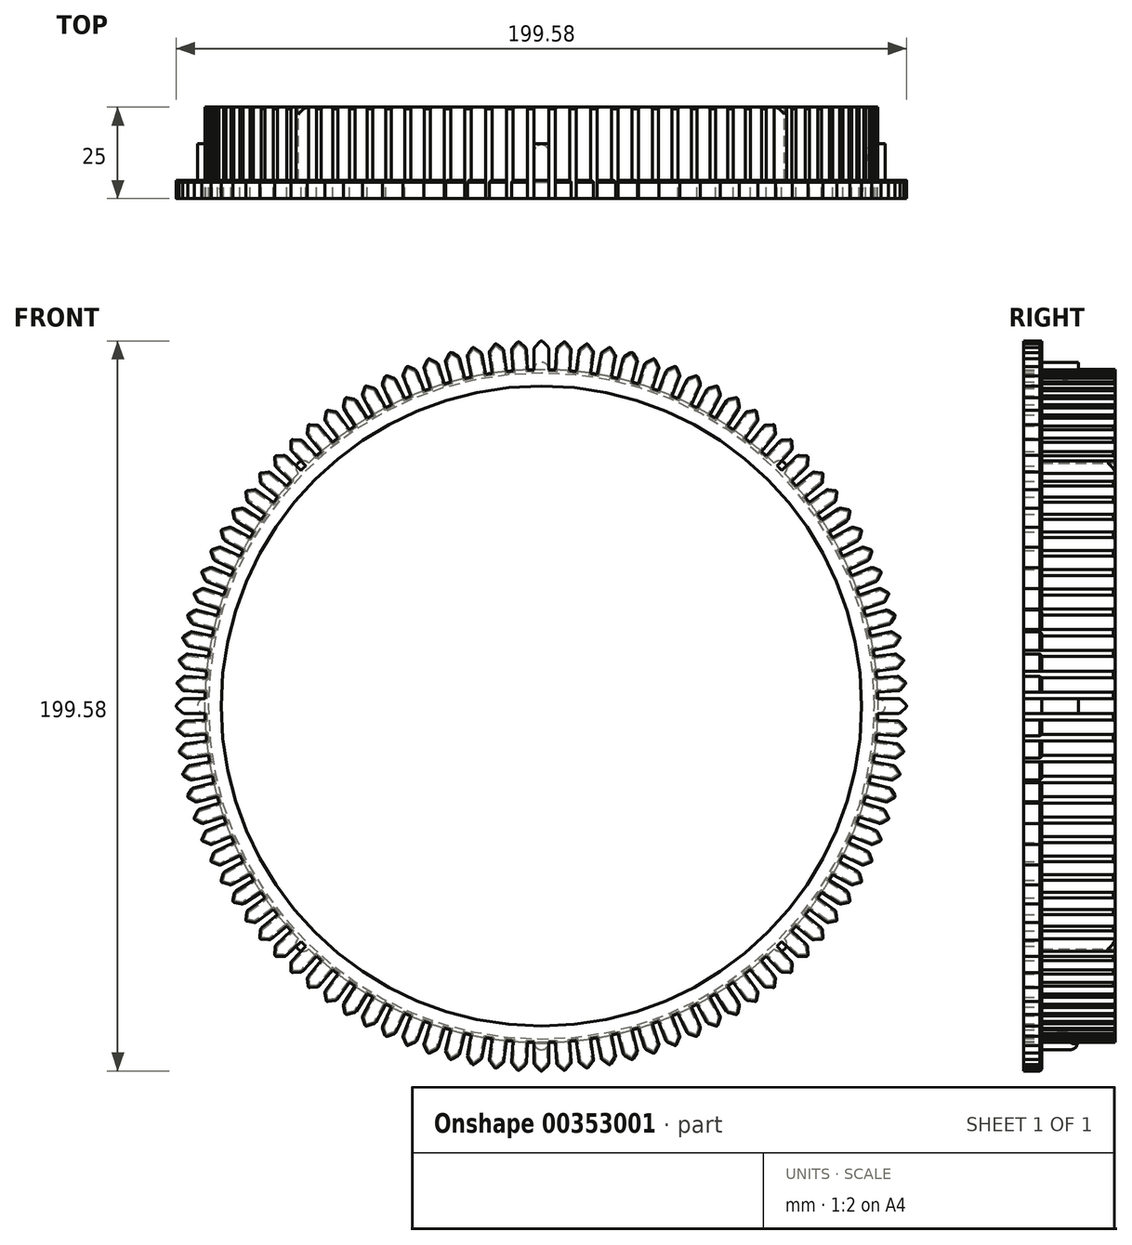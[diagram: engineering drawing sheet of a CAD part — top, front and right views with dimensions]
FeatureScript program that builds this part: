
annotation { "Feature Type Name" : "Feature", "Feature Type Description" : "" }
export const myFeature = defineFeature(function(context is Context, id is Id, definition is map)
    precondition{}
    {
        {
            var Q0;
            Q0=qCreatedBy(makeId("Front.planeOp"),FACE);
            var sketch = newSketch(context, id + "F0", { "sketchPlane" : qUnion([Q0])});
            skArc(sketch, "E0", {"start": v(-18.82, 88) * mm, "mid": v(-19.63, 87.83) * mm, "end": v(-20.44, 87.65) * mm});
            skCircle(sketch, "E1", {"center": v(0, 0) * mm, "radius": 98 * mm, "construction": true});
            skLineSegment(sketch, "E2", {"start": v(0, 100) * mm, "end": v(0, -100) * mm, "construction": true});
            skLineSegment(sketch, "E3", {"start": v(-100, 0) * mm, "end": v(100, 0) * mm, "construction": true});
            skLineSegment(sketch, "E4", {"start": v(-2, 89.98) * mm, "end": v(-2, 97.57) * mm});
            skLineSegment(sketch, "E5", {"start": v(-1.71, 98.27) * mm, "end": v(-0.36, 99.64) * mm});
            skPoint(sketch, "E6.visualSharp", {"position": v(-2, 97.98) * mm});
            skArc(sketch, "E6.filletArc", {"start": v(-1.71, 98.27) * mm, "mid": v(-1.92, 97.95) * mm, "end": v(-2, 97.57) * mm});
            skLineSegment(sketch, "E7.MirrorCS", {"start": v(1.71, 98.27) * mm, "end": v(0.36, 99.64) * mm});
            skArc(sketch, "E8.MirrorCS", {"start": v(1.71, 98.27) * mm, "mid": v(1.92, 97.95) * mm, "end": v(2, 97.57) * mm});
            skLineSegment(sketch, "E9.MirrorCS", {"start": v(2, 89.98) * mm, "end": v(2, 97.57) * mm});
            skPoint(sketch, "E10.visualSharp", {"position": v(0, 100) * mm});
            skArc(sketch, "E10.filletArc", {"start": v(0.36, 99.64) * mm, "mid": v(0, 99.79) * mm, "end": v(-0.36, 99.64) * mm});
            skLineSegment(sketch, "E11.1.0", {"start": v(-7.88, 97.97) * mm, "end": v(-6.61, 99.42) * mm});
            skArc(sketch, "E11.1.1", {"start": v(-5.9, 99.47) * mm, "mid": v(-6.27, 99.6) * mm, "end": v(-6.61, 99.42) * mm});
            skLineSegment(sketch, "E11.1.2", {"start": v(-4.46, 98.19) * mm, "end": v(-5.9, 99.47) * mm});
            skArc(sketch, "E11.1.3", {"start": v(-4.46, 98.19) * mm, "mid": v(-4.23, 97.88) * mm, "end": v(-4.13, 97.5) * mm});
            skArc(sketch, "E11.1.4", {"start": v(-7.88, 97.97) * mm, "mid": v(-8.07, 97.63) * mm, "end": v(-8.12, 97.25) * mm});
            skLineSegment(sketch, "E11.1.5", {"start": v(-7.65, 89.67) * mm, "end": v(-8.12, 97.25) * mm});
            skLineSegment(sketch, "E11.1.6", {"start": v(-3.65, 89.93) * mm, "end": v(-4.13, 97.5) * mm});
            skLineSegment(sketch, "E11.2.0", {"start": v(-14.01, 97.28) * mm, "end": v(-12.84, 98.81) * mm});
            skArc(sketch, "E11.2.1", {"start": v(-12.14, 98.9) * mm, "mid": v(-12.5, 99) * mm, "end": v(-12.84, 98.81) * mm});
            skLineSegment(sketch, "E11.2.2", {"start": v(-10.62, 97.71) * mm, "end": v(-12.14, 98.9) * mm});
            skArc(sketch, "E11.2.3", {"start": v(-10.62, 97.71) * mm, "mid": v(-10.37, 97.42) * mm, "end": v(-10.24, 97.05) * mm});
            skArc(sketch, "E11.2.4", {"start": v(-14.01, 97.28) * mm, "mid": v(-14.19, 96.94) * mm, "end": v(-14.21, 96.55) * mm});
            skLineSegment(sketch, "E11.2.5", {"start": v(-13.26, 89.02) * mm, "end": v(-14.21, 96.55) * mm});
            skLineSegment(sketch, "E11.2.6", {"start": v(-9.3, 89.52) * mm, "end": v(-10.24, 97.05) * mm});
            skLineSegment(sketch, "E11.3.0", {"start": v(-20.1, 96.21) * mm, "end": v(-19.02, 97.8) * mm});
            skArc(sketch, "E11.3.1", {"start": v(-18.32, 97.94) * mm, "mid": v(-18.7, 98.02) * mm, "end": v(-19.02, 97.8) * mm});
            skLineSegment(sketch, "E11.3.2", {"start": v(-16.73, 96.85) * mm, "end": v(-18.32, 97.94) * mm});
            skArc(sketch, "E11.3.3", {"start": v(-16.73, 96.85) * mm, "mid": v(-16.46, 96.57) * mm, "end": v(-16.32, 96.21) * mm});
            skArc(sketch, "E11.3.4", {"start": v(-20.1, 96.21) * mm, "mid": v(-20.24, 95.85) * mm, "end": v(-20.25, 95.47) * mm});
            skLineSegment(sketch, "E11.3.5", {"start": v(-18.82, 88) * mm, "end": v(-20.25, 95.47) * mm});
            skLineSegment(sketch, "E11.3.6", {"start": v(-14.9, 88.76) * mm, "end": v(-16.32, 96.21) * mm});
            skLineSegment(sketch, "E11.4.0", {"start": v(-26.1, 94.76) * mm, "end": v(-25.12, 96.42) * mm});
            skArc(sketch, "E11.4.1", {"start": v(-24.44, 96.6) * mm, "mid": v(-24.82, 96.65) * mm, "end": v(-25.12, 96.42) * mm});
            skLineSegment(sketch, "E11.4.2", {"start": v(-22.78, 95.6) * mm, "end": v(-24.44, 96.6) * mm});
            skArc(sketch, "E11.4.3", {"start": v(-22.78, 95.6) * mm, "mid": v(-22.5, 95.35) * mm, "end": v(-22.33, 95) * mm});
            skArc(sketch, "E11.4.4", {"start": v(-26.1, 94.76) * mm, "mid": v(-26.22, 94.4) * mm, "end": v(-26.2, 94) * mm});
            skLineSegment(sketch, "E11.4.5", {"start": v(-24.31, 86.65) * mm, "end": v(-26.2, 94) * mm});
            skLineSegment(sketch, "E11.4.6", {"start": v(-20.44, 87.65) * mm, "end": v(-22.33, 95) * mm});
            skLineSegment(sketch, "E11.5.0", {"start": v(-32, 92.93) * mm, "end": v(-31.13, 94.65) * mm});
            skArc(sketch, "E11.5.1", {"start": v(-30.45, 94.87) * mm, "mid": v(-30.84, 94.9) * mm, "end": v(-31.13, 94.65) * mm});
            skLineSegment(sketch, "E11.5.2", {"start": v(-28.74, 94) * mm, "end": v(-30.45, 94.87) * mm});
            skArc(sketch, "E11.5.3", {"start": v(-28.74, 94) * mm, "mid": v(-28.44, 93.75) * mm, "end": v(-28.25, 93.41) * mm});
            skArc(sketch, "E11.5.4", {"start": v(-32, 92.93) * mm, "mid": v(-32.1, 92.56) * mm, "end": v(-32.05, 92.17) * mm});
            skLineSegment(sketch, "E11.5.5", {"start": v(-29.7, 84.96) * mm, "end": v(-32.05, 92.17) * mm});
            skLineSegment(sketch, "E11.5.6", {"start": v(-25.9, 86.2) * mm, "end": v(-28.25, 93.41) * mm});
            skLineSegment(sketch, "E11.6.0", {"start": v(-37.77, 90.74) * mm, "end": v(-37.01, 92.51) * mm});
            skArc(sketch, "E11.6.1", {"start": v(-36.35, 92.77) * mm, "mid": v(-36.73, 92.78) * mm, "end": v(-37.01, 92.51) * mm});
            skLineSegment(sketch, "E11.6.2", {"start": v(-34.59, 92) * mm, "end": v(-36.35, 92.77) * mm});
            skArc(sketch, "E11.6.3", {"start": v(-34.59, 92) * mm, "mid": v(-34.27, 91.78) * mm, "end": v(-34.06, 91.45) * mm});
            skArc(sketch, "E11.6.4", {"start": v(-37.77, 90.74) * mm, "mid": v(-37.85, 90.36) * mm, "end": v(-37.78, 89.98) * mm});
            skLineSegment(sketch, "E11.6.5", {"start": v(-34.98, 82.92) * mm, "end": v(-37.78, 89.98) * mm});
            skLineSegment(sketch, "E11.6.6", {"start": v(-31.26, 84.4) * mm, "end": v(-34.06, 91.45) * mm});
            skLineSegment(sketch, "E11.7.0", {"start": v(-43.39, 88.2) * mm, "end": v(-42.75, 90) * mm});
            skArc(sketch, "E11.7.1", {"start": v(-42.1, 90.3) * mm, "mid": v(-42.49, 90.3) * mm, "end": v(-42.75, 90) * mm});
            skLineSegment(sketch, "E11.7.2", {"start": v(-40.3, 89.65) * mm, "end": v(-42.1, 90.3) * mm});
            skArc(sketch, "E11.7.3", {"start": v(-40.3, 89.65) * mm, "mid": v(-39.96, 89.45) * mm, "end": v(-39.73, 89.13) * mm});
            skArc(sketch, "E11.7.4", {"start": v(-43.39, 88.2) * mm, "mid": v(-43.45, 87.8) * mm, "end": v(-43.35, 87.43) * mm});
            skLineSegment(sketch, "E11.7.5", {"start": v(-40.12, 80.56) * mm, "end": v(-43.35, 87.43) * mm});
            skLineSegment(sketch, "E11.7.6", {"start": v(-36.5, 82.27) * mm, "end": v(-39.73, 89.13) * mm});
            skLineSegment(sketch, "E11.8.0", {"start": v(-48.84, 85.3) * mm, "end": v(-48.31, 87.14) * mm});
            skArc(sketch, "E11.8.1", {"start": v(-47.7, 87.49) * mm, "mid": v(-48.07, 87.45) * mm, "end": v(-48.31, 87.14) * mm});
            skLineSegment(sketch, "E11.8.2", {"start": v(-45.84, 86.94) * mm, "end": v(-47.7, 87.49) * mm});
            skArc(sketch, "E11.8.3", {"start": v(-45.84, 86.94) * mm, "mid": v(-45.5, 86.76) * mm, "end": v(-45.25, 86.46) * mm});
            skArc(sketch, "E11.8.4", {"start": v(-48.84, 85.3) * mm, "mid": v(-48.87, 84.9) * mm, "end": v(-48.76, 84.54) * mm});
            skLineSegment(sketch, "E11.8.5", {"start": v(-45.1, 77.88) * mm, "end": v(-48.76, 84.54) * mm});
            skLineSegment(sketch, "E11.8.6", {"start": v(-41.6, 79.81) * mm, "end": v(-45.25, 86.46) * mm});
            skLineSegment(sketch, "E11.9.0", {"start": v(-54.1, 82.06) * mm, "end": v(-53.7, 83.94) * mm});
            skArc(sketch, "E11.9.1", {"start": v(-53.1, 84.32) * mm, "mid": v(-53.47, 84.25) * mm, "end": v(-53.7, 83.94) * mm});
            skLineSegment(sketch, "E11.9.2", {"start": v(-51.21, 83.9) * mm, "end": v(-53.1, 84.32) * mm});
            skArc(sketch, "E11.9.3", {"start": v(-51.21, 83.9) * mm, "mid": v(-50.86, 83.73) * mm, "end": v(-50.6, 83.45) * mm});
            skArc(sketch, "E11.9.4", {"start": v(-54.1, 82.06) * mm, "mid": v(-54.1, 81.67) * mm, "end": v(-53.97, 81.3) * mm});
            skLineSegment(sketch, "E11.9.5", {"start": v(-49.9, 74.9) * mm, "end": v(-53.97, 81.3) * mm});
            skLineSegment(sketch, "E11.9.6", {"start": v(-46.52, 77.04) * mm, "end": v(-50.6, 83.45) * mm});
            skLineSegment(sketch, "E11.10.0", {"start": v(-59.15, 78.5) * mm, "end": v(-58.86, 80.4) * mm});
            skArc(sketch, "E11.10.1", {"start": v(-58.28, 80.82) * mm, "mid": v(-58.65, 80.73) * mm, "end": v(-58.86, 80.4) * mm});
            skLineSegment(sketch, "E11.10.2", {"start": v(-56.38, 80.5) * mm, "end": v(-58.28, 80.82) * mm});
            skArc(sketch, "E11.10.3", {"start": v(-56.38, 80.5) * mm, "mid": v(-56.02, 80.37) * mm, "end": v(-55.73, 80.11) * mm});
            skArc(sketch, "E11.10.4", {"start": v(-59.15, 78.5) * mm, "mid": v(-59.13, 78.11) * mm, "end": v(-58.97, 77.76) * mm});
            skLineSegment(sketch, "E11.10.5", {"start": v(-54.5, 71.62) * mm, "end": v(-58.97, 77.76) * mm});
            skLineSegment(sketch, "E11.10.6", {"start": v(-51.27, 73.97) * mm, "end": v(-55.73, 80.11) * mm});
            skLineSegment(sketch, "E11.11.0", {"start": v(-63.96, 74.63) * mm, "end": v(-63.79, 76.55) * mm});
            skArc(sketch, "E11.11.1", {"start": v(-63.24, 77) * mm, "mid": v(-63.6, 76.89) * mm, "end": v(-63.79, 76.55) * mm});
            skLineSegment(sketch, "E11.11.2", {"start": v(-61.32, 76.81) * mm, "end": v(-63.24, 77) * mm});
            skArc(sketch, "E11.11.3", {"start": v(-61.32, 76.81) * mm, "mid": v(-60.95, 76.7) * mm, "end": v(-60.65, 76.45) * mm});
            skArc(sketch, "E11.11.4", {"start": v(-63.96, 74.63) * mm, "mid": v(-63.92, 74.24) * mm, "end": v(-63.73, 73.9) * mm});
            skLineSegment(sketch, "E11.11.5", {"start": v(-58.9, 68.05) * mm, "end": v(-63.73, 73.9) * mm});
            skLineSegment(sketch, "E11.11.6", {"start": v(-55.81, 70.6) * mm, "end": v(-60.65, 76.45) * mm});
            skLineSegment(sketch, "E11.12.0", {"start": v(-68.52, 70.47) * mm, "end": v(-68.47, 72.4) * mm});
            skArc(sketch, "E11.12.1", {"start": v(-67.95, 72.88) * mm, "mid": v(-68.31, 72.74) * mm, "end": v(-68.47, 72.4) * mm});
            skLineSegment(sketch, "E11.12.2", {"start": v(-66.02, 72.8) * mm, "end": v(-67.95, 72.88) * mm});
            skArc(sketch, "E11.12.3", {"start": v(-66.02, 72.8) * mm, "mid": v(-65.65, 72.72) * mm, "end": v(-65.33, 72.5) * mm});
            skArc(sketch, "E11.12.4", {"start": v(-68.52, 70.47) * mm, "mid": v(-68.45, 70.08) * mm, "end": v(-68.25, 69.76) * mm});
            skLineSegment(sketch, "E11.12.5", {"start": v(-63.05, 64.22) * mm, "end": v(-68.25, 69.76) * mm});
            skLineSegment(sketch, "E11.12.6", {"start": v(-60.14, 66.96) * mm, "end": v(-65.33, 72.5) * mm});
            skLineSegment(sketch, "E11.13.0", {"start": v(-72.8, 66.02) * mm, "end": v(-72.88, 67.95) * mm});
            skArc(sketch, "E11.13.1", {"start": v(-72.4, 68.47) * mm, "mid": v(-72.74, 68.31) * mm, "end": v(-72.88, 67.95) * mm});
            skLineSegment(sketch, "E11.13.2", {"start": v(-70.47, 68.52) * mm, "end": v(-72.4, 68.47) * mm});
            skArc(sketch, "E11.13.3", {"start": v(-70.47, 68.52) * mm, "mid": v(-70.08, 68.45) * mm, "end": v(-69.76, 68.25) * mm});
            skArc(sketch, "E11.13.4", {"start": v(-72.8, 66.02) * mm, "mid": v(-72.72, 65.65) * mm, "end": v(-72.5, 65.33) * mm});
            skLineSegment(sketch, "E11.13.5", {"start": v(-66.96, 60.14) * mm, "end": v(-72.5, 65.33) * mm});
            skLineSegment(sketch, "E11.13.6", {"start": v(-64.22, 63.05) * mm, "end": v(-69.76, 68.25) * mm});
            skLineSegment(sketch, "E11.14.0", {"start": v(-76.81, 61.32) * mm, "end": v(-77, 63.24) * mm});
            skArc(sketch, "E11.14.1", {"start": v(-76.55, 63.79) * mm, "mid": v(-76.89, 63.6) * mm, "end": v(-77, 63.24) * mm});
            skLineSegment(sketch, "E11.14.2", {"start": v(-74.63, 63.96) * mm, "end": v(-76.55, 63.79) * mm});
            skArc(sketch, "E11.14.3", {"start": v(-74.63, 63.96) * mm, "mid": v(-74.24, 63.92) * mm, "end": v(-73.9, 63.73) * mm});
            skArc(sketch, "E11.14.4", {"start": v(-76.81, 61.32) * mm, "mid": v(-76.7, 60.95) * mm, "end": v(-76.45, 60.65) * mm});
            skLineSegment(sketch, "E11.14.5", {"start": v(-70.6, 55.81) * mm, "end": v(-76.45, 60.65) * mm});
            skLineSegment(sketch, "E11.14.6", {"start": v(-68.05, 58.9) * mm, "end": v(-73.9, 63.73) * mm});
            skLineSegment(sketch, "E11.15.0", {"start": v(-80.5, 56.38) * mm, "end": v(-80.82, 58.28) * mm});
            skArc(sketch, "E11.15.1", {"start": v(-80.4, 58.86) * mm, "mid": v(-80.73, 58.65) * mm, "end": v(-80.82, 58.28) * mm});
            skLineSegment(sketch, "E11.15.2", {"start": v(-78.5, 59.15) * mm, "end": v(-80.4, 58.86) * mm});
            skArc(sketch, "E11.15.3", {"start": v(-78.5, 59.15) * mm, "mid": v(-78.11, 59.13) * mm, "end": v(-77.76, 58.97) * mm});
            skArc(sketch, "E11.15.4", {"start": v(-80.5, 56.38) * mm, "mid": v(-80.37, 56.02) * mm, "end": v(-80.11, 55.73) * mm});
            skLineSegment(sketch, "E11.15.5", {"start": v(-73.97, 51.27) * mm, "end": v(-80.11, 55.73) * mm});
            skLineSegment(sketch, "E11.15.6", {"start": v(-71.62, 54.5) * mm, "end": v(-77.76, 58.97) * mm});
            skLineSegment(sketch, "E11.16.0", {"start": v(-83.9, 51.21) * mm, "end": v(-84.32, 53.1) * mm});
            skArc(sketch, "E11.16.1", {"start": v(-83.94, 53.7) * mm, "mid": v(-84.25, 53.47) * mm, "end": v(-84.32, 53.1) * mm});
            skLineSegment(sketch, "E11.16.2", {"start": v(-82.06, 54.1) * mm, "end": v(-83.94, 53.7) * mm});
            skArc(sketch, "E11.16.3", {"start": v(-82.06, 54.1) * mm, "mid": v(-81.67, 54.1) * mm, "end": v(-81.3, 53.97) * mm});
            skArc(sketch, "E11.16.4", {"start": v(-83.9, 51.21) * mm, "mid": v(-83.73, 50.86) * mm, "end": v(-83.45, 50.6) * mm});
            skLineSegment(sketch, "E11.16.5", {"start": v(-77.04, 46.52) * mm, "end": v(-83.45, 50.6) * mm});
            skLineSegment(sketch, "E11.16.6", {"start": v(-74.9, 49.9) * mm, "end": v(-81.3, 53.97) * mm});
            skLineSegment(sketch, "E11.17.0", {"start": v(-86.94, 45.84) * mm, "end": v(-87.49, 47.7) * mm});
            skArc(sketch, "E11.17.1", {"start": v(-87.14, 48.31) * mm, "mid": v(-87.45, 48.07) * mm, "end": v(-87.49, 47.7) * mm});
            skLineSegment(sketch, "E11.17.2", {"start": v(-85.3, 48.84) * mm, "end": v(-87.14, 48.31) * mm});
            skArc(sketch, "E11.17.3", {"start": v(-85.3, 48.84) * mm, "mid": v(-84.9, 48.87) * mm, "end": v(-84.54, 48.76) * mm});
            skArc(sketch, "E11.17.4", {"start": v(-86.94, 45.84) * mm, "mid": v(-86.76, 45.5) * mm, "end": v(-86.46, 45.25) * mm});
            skLineSegment(sketch, "E11.17.5", {"start": v(-79.81, 41.6) * mm, "end": v(-86.46, 45.25) * mm});
            skLineSegment(sketch, "E11.17.6", {"start": v(-77.88, 45.1) * mm, "end": v(-84.54, 48.76) * mm});
            skLineSegment(sketch, "E11.18.0", {"start": v(-89.65, 40.3) * mm, "end": v(-90.3, 42.1) * mm});
            skArc(sketch, "E11.18.1", {"start": v(-90, 42.75) * mm, "mid": v(-90.3, 42.49) * mm, "end": v(-90.3, 42.1) * mm});
            skLineSegment(sketch, "E11.18.2", {"start": v(-88.2, 43.39) * mm, "end": v(-90, 42.75) * mm});
            skArc(sketch, "E11.18.3", {"start": v(-88.2, 43.39) * mm, "mid": v(-87.8, 43.45) * mm, "end": v(-87.43, 43.35) * mm});
            skArc(sketch, "E11.18.4", {"start": v(-89.65, 40.3) * mm, "mid": v(-89.45, 39.96) * mm, "end": v(-89.13, 39.73) * mm});
            skLineSegment(sketch, "E11.18.5", {"start": v(-82.27, 36.5) * mm, "end": v(-89.13, 39.73) * mm});
            skLineSegment(sketch, "E11.18.6", {"start": v(-80.56, 40.12) * mm, "end": v(-87.43, 43.35) * mm});
            skLineSegment(sketch, "E11.19.0", {"start": v(-92, 34.59) * mm, "end": v(-92.77, 36.35) * mm});
            skArc(sketch, "E11.19.1", {"start": v(-92.51, 37.01) * mm, "mid": v(-92.78, 36.73) * mm, "end": v(-92.77, 36.35) * mm});
            skLineSegment(sketch, "E11.19.2", {"start": v(-90.74, 37.77) * mm, "end": v(-92.51, 37.01) * mm});
            skArc(sketch, "E11.19.3", {"start": v(-90.74, 37.77) * mm, "mid": v(-90.36, 37.85) * mm, "end": v(-89.98, 37.78) * mm});
            skArc(sketch, "E11.19.4", {"start": v(-92, 34.59) * mm, "mid": v(-91.78, 34.27) * mm, "end": v(-91.45, 34.06) * mm});
            skLineSegment(sketch, "E11.19.5", {"start": v(-84.4, 31.26) * mm, "end": v(-91.45, 34.06) * mm});
            skLineSegment(sketch, "E11.19.6", {"start": v(-82.92, 34.98) * mm, "end": v(-89.98, 37.78) * mm});
            skLineSegment(sketch, "E11.20.0", {"start": v(-94, 28.74) * mm, "end": v(-94.87, 30.45) * mm});
            skArc(sketch, "E11.20.1", {"start": v(-94.65, 31.13) * mm, "mid": v(-94.9, 30.84) * mm, "end": v(-94.87, 30.45) * mm});
            skLineSegment(sketch, "E11.20.2", {"start": v(-92.93, 32) * mm, "end": v(-94.65, 31.13) * mm});
            skArc(sketch, "E11.20.3", {"start": v(-92.93, 32) * mm, "mid": v(-92.56, 32.1) * mm, "end": v(-92.17, 32.05) * mm});
            skArc(sketch, "E11.20.4", {"start": v(-94, 28.74) * mm, "mid": v(-93.75, 28.44) * mm, "end": v(-93.41, 28.25) * mm});
            skLineSegment(sketch, "E11.20.5", {"start": v(-86.2, 25.9) * mm, "end": v(-93.41, 28.25) * mm});
            skLineSegment(sketch, "E11.20.6", {"start": v(-84.96, 29.7) * mm, "end": v(-92.17, 32.05) * mm});
            skLineSegment(sketch, "E11.21.0", {"start": v(-95.6, 22.78) * mm, "end": v(-96.6, 24.44) * mm});
            skArc(sketch, "E11.21.1", {"start": v(-96.42, 25.12) * mm, "mid": v(-96.65, 24.82) * mm, "end": v(-96.6, 24.44) * mm});
            skLineSegment(sketch, "E11.21.2", {"start": v(-94.76, 26.1) * mm, "end": v(-96.42, 25.12) * mm});
            skArc(sketch, "E11.21.3", {"start": v(-94.76, 26.1) * mm, "mid": v(-94.4, 26.22) * mm, "end": v(-94, 26.2) * mm});
            skArc(sketch, "E11.21.4", {"start": v(-95.6, 22.78) * mm, "mid": v(-95.35, 22.5) * mm, "end": v(-95, 22.33) * mm});
            skLineSegment(sketch, "E11.21.5", {"start": v(-87.65, 20.44) * mm, "end": v(-95, 22.33) * mm});
            skLineSegment(sketch, "E11.21.6", {"start": v(-86.65, 24.31) * mm, "end": v(-94, 26.2) * mm});
            skLineSegment(sketch, "E11.22.0", {"start": v(-96.85, 16.73) * mm, "end": v(-97.94, 18.32) * mm});
            skArc(sketch, "E11.22.1", {"start": v(-97.8, 19.02) * mm, "mid": v(-98.02, 18.7) * mm, "end": v(-97.94, 18.32) * mm});
            skLineSegment(sketch, "E11.22.2", {"start": v(-96.21, 20.1) * mm, "end": v(-97.8, 19.02) * mm});
            skArc(sketch, "E11.22.3", {"start": v(-96.21, 20.1) * mm, "mid": v(-95.85, 20.24) * mm, "end": v(-95.47, 20.25) * mm});
            skArc(sketch, "E11.22.4", {"start": v(-96.85, 16.73) * mm, "mid": v(-96.57, 16.46) * mm, "end": v(-96.21, 16.32) * mm});
            skLineSegment(sketch, "E11.22.5", {"start": v(-88.76, 14.9) * mm, "end": v(-96.21, 16.32) * mm});
            skLineSegment(sketch, "E11.22.6", {"start": v(-88, 18.82) * mm, "end": v(-95.47, 20.25) * mm});
            skLineSegment(sketch, "E11.23.0", {"start": v(-97.71, 10.62) * mm, "end": v(-98.9, 12.14) * mm});
            skArc(sketch, "E11.23.1", {"start": v(-98.81, 12.84) * mm, "mid": v(-99, 12.5) * mm, "end": v(-98.9, 12.14) * mm});
            skLineSegment(sketch, "E11.23.2", {"start": v(-97.28, 14.01) * mm, "end": v(-98.81, 12.84) * mm});
            skArc(sketch, "E11.23.3", {"start": v(-97.28, 14.01) * mm, "mid": v(-96.94, 14.19) * mm, "end": v(-96.55, 14.21) * mm});
            skArc(sketch, "E11.23.4", {"start": v(-97.71, 10.62) * mm, "mid": v(-97.42, 10.37) * mm, "end": v(-97.05, 10.24) * mm});
            skLineSegment(sketch, "E11.23.5", {"start": v(-89.52, 9.3) * mm, "end": v(-97.05, 10.24) * mm});
            skLineSegment(sketch, "E11.23.6", {"start": v(-89.02, 13.26) * mm, "end": v(-96.55, 14.21) * mm});
            skLineSegment(sketch, "E11.24.0", {"start": v(-98.19, 4.46) * mm, "end": v(-99.47, 5.9) * mm});
            skArc(sketch, "E11.24.1", {"start": v(-99.42, 6.61) * mm, "mid": v(-99.6, 6.27) * mm, "end": v(-99.47, 5.9) * mm});
            skLineSegment(sketch, "E11.24.2", {"start": v(-97.97, 7.88) * mm, "end": v(-99.42, 6.61) * mm});
            skArc(sketch, "E11.24.3", {"start": v(-97.97, 7.88) * mm, "mid": v(-97.63, 8.07) * mm, "end": v(-97.25, 8.12) * mm});
            skArc(sketch, "E11.24.4", {"start": v(-98.19, 4.46) * mm, "mid": v(-97.88, 4.23) * mm, "end": v(-97.5, 4.13) * mm});
            skLineSegment(sketch, "E11.24.5", {"start": v(-89.93, 3.65) * mm, "end": v(-97.5, 4.13) * mm});
            skLineSegment(sketch, "E11.24.6", {"start": v(-89.67, 7.65) * mm, "end": v(-97.25, 8.12) * mm});
            skLineSegment(sketch, "E11.25.0", {"start": v(-98.27, -1.71) * mm, "end": v(-99.64, -0.36) * mm});
            skArc(sketch, "E11.25.1", {"start": v(-99.64, 0.36) * mm, "mid": v(-99.79, 0) * mm, "end": v(-99.64, -0.36) * mm});
            skLineSegment(sketch, "E11.25.2", {"start": v(-98.27, 1.71) * mm, "end": v(-99.64, 0.36) * mm});
            skArc(sketch, "E11.25.3", {"start": v(-98.27, 1.71) * mm, "mid": v(-97.95, 1.92) * mm, "end": v(-97.57, 2) * mm});
            skArc(sketch, "E11.25.4", {"start": v(-98.27, -1.71) * mm, "mid": v(-97.95, -1.92) * mm, "end": v(-97.57, -2) * mm});
            skLineSegment(sketch, "E11.25.5", {"start": v(-89.98, -2) * mm, "end": v(-97.57, -2) * mm});
            skLineSegment(sketch, "E11.25.6", {"start": v(-89.98, 2) * mm, "end": v(-97.57, 2) * mm});
            skLineSegment(sketch, "E11.26.0", {"start": v(-97.97, -7.88) * mm, "end": v(-99.42, -6.61) * mm});
            skArc(sketch, "E11.26.1", {"start": v(-99.47, -5.9) * mm, "mid": v(-99.6, -6.27) * mm, "end": v(-99.42, -6.61) * mm});
            skLineSegment(sketch, "E11.26.2", {"start": v(-98.19, -4.46) * mm, "end": v(-99.47, -5.9) * mm});
            skArc(sketch, "E11.26.3", {"start": v(-98.19, -4.46) * mm, "mid": v(-97.88, -4.23) * mm, "end": v(-97.5, -4.13) * mm});
            skArc(sketch, "E11.26.4", {"start": v(-97.97, -7.88) * mm, "mid": v(-97.63, -8.07) * mm, "end": v(-97.25, -8.12) * mm});
            skLineSegment(sketch, "E11.26.5", {"start": v(-89.67, -7.65) * mm, "end": v(-97.25, -8.12) * mm});
            skLineSegment(sketch, "E11.26.6", {"start": v(-89.93, -3.65) * mm, "end": v(-97.5, -4.13) * mm});
            skLineSegment(sketch, "E11.27.0", {"start": v(-97.28, -14.01) * mm, "end": v(-98.81, -12.84) * mm});
            skArc(sketch, "E11.27.1", {"start": v(-98.9, -12.14) * mm, "mid": v(-99, -12.5) * mm, "end": v(-98.81, -12.84) * mm});
            skLineSegment(sketch, "E11.27.2", {"start": v(-97.71, -10.62) * mm, "end": v(-98.9, -12.14) * mm});
            skArc(sketch, "E11.27.3", {"start": v(-97.71, -10.62) * mm, "mid": v(-97.42, -10.37) * mm, "end": v(-97.05, -10.24) * mm});
            skArc(sketch, "E11.27.4", {"start": v(-97.28, -14.01) * mm, "mid": v(-96.94, -14.19) * mm, "end": v(-96.55, -14.21) * mm});
            skLineSegment(sketch, "E11.27.5", {"start": v(-89.02, -13.26) * mm, "end": v(-96.55, -14.21) * mm});
            skLineSegment(sketch, "E11.27.6", {"start": v(-89.52, -9.3) * mm, "end": v(-97.05, -10.24) * mm});
            skLineSegment(sketch, "E11.28.0", {"start": v(-96.21, -20.1) * mm, "end": v(-97.8, -19.02) * mm});
            skArc(sketch, "E11.28.1", {"start": v(-97.94, -18.32) * mm, "mid": v(-98.02, -18.7) * mm, "end": v(-97.8, -19.02) * mm});
            skLineSegment(sketch, "E11.28.2", {"start": v(-96.85, -16.73) * mm, "end": v(-97.94, -18.32) * mm});
            skArc(sketch, "E11.28.3", {"start": v(-96.85, -16.73) * mm, "mid": v(-96.57, -16.46) * mm, "end": v(-96.21, -16.32) * mm});
            skArc(sketch, "E11.28.4", {"start": v(-96.21, -20.1) * mm, "mid": v(-95.85, -20.24) * mm, "end": v(-95.47, -20.25) * mm});
            skLineSegment(sketch, "E11.28.5", {"start": v(-88, -18.82) * mm, "end": v(-95.47, -20.25) * mm});
            skLineSegment(sketch, "E11.28.6", {"start": v(-88.76, -14.9) * mm, "end": v(-96.21, -16.32) * mm});
            skLineSegment(sketch, "E11.29.0", {"start": v(-94.76, -26.1) * mm, "end": v(-96.42, -25.12) * mm});
            skArc(sketch, "E11.29.1", {"start": v(-96.6, -24.44) * mm, "mid": v(-96.65, -24.82) * mm, "end": v(-96.42, -25.12) * mm});
            skLineSegment(sketch, "E11.29.2", {"start": v(-95.6, -22.78) * mm, "end": v(-96.6, -24.44) * mm});
            skArc(sketch, "E11.29.3", {"start": v(-95.6, -22.78) * mm, "mid": v(-95.35, -22.5) * mm, "end": v(-95, -22.33) * mm});
            skArc(sketch, "E11.29.4", {"start": v(-94.76, -26.1) * mm, "mid": v(-94.4, -26.22) * mm, "end": v(-94, -26.2) * mm});
            skLineSegment(sketch, "E11.29.5", {"start": v(-86.65, -24.31) * mm, "end": v(-94, -26.2) * mm});
            skLineSegment(sketch, "E11.29.6", {"start": v(-87.65, -20.44) * mm, "end": v(-95, -22.33) * mm});
            skLineSegment(sketch, "E11.30.0", {"start": v(-92.93, -32) * mm, "end": v(-94.65, -31.13) * mm});
            skArc(sketch, "E11.30.1", {"start": v(-94.87, -30.45) * mm, "mid": v(-94.9, -30.84) * mm, "end": v(-94.65, -31.13) * mm});
            skLineSegment(sketch, "E11.30.2", {"start": v(-94, -28.74) * mm, "end": v(-94.87, -30.45) * mm});
            skArc(sketch, "E11.30.3", {"start": v(-94, -28.74) * mm, "mid": v(-93.75, -28.44) * mm, "end": v(-93.41, -28.25) * mm});
            skArc(sketch, "E11.30.4", {"start": v(-92.93, -32) * mm, "mid": v(-92.56, -32.1) * mm, "end": v(-92.17, -32.05) * mm});
            skLineSegment(sketch, "E11.30.5", {"start": v(-84.96, -29.7) * mm, "end": v(-92.17, -32.05) * mm});
            skLineSegment(sketch, "E11.30.6", {"start": v(-86.2, -25.9) * mm, "end": v(-93.41, -28.25) * mm});
            skLineSegment(sketch, "E11.31.0", {"start": v(-90.74, -37.77) * mm, "end": v(-92.51, -37.01) * mm});
            skArc(sketch, "E11.31.1", {"start": v(-92.77, -36.35) * mm, "mid": v(-92.78, -36.73) * mm, "end": v(-92.51, -37.01) * mm});
            skLineSegment(sketch, "E11.31.2", {"start": v(-92, -34.59) * mm, "end": v(-92.77, -36.35) * mm});
            skArc(sketch, "E11.31.3", {"start": v(-92, -34.59) * mm, "mid": v(-91.78, -34.27) * mm, "end": v(-91.45, -34.06) * mm});
            skArc(sketch, "E11.31.4", {"start": v(-90.74, -37.77) * mm, "mid": v(-90.36, -37.85) * mm, "end": v(-89.98, -37.78) * mm});
            skLineSegment(sketch, "E11.31.5", {"start": v(-82.92, -34.98) * mm, "end": v(-89.98, -37.78) * mm});
            skLineSegment(sketch, "E11.31.6", {"start": v(-84.4, -31.26) * mm, "end": v(-91.45, -34.06) * mm});
            skLineSegment(sketch, "E11.32.0", {"start": v(-88.2, -43.39) * mm, "end": v(-90, -42.75) * mm});
            skArc(sketch, "E11.32.1", {"start": v(-90.3, -42.1) * mm, "mid": v(-90.3, -42.49) * mm, "end": v(-90, -42.75) * mm});
            skLineSegment(sketch, "E11.32.2", {"start": v(-89.65, -40.3) * mm, "end": v(-90.3, -42.1) * mm});
            skArc(sketch, "E11.32.3", {"start": v(-89.65, -40.3) * mm, "mid": v(-89.45, -39.96) * mm, "end": v(-89.13, -39.73) * mm});
            skArc(sketch, "E11.32.4", {"start": v(-88.2, -43.39) * mm, "mid": v(-87.8, -43.45) * mm, "end": v(-87.43, -43.35) * mm});
            skLineSegment(sketch, "E11.32.5", {"start": v(-80.56, -40.12) * mm, "end": v(-87.43, -43.35) * mm});
            skLineSegment(sketch, "E11.32.6", {"start": v(-82.27, -36.5) * mm, "end": v(-89.13, -39.73) * mm});
            skLineSegment(sketch, "E11.33.0", {"start": v(-85.3, -48.84) * mm, "end": v(-87.14, -48.31) * mm});
            skArc(sketch, "E11.33.1", {"start": v(-87.49, -47.7) * mm, "mid": v(-87.45, -48.07) * mm, "end": v(-87.14, -48.31) * mm});
            skLineSegment(sketch, "E11.33.2", {"start": v(-86.94, -45.84) * mm, "end": v(-87.49, -47.7) * mm});
            skArc(sketch, "E11.33.3", {"start": v(-86.94, -45.84) * mm, "mid": v(-86.76, -45.5) * mm, "end": v(-86.46, -45.25) * mm});
            skArc(sketch, "E11.33.4", {"start": v(-85.3, -48.84) * mm, "mid": v(-84.9, -48.87) * mm, "end": v(-84.54, -48.76) * mm});
            skLineSegment(sketch, "E11.33.5", {"start": v(-77.88, -45.1) * mm, "end": v(-84.54, -48.76) * mm});
            skLineSegment(sketch, "E11.33.6", {"start": v(-79.81, -41.6) * mm, "end": v(-86.46, -45.25) * mm});
            skLineSegment(sketch, "E11.34.0", {"start": v(-82.06, -54.1) * mm, "end": v(-83.94, -53.7) * mm});
            skArc(sketch, "E11.34.1", {"start": v(-84.32, -53.1) * mm, "mid": v(-84.25, -53.47) * mm, "end": v(-83.94, -53.7) * mm});
            skLineSegment(sketch, "E11.34.2", {"start": v(-83.9, -51.21) * mm, "end": v(-84.32, -53.1) * mm});
            skArc(sketch, "E11.34.3", {"start": v(-83.9, -51.21) * mm, "mid": v(-83.73, -50.86) * mm, "end": v(-83.45, -50.6) * mm});
            skArc(sketch, "E11.34.4", {"start": v(-82.06, -54.1) * mm, "mid": v(-81.67, -54.1) * mm, "end": v(-81.3, -53.97) * mm});
            skLineSegment(sketch, "E11.34.5", {"start": v(-74.9, -49.9) * mm, "end": v(-81.3, -53.97) * mm});
            skLineSegment(sketch, "E11.34.6", {"start": v(-77.04, -46.52) * mm, "end": v(-83.45, -50.6) * mm});
            skLineSegment(sketch, "E11.35.0", {"start": v(-78.5, -59.15) * mm, "end": v(-80.4, -58.86) * mm});
            skArc(sketch, "E11.35.1", {"start": v(-80.82, -58.28) * mm, "mid": v(-80.73, -58.65) * mm, "end": v(-80.4, -58.86) * mm});
            skLineSegment(sketch, "E11.35.2", {"start": v(-80.5, -56.38) * mm, "end": v(-80.82, -58.28) * mm});
            skArc(sketch, "E11.35.3", {"start": v(-80.5, -56.38) * mm, "mid": v(-80.37, -56.02) * mm, "end": v(-80.11, -55.73) * mm});
            skArc(sketch, "E11.35.4", {"start": v(-78.5, -59.15) * mm, "mid": v(-78.11, -59.13) * mm, "end": v(-77.76, -58.97) * mm});
            skLineSegment(sketch, "E11.35.5", {"start": v(-71.62, -54.5) * mm, "end": v(-77.76, -58.97) * mm});
            skLineSegment(sketch, "E11.35.6", {"start": v(-73.97, -51.27) * mm, "end": v(-80.11, -55.73) * mm});
            skLineSegment(sketch, "E11.36.0", {"start": v(-74.63, -63.96) * mm, "end": v(-76.55, -63.79) * mm});
            skArc(sketch, "E11.36.1", {"start": v(-77, -63.24) * mm, "mid": v(-76.89, -63.6) * mm, "end": v(-76.55, -63.79) * mm});
            skLineSegment(sketch, "E11.36.2", {"start": v(-76.81, -61.32) * mm, "end": v(-77, -63.24) * mm});
            skArc(sketch, "E11.36.3", {"start": v(-76.81, -61.32) * mm, "mid": v(-76.7, -60.95) * mm, "end": v(-76.45, -60.65) * mm});
            skArc(sketch, "E11.36.4", {"start": v(-74.63, -63.96) * mm, "mid": v(-74.24, -63.92) * mm, "end": v(-73.9, -63.73) * mm});
            skLineSegment(sketch, "E11.36.5", {"start": v(-68.05, -58.9) * mm, "end": v(-73.9, -63.73) * mm});
            skLineSegment(sketch, "E11.36.6", {"start": v(-70.6, -55.81) * mm, "end": v(-76.45, -60.65) * mm});
            skLineSegment(sketch, "E11.37.0", {"start": v(-70.47, -68.52) * mm, "end": v(-72.4, -68.47) * mm});
            skArc(sketch, "E11.37.1", {"start": v(-72.88, -67.95) * mm, "mid": v(-72.74, -68.31) * mm, "end": v(-72.4, -68.47) * mm});
            skLineSegment(sketch, "E11.37.2", {"start": v(-72.8, -66.02) * mm, "end": v(-72.88, -67.95) * mm});
            skArc(sketch, "E11.37.3", {"start": v(-72.8, -66.02) * mm, "mid": v(-72.72, -65.65) * mm, "end": v(-72.5, -65.33) * mm});
            skArc(sketch, "E11.37.4", {"start": v(-70.47, -68.52) * mm, "mid": v(-70.08, -68.45) * mm, "end": v(-69.76, -68.25) * mm});
            skLineSegment(sketch, "E11.37.5", {"start": v(-64.22, -63.05) * mm, "end": v(-69.76, -68.25) * mm});
            skLineSegment(sketch, "E11.37.6", {"start": v(-66.96, -60.14) * mm, "end": v(-72.5, -65.33) * mm});
            skLineSegment(sketch, "E11.38.0", {"start": v(-66.02, -72.8) * mm, "end": v(-67.95, -72.88) * mm});
            skArc(sketch, "E11.38.1", {"start": v(-68.47, -72.4) * mm, "mid": v(-68.31, -72.74) * mm, "end": v(-67.95, -72.88) * mm});
            skLineSegment(sketch, "E11.38.2", {"start": v(-68.52, -70.47) * mm, "end": v(-68.47, -72.4) * mm});
            skArc(sketch, "E11.38.3", {"start": v(-68.52, -70.47) * mm, "mid": v(-68.45, -70.08) * mm, "end": v(-68.25, -69.76) * mm});
            skArc(sketch, "E11.38.4", {"start": v(-66.02, -72.8) * mm, "mid": v(-65.65, -72.72) * mm, "end": v(-65.33, -72.5) * mm});
            skLineSegment(sketch, "E11.38.5", {"start": v(-60.14, -66.96) * mm, "end": v(-65.33, -72.5) * mm});
            skLineSegment(sketch, "E11.38.6", {"start": v(-63.05, -64.22) * mm, "end": v(-68.25, -69.76) * mm});
            skLineSegment(sketch, "E11.39.0", {"start": v(-61.32, -76.81) * mm, "end": v(-63.24, -77) * mm});
            skArc(sketch, "E11.39.1", {"start": v(-63.79, -76.55) * mm, "mid": v(-63.6, -76.89) * mm, "end": v(-63.24, -77) * mm});
            skLineSegment(sketch, "E11.39.2", {"start": v(-63.96, -74.63) * mm, "end": v(-63.79, -76.55) * mm});
            skArc(sketch, "E11.39.3", {"start": v(-63.96, -74.63) * mm, "mid": v(-63.92, -74.24) * mm, "end": v(-63.73, -73.9) * mm});
            skArc(sketch, "E11.39.4", {"start": v(-61.32, -76.81) * mm, "mid": v(-60.95, -76.7) * mm, "end": v(-60.65, -76.45) * mm});
            skLineSegment(sketch, "E11.39.5", {"start": v(-55.81, -70.6) * mm, "end": v(-60.65, -76.45) * mm});
            skLineSegment(sketch, "E11.39.6", {"start": v(-58.9, -68.05) * mm, "end": v(-63.73, -73.9) * mm});
            skLineSegment(sketch, "E11.40.0", {"start": v(-56.38, -80.5) * mm, "end": v(-58.28, -80.82) * mm});
            skArc(sketch, "E11.40.1", {"start": v(-58.86, -80.4) * mm, "mid": v(-58.65, -80.73) * mm, "end": v(-58.28, -80.82) * mm});
            skLineSegment(sketch, "E11.40.2", {"start": v(-59.15, -78.5) * mm, "end": v(-58.86, -80.4) * mm});
            skArc(sketch, "E11.40.3", {"start": v(-59.15, -78.5) * mm, "mid": v(-59.13, -78.11) * mm, "end": v(-58.97, -77.76) * mm});
            skArc(sketch, "E11.40.4", {"start": v(-56.38, -80.5) * mm, "mid": v(-56.02, -80.37) * mm, "end": v(-55.73, -80.11) * mm});
            skLineSegment(sketch, "E11.40.5", {"start": v(-51.27, -73.97) * mm, "end": v(-55.73, -80.11) * mm});
            skLineSegment(sketch, "E11.40.6", {"start": v(-54.5, -71.62) * mm, "end": v(-58.97, -77.76) * mm});
            skLineSegment(sketch, "E11.41.0", {"start": v(-51.21, -83.9) * mm, "end": v(-53.1, -84.32) * mm});
            skArc(sketch, "E11.41.1", {"start": v(-53.7, -83.94) * mm, "mid": v(-53.47, -84.25) * mm, "end": v(-53.1, -84.32) * mm});
            skLineSegment(sketch, "E11.41.2", {"start": v(-54.1, -82.06) * mm, "end": v(-53.7, -83.94) * mm});
            skArc(sketch, "E11.41.3", {"start": v(-54.1, -82.06) * mm, "mid": v(-54.1, -81.67) * mm, "end": v(-53.97, -81.3) * mm});
            skArc(sketch, "E11.41.4", {"start": v(-51.21, -83.9) * mm, "mid": v(-50.86, -83.73) * mm, "end": v(-50.6, -83.45) * mm});
            skLineSegment(sketch, "E11.41.5", {"start": v(-46.52, -77.04) * mm, "end": v(-50.6, -83.45) * mm});
            skLineSegment(sketch, "E11.41.6", {"start": v(-49.9, -74.9) * mm, "end": v(-53.97, -81.3) * mm});
            skLineSegment(sketch, "E11.42.0", {"start": v(-45.84, -86.94) * mm, "end": v(-47.7, -87.49) * mm});
            skArc(sketch, "E11.42.1", {"start": v(-48.31, -87.14) * mm, "mid": v(-48.07, -87.45) * mm, "end": v(-47.7, -87.49) * mm});
            skLineSegment(sketch, "E11.42.2", {"start": v(-48.84, -85.3) * mm, "end": v(-48.31, -87.14) * mm});
            skArc(sketch, "E11.42.3", {"start": v(-48.84, -85.3) * mm, "mid": v(-48.87, -84.9) * mm, "end": v(-48.76, -84.54) * mm});
            skArc(sketch, "E11.42.4", {"start": v(-45.84, -86.94) * mm, "mid": v(-45.5, -86.76) * mm, "end": v(-45.25, -86.46) * mm});
            skLineSegment(sketch, "E11.42.5", {"start": v(-41.6, -79.81) * mm, "end": v(-45.25, -86.46) * mm});
            skLineSegment(sketch, "E11.42.6", {"start": v(-45.1, -77.88) * mm, "end": v(-48.76, -84.54) * mm});
            skLineSegment(sketch, "E11.43.0", {"start": v(-40.3, -89.65) * mm, "end": v(-42.1, -90.3) * mm});
            skArc(sketch, "E11.43.1", {"start": v(-42.75, -90) * mm, "mid": v(-42.49, -90.3) * mm, "end": v(-42.1, -90.3) * mm});
            skLineSegment(sketch, "E11.43.2", {"start": v(-43.39, -88.2) * mm, "end": v(-42.75, -90) * mm});
            skArc(sketch, "E11.43.3", {"start": v(-43.39, -88.2) * mm, "mid": v(-43.45, -87.8) * mm, "end": v(-43.35, -87.43) * mm});
            skArc(sketch, "E11.43.4", {"start": v(-40.3, -89.65) * mm, "mid": v(-39.96, -89.45) * mm, "end": v(-39.73, -89.13) * mm});
            skLineSegment(sketch, "E11.43.5", {"start": v(-36.5, -82.27) * mm, "end": v(-39.73, -89.13) * mm});
            skLineSegment(sketch, "E11.43.6", {"start": v(-40.12, -80.56) * mm, "end": v(-43.35, -87.43) * mm});
            skLineSegment(sketch, "E11.44.0", {"start": v(-34.59, -92) * mm, "end": v(-36.35, -92.77) * mm});
            skArc(sketch, "E11.44.1", {"start": v(-37.01, -92.51) * mm, "mid": v(-36.73, -92.78) * mm, "end": v(-36.35, -92.77) * mm});
            skLineSegment(sketch, "E11.44.2", {"start": v(-37.77, -90.74) * mm, "end": v(-37.01, -92.51) * mm});
            skArc(sketch, "E11.44.3", {"start": v(-37.77, -90.74) * mm, "mid": v(-37.85, -90.36) * mm, "end": v(-37.78, -89.98) * mm});
            skArc(sketch, "E11.44.4", {"start": v(-34.59, -92) * mm, "mid": v(-34.27, -91.78) * mm, "end": v(-34.06, -91.45) * mm});
            skLineSegment(sketch, "E11.44.5", {"start": v(-31.26, -84.4) * mm, "end": v(-34.06, -91.45) * mm});
            skLineSegment(sketch, "E11.44.6", {"start": v(-34.98, -82.92) * mm, "end": v(-37.78, -89.98) * mm});
            skLineSegment(sketch, "E11.45.0", {"start": v(-28.74, -94) * mm, "end": v(-30.45, -94.87) * mm});
            skArc(sketch, "E11.45.1", {"start": v(-31.13, -94.65) * mm, "mid": v(-30.84, -94.9) * mm, "end": v(-30.45, -94.87) * mm});
            skLineSegment(sketch, "E11.45.2", {"start": v(-32, -92.93) * mm, "end": v(-31.13, -94.65) * mm});
            skArc(sketch, "E11.45.3", {"start": v(-32, -92.93) * mm, "mid": v(-32.1, -92.56) * mm, "end": v(-32.05, -92.17) * mm});
            skArc(sketch, "E11.45.4", {"start": v(-28.74, -94) * mm, "mid": v(-28.44, -93.75) * mm, "end": v(-28.25, -93.41) * mm});
            skLineSegment(sketch, "E11.45.5", {"start": v(-25.9, -86.2) * mm, "end": v(-28.25, -93.41) * mm});
            skLineSegment(sketch, "E11.45.6", {"start": v(-29.7, -84.96) * mm, "end": v(-32.05, -92.17) * mm});
            skLineSegment(sketch, "E11.46.0", {"start": v(-22.78, -95.6) * mm, "end": v(-24.44, -96.6) * mm});
            skArc(sketch, "E11.46.1", {"start": v(-25.12, -96.42) * mm, "mid": v(-24.82, -96.65) * mm, "end": v(-24.44, -96.6) * mm});
            skLineSegment(sketch, "E11.46.2", {"start": v(-26.1, -94.76) * mm, "end": v(-25.12, -96.42) * mm});
            skArc(sketch, "E11.46.3", {"start": v(-26.1, -94.76) * mm, "mid": v(-26.22, -94.4) * mm, "end": v(-26.2, -94) * mm});
            skArc(sketch, "E11.46.4", {"start": v(-22.78, -95.6) * mm, "mid": v(-22.5, -95.35) * mm, "end": v(-22.33, -95) * mm});
            skLineSegment(sketch, "E11.46.5", {"start": v(-20.44, -87.65) * mm, "end": v(-22.33, -95) * mm});
            skLineSegment(sketch, "E11.46.6", {"start": v(-24.31, -86.65) * mm, "end": v(-26.2, -94) * mm});
            skLineSegment(sketch, "E11.47.0", {"start": v(-16.73, -96.85) * mm, "end": v(-18.32, -97.94) * mm});
            skArc(sketch, "E11.47.1", {"start": v(-19.02, -97.8) * mm, "mid": v(-18.7, -98.02) * mm, "end": v(-18.32, -97.94) * mm});
            skLineSegment(sketch, "E11.47.2", {"start": v(-20.1, -96.21) * mm, "end": v(-19.02, -97.8) * mm});
            skArc(sketch, "E11.47.3", {"start": v(-20.1, -96.21) * mm, "mid": v(-20.24, -95.85) * mm, "end": v(-20.25, -95.47) * mm});
            skArc(sketch, "E11.47.4", {"start": v(-16.73, -96.85) * mm, "mid": v(-16.46, -96.57) * mm, "end": v(-16.32, -96.21) * mm});
            skLineSegment(sketch, "E11.47.5", {"start": v(-14.9, -88.76) * mm, "end": v(-16.32, -96.21) * mm});
            skLineSegment(sketch, "E11.47.6", {"start": v(-18.82, -88) * mm, "end": v(-20.25, -95.47) * mm});
            skLineSegment(sketch, "E11.48.0", {"start": v(-10.62, -97.71) * mm, "end": v(-12.14, -98.9) * mm});
            skArc(sketch, "E11.48.1", {"start": v(-12.84, -98.81) * mm, "mid": v(-12.5, -99) * mm, "end": v(-12.14, -98.9) * mm});
            skLineSegment(sketch, "E11.48.2", {"start": v(-14.01, -97.28) * mm, "end": v(-12.84, -98.81) * mm});
            skArc(sketch, "E11.48.3", {"start": v(-14.01, -97.28) * mm, "mid": v(-14.19, -96.94) * mm, "end": v(-14.21, -96.55) * mm});
            skArc(sketch, "E11.48.4", {"start": v(-10.62, -97.71) * mm, "mid": v(-10.37, -97.42) * mm, "end": v(-10.24, -97.05) * mm});
            skLineSegment(sketch, "E11.48.5", {"start": v(-9.3, -89.52) * mm, "end": v(-10.24, -97.05) * mm});
            skLineSegment(sketch, "E11.48.6", {"start": v(-13.26, -89.02) * mm, "end": v(-14.21, -96.55) * mm});
            skLineSegment(sketch, "E11.49.0", {"start": v(-4.46, -98.19) * mm, "end": v(-5.9, -99.47) * mm});
            skArc(sketch, "E11.49.1", {"start": v(-6.61, -99.42) * mm, "mid": v(-6.27, -99.6) * mm, "end": v(-5.9, -99.47) * mm});
            skLineSegment(sketch, "E11.49.2", {"start": v(-7.88, -97.97) * mm, "end": v(-6.61, -99.42) * mm});
            skArc(sketch, "E11.49.3", {"start": v(-7.88, -97.97) * mm, "mid": v(-8.07, -97.63) * mm, "end": v(-8.12, -97.25) * mm});
            skArc(sketch, "E11.49.4", {"start": v(-4.46, -98.19) * mm, "mid": v(-4.23, -97.88) * mm, "end": v(-4.13, -97.5) * mm});
            skLineSegment(sketch, "E11.49.5", {"start": v(-3.65, -89.93) * mm, "end": v(-4.13, -97.5) * mm});
            skLineSegment(sketch, "E11.49.6", {"start": v(-7.65, -89.67) * mm, "end": v(-8.12, -97.25) * mm});
            skLineSegment(sketch, "E11.50.0", {"start": v(1.71, -98.27) * mm, "end": v(0.36, -99.64) * mm});
            skArc(sketch, "E11.50.1", {"start": v(-0.36, -99.64) * mm, "mid": v(0, -99.79) * mm, "end": v(0.36, -99.64) * mm});
            skLineSegment(sketch, "E11.50.2", {"start": v(-1.71, -98.27) * mm, "end": v(-0.36, -99.64) * mm});
            skArc(sketch, "E11.50.3", {"start": v(-1.71, -98.27) * mm, "mid": v(-1.92, -97.95) * mm, "end": v(-2, -97.57) * mm});
            skArc(sketch, "E11.50.4", {"start": v(1.71, -98.27) * mm, "mid": v(1.92, -97.95) * mm, "end": v(2, -97.57) * mm});
            skLineSegment(sketch, "E11.50.5", {"start": v(2, -89.98) * mm, "end": v(2, -97.57) * mm});
            skLineSegment(sketch, "E11.50.6", {"start": v(-2, -89.98) * mm, "end": v(-2, -97.57) * mm});
            skLineSegment(sketch, "E11.51.0", {"start": v(7.88, -97.97) * mm, "end": v(6.61, -99.42) * mm});
            skArc(sketch, "E11.51.1", {"start": v(5.9, -99.47) * mm, "mid": v(6.27, -99.6) * mm, "end": v(6.61, -99.42) * mm});
            skLineSegment(sketch, "E11.51.2", {"start": v(4.46, -98.19) * mm, "end": v(5.9, -99.47) * mm});
            skArc(sketch, "E11.51.3", {"start": v(4.46, -98.19) * mm, "mid": v(4.23, -97.88) * mm, "end": v(4.13, -97.5) * mm});
            skArc(sketch, "E11.51.4", {"start": v(7.88, -97.97) * mm, "mid": v(8.07, -97.63) * mm, "end": v(8.12, -97.25) * mm});
            skLineSegment(sketch, "E11.51.5", {"start": v(7.65, -89.67) * mm, "end": v(8.12, -97.25) * mm});
            skLineSegment(sketch, "E11.51.6", {"start": v(3.65, -89.93) * mm, "end": v(4.13, -97.5) * mm});
            skLineSegment(sketch, "E11.52.0", {"start": v(14.01, -97.28) * mm, "end": v(12.84, -98.81) * mm});
            skArc(sketch, "E11.52.1", {"start": v(12.14, -98.9) * mm, "mid": v(12.5, -99) * mm, "end": v(12.84, -98.81) * mm});
            skLineSegment(sketch, "E11.52.2", {"start": v(10.62, -97.71) * mm, "end": v(12.14, -98.9) * mm});
            skArc(sketch, "E11.52.3", {"start": v(10.62, -97.71) * mm, "mid": v(10.37, -97.42) * mm, "end": v(10.24, -97.05) * mm});
            skArc(sketch, "E11.52.4", {"start": v(14.01, -97.28) * mm, "mid": v(14.19, -96.94) * mm, "end": v(14.21, -96.55) * mm});
            skLineSegment(sketch, "E11.52.5", {"start": v(13.26, -89.02) * mm, "end": v(14.21, -96.55) * mm});
            skLineSegment(sketch, "E11.52.6", {"start": v(9.3, -89.52) * mm, "end": v(10.24, -97.05) * mm});
            skLineSegment(sketch, "E11.53.0", {"start": v(20.1, -96.21) * mm, "end": v(19.02, -97.8) * mm});
            skArc(sketch, "E11.53.1", {"start": v(18.32, -97.94) * mm, "mid": v(18.7, -98.02) * mm, "end": v(19.02, -97.8) * mm});
            skLineSegment(sketch, "E11.53.2", {"start": v(16.73, -96.85) * mm, "end": v(18.32, -97.94) * mm});
            skArc(sketch, "E11.53.3", {"start": v(16.73, -96.85) * mm, "mid": v(16.46, -96.57) * mm, "end": v(16.32, -96.21) * mm});
            skArc(sketch, "E11.53.4", {"start": v(20.1, -96.21) * mm, "mid": v(20.24, -95.85) * mm, "end": v(20.25, -95.47) * mm});
            skLineSegment(sketch, "E11.53.5", {"start": v(18.82, -88) * mm, "end": v(20.25, -95.47) * mm});
            skLineSegment(sketch, "E11.53.6", {"start": v(14.9, -88.76) * mm, "end": v(16.32, -96.21) * mm});
            skLineSegment(sketch, "E11.54.0", {"start": v(26.1, -94.76) * mm, "end": v(25.12, -96.42) * mm});
            skArc(sketch, "E11.54.1", {"start": v(24.44, -96.6) * mm, "mid": v(24.82, -96.65) * mm, "end": v(25.12, -96.42) * mm});
            skLineSegment(sketch, "E11.54.2", {"start": v(22.78, -95.6) * mm, "end": v(24.44, -96.6) * mm});
            skArc(sketch, "E11.54.3", {"start": v(22.78, -95.6) * mm, "mid": v(22.5, -95.35) * mm, "end": v(22.33, -95) * mm});
            skArc(sketch, "E11.54.4", {"start": v(26.1, -94.76) * mm, "mid": v(26.22, -94.4) * mm, "end": v(26.2, -94) * mm});
            skLineSegment(sketch, "E11.54.5", {"start": v(24.31, -86.65) * mm, "end": v(26.2, -94) * mm});
            skLineSegment(sketch, "E11.54.6", {"start": v(20.44, -87.65) * mm, "end": v(22.33, -95) * mm});
            skLineSegment(sketch, "E11.55.0", {"start": v(32, -92.93) * mm, "end": v(31.13, -94.65) * mm});
            skArc(sketch, "E11.55.1", {"start": v(30.45, -94.87) * mm, "mid": v(30.84, -94.9) * mm, "end": v(31.13, -94.65) * mm});
            skLineSegment(sketch, "E11.55.2", {"start": v(28.74, -94) * mm, "end": v(30.45, -94.87) * mm});
            skArc(sketch, "E11.55.3", {"start": v(28.74, -94) * mm, "mid": v(28.44, -93.75) * mm, "end": v(28.25, -93.41) * mm});
            skArc(sketch, "E11.55.4", {"start": v(32, -92.93) * mm, "mid": v(32.1, -92.56) * mm, "end": v(32.05, -92.17) * mm});
            skLineSegment(sketch, "E11.55.5", {"start": v(29.7, -84.96) * mm, "end": v(32.05, -92.17) * mm});
            skLineSegment(sketch, "E11.55.6", {"start": v(25.9, -86.2) * mm, "end": v(28.25, -93.41) * mm});
            skLineSegment(sketch, "E11.56.0", {"start": v(37.77, -90.74) * mm, "end": v(37.01, -92.51) * mm});
            skArc(sketch, "E11.56.1", {"start": v(36.35, -92.77) * mm, "mid": v(36.73, -92.78) * mm, "end": v(37.01, -92.51) * mm});
            skLineSegment(sketch, "E11.56.2", {"start": v(34.59, -92) * mm, "end": v(36.35, -92.77) * mm});
            skArc(sketch, "E11.56.3", {"start": v(34.59, -92) * mm, "mid": v(34.27, -91.78) * mm, "end": v(34.06, -91.45) * mm});
            skArc(sketch, "E11.56.4", {"start": v(37.77, -90.74) * mm, "mid": v(37.85, -90.36) * mm, "end": v(37.78, -89.98) * mm});
            skLineSegment(sketch, "E11.56.5", {"start": v(34.98, -82.92) * mm, "end": v(37.78, -89.98) * mm});
            skLineSegment(sketch, "E11.56.6", {"start": v(31.26, -84.4) * mm, "end": v(34.06, -91.45) * mm});
            skLineSegment(sketch, "E11.57.0", {"start": v(43.39, -88.2) * mm, "end": v(42.75, -90) * mm});
            skArc(sketch, "E11.57.1", {"start": v(42.1, -90.3) * mm, "mid": v(42.49, -90.3) * mm, "end": v(42.75, -90) * mm});
            skLineSegment(sketch, "E11.57.2", {"start": v(40.3, -89.65) * mm, "end": v(42.1, -90.3) * mm});
            skArc(sketch, "E11.57.3", {"start": v(40.3, -89.65) * mm, "mid": v(39.96, -89.45) * mm, "end": v(39.73, -89.13) * mm});
            skArc(sketch, "E11.57.4", {"start": v(43.39, -88.2) * mm, "mid": v(43.45, -87.8) * mm, "end": v(43.35, -87.43) * mm});
            skLineSegment(sketch, "E11.57.5", {"start": v(40.12, -80.56) * mm, "end": v(43.35, -87.43) * mm});
            skLineSegment(sketch, "E11.57.6", {"start": v(36.5, -82.27) * mm, "end": v(39.73, -89.13) * mm});
            skLineSegment(sketch, "E11.58.0", {"start": v(48.84, -85.3) * mm, "end": v(48.31, -87.14) * mm});
            skArc(sketch, "E11.58.1", {"start": v(47.7, -87.49) * mm, "mid": v(48.07, -87.45) * mm, "end": v(48.31, -87.14) * mm});
            skLineSegment(sketch, "E11.58.2", {"start": v(45.84, -86.94) * mm, "end": v(47.7, -87.49) * mm});
            skArc(sketch, "E11.58.3", {"start": v(45.84, -86.94) * mm, "mid": v(45.5, -86.76) * mm, "end": v(45.25, -86.46) * mm});
            skArc(sketch, "E11.58.4", {"start": v(48.84, -85.3) * mm, "mid": v(48.87, -84.9) * mm, "end": v(48.76, -84.54) * mm});
            skLineSegment(sketch, "E11.58.5", {"start": v(45.1, -77.88) * mm, "end": v(48.76, -84.54) * mm});
            skLineSegment(sketch, "E11.58.6", {"start": v(41.6, -79.81) * mm, "end": v(45.25, -86.46) * mm});
            skLineSegment(sketch, "E11.59.0", {"start": v(54.1, -82.06) * mm, "end": v(53.7, -83.94) * mm});
            skArc(sketch, "E11.59.1", {"start": v(53.1, -84.32) * mm, "mid": v(53.47, -84.25) * mm, "end": v(53.7, -83.94) * mm});
            skLineSegment(sketch, "E11.59.2", {"start": v(51.21, -83.9) * mm, "end": v(53.1, -84.32) * mm});
            skArc(sketch, "E11.59.3", {"start": v(51.21, -83.9) * mm, "mid": v(50.86, -83.73) * mm, "end": v(50.6, -83.45) * mm});
            skArc(sketch, "E11.59.4", {"start": v(54.1, -82.06) * mm, "mid": v(54.1, -81.67) * mm, "end": v(53.97, -81.3) * mm});
            skLineSegment(sketch, "E11.59.5", {"start": v(49.9, -74.9) * mm, "end": v(53.97, -81.3) * mm});
            skLineSegment(sketch, "E11.59.6", {"start": v(46.52, -77.04) * mm, "end": v(50.6, -83.45) * mm});
            skLineSegment(sketch, "E11.60.0", {"start": v(59.15, -78.5) * mm, "end": v(58.86, -80.4) * mm});
            skArc(sketch, "E11.60.1", {"start": v(58.28, -80.82) * mm, "mid": v(58.65, -80.73) * mm, "end": v(58.86, -80.4) * mm});
            skLineSegment(sketch, "E11.60.2", {"start": v(56.38, -80.5) * mm, "end": v(58.28, -80.82) * mm});
            skArc(sketch, "E11.60.3", {"start": v(56.38, -80.5) * mm, "mid": v(56.02, -80.37) * mm, "end": v(55.73, -80.11) * mm});
            skArc(sketch, "E11.60.4", {"start": v(59.15, -78.5) * mm, "mid": v(59.13, -78.11) * mm, "end": v(58.97, -77.76) * mm});
            skLineSegment(sketch, "E11.60.5", {"start": v(54.5, -71.62) * mm, "end": v(58.97, -77.76) * mm});
            skLineSegment(sketch, "E11.60.6", {"start": v(51.27, -73.97) * mm, "end": v(55.73, -80.11) * mm});
            skLineSegment(sketch, "E11.61.0", {"start": v(63.96, -74.63) * mm, "end": v(63.79, -76.55) * mm});
            skArc(sketch, "E11.61.1", {"start": v(63.24, -77) * mm, "mid": v(63.6, -76.89) * mm, "end": v(63.79, -76.55) * mm});
            skLineSegment(sketch, "E11.61.2", {"start": v(61.32, -76.81) * mm, "end": v(63.24, -77) * mm});
            skArc(sketch, "E11.61.3", {"start": v(61.32, -76.81) * mm, "mid": v(60.95, -76.7) * mm, "end": v(60.65, -76.45) * mm});
            skArc(sketch, "E11.61.4", {"start": v(63.96, -74.63) * mm, "mid": v(63.92, -74.24) * mm, "end": v(63.73, -73.9) * mm});
            skLineSegment(sketch, "E11.61.5", {"start": v(58.9, -68.05) * mm, "end": v(63.73, -73.9) * mm});
            skLineSegment(sketch, "E11.61.6", {"start": v(55.81, -70.6) * mm, "end": v(60.65, -76.45) * mm});
            skLineSegment(sketch, "E11.62.0", {"start": v(68.52, -70.47) * mm, "end": v(68.47, -72.4) * mm});
            skArc(sketch, "E11.62.1", {"start": v(67.95, -72.88) * mm, "mid": v(68.31, -72.74) * mm, "end": v(68.47, -72.4) * mm});
            skLineSegment(sketch, "E11.62.2", {"start": v(66.02, -72.8) * mm, "end": v(67.95, -72.88) * mm});
            skArc(sketch, "E11.62.3", {"start": v(66.02, -72.8) * mm, "mid": v(65.65, -72.72) * mm, "end": v(65.33, -72.5) * mm});
            skArc(sketch, "E11.62.4", {"start": v(68.52, -70.47) * mm, "mid": v(68.45, -70.08) * mm, "end": v(68.25, -69.76) * mm});
            skLineSegment(sketch, "E11.62.5", {"start": v(63.05, -64.22) * mm, "end": v(68.25, -69.76) * mm});
            skLineSegment(sketch, "E11.62.6", {"start": v(60.14, -66.96) * mm, "end": v(65.33, -72.5) * mm});
            skLineSegment(sketch, "E11.63.0", {"start": v(72.8, -66.02) * mm, "end": v(72.88, -67.95) * mm});
            skArc(sketch, "E11.63.1", {"start": v(72.4, -68.47) * mm, "mid": v(72.74, -68.31) * mm, "end": v(72.88, -67.95) * mm});
            skLineSegment(sketch, "E11.63.2", {"start": v(70.47, -68.52) * mm, "end": v(72.4, -68.47) * mm});
            skArc(sketch, "E11.63.3", {"start": v(70.47, -68.52) * mm, "mid": v(70.08, -68.45) * mm, "end": v(69.76, -68.25) * mm});
            skArc(sketch, "E11.63.4", {"start": v(72.8, -66.02) * mm, "mid": v(72.72, -65.65) * mm, "end": v(72.5, -65.33) * mm});
            skLineSegment(sketch, "E11.63.5", {"start": v(66.96, -60.14) * mm, "end": v(72.5, -65.33) * mm});
            skLineSegment(sketch, "E11.63.6", {"start": v(64.22, -63.05) * mm, "end": v(69.76, -68.25) * mm});
            skLineSegment(sketch, "E11.64.0", {"start": v(76.81, -61.32) * mm, "end": v(77, -63.24) * mm});
            skArc(sketch, "E11.64.1", {"start": v(76.55, -63.79) * mm, "mid": v(76.89, -63.6) * mm, "end": v(77, -63.24) * mm});
            skLineSegment(sketch, "E11.64.2", {"start": v(74.63, -63.96) * mm, "end": v(76.55, -63.79) * mm});
            skArc(sketch, "E11.64.3", {"start": v(74.63, -63.96) * mm, "mid": v(74.24, -63.92) * mm, "end": v(73.9, -63.73) * mm});
            skArc(sketch, "E11.64.4", {"start": v(76.81, -61.32) * mm, "mid": v(76.7, -60.95) * mm, "end": v(76.45, -60.65) * mm});
            skLineSegment(sketch, "E11.64.5", {"start": v(70.6, -55.81) * mm, "end": v(76.45, -60.65) * mm});
            skLineSegment(sketch, "E11.64.6", {"start": v(68.05, -58.9) * mm, "end": v(73.9, -63.73) * mm});
            skLineSegment(sketch, "E11.65.0", {"start": v(80.5, -56.38) * mm, "end": v(80.82, -58.28) * mm});
            skArc(sketch, "E11.65.1", {"start": v(80.4, -58.86) * mm, "mid": v(80.73, -58.65) * mm, "end": v(80.82, -58.28) * mm});
            skLineSegment(sketch, "E11.65.2", {"start": v(78.5, -59.15) * mm, "end": v(80.4, -58.86) * mm});
            skArc(sketch, "E11.65.3", {"start": v(78.5, -59.15) * mm, "mid": v(78.11, -59.13) * mm, "end": v(77.76, -58.97) * mm});
            skArc(sketch, "E11.65.4", {"start": v(80.5, -56.38) * mm, "mid": v(80.37, -56.02) * mm, "end": v(80.11, -55.73) * mm});
            skLineSegment(sketch, "E11.65.5", {"start": v(73.97, -51.27) * mm, "end": v(80.11, -55.73) * mm});
            skLineSegment(sketch, "E11.65.6", {"start": v(71.62, -54.5) * mm, "end": v(77.76, -58.97) * mm});
            skLineSegment(sketch, "E11.66.0", {"start": v(83.9, -51.21) * mm, "end": v(84.32, -53.1) * mm});
            skArc(sketch, "E11.66.1", {"start": v(83.94, -53.7) * mm, "mid": v(84.25, -53.47) * mm, "end": v(84.32, -53.1) * mm});
            skLineSegment(sketch, "E11.66.2", {"start": v(82.06, -54.1) * mm, "end": v(83.94, -53.7) * mm});
            skArc(sketch, "E11.66.3", {"start": v(82.06, -54.1) * mm, "mid": v(81.67, -54.1) * mm, "end": v(81.3, -53.97) * mm});
            skArc(sketch, "E11.66.4", {"start": v(83.9, -51.21) * mm, "mid": v(83.73, -50.86) * mm, "end": v(83.45, -50.6) * mm});
            skLineSegment(sketch, "E11.66.5", {"start": v(77.04, -46.52) * mm, "end": v(83.45, -50.6) * mm});
            skLineSegment(sketch, "E11.66.6", {"start": v(74.9, -49.9) * mm, "end": v(81.3, -53.97) * mm});
            skLineSegment(sketch, "E11.67.0", {"start": v(86.94, -45.84) * mm, "end": v(87.49, -47.7) * mm});
            skArc(sketch, "E11.67.1", {"start": v(87.14, -48.31) * mm, "mid": v(87.45, -48.07) * mm, "end": v(87.49, -47.7) * mm});
            skLineSegment(sketch, "E11.67.2", {"start": v(85.3, -48.84) * mm, "end": v(87.14, -48.31) * mm});
            skArc(sketch, "E11.67.3", {"start": v(85.3, -48.84) * mm, "mid": v(84.9, -48.87) * mm, "end": v(84.54, -48.76) * mm});
            skArc(sketch, "E11.67.4", {"start": v(86.94, -45.84) * mm, "mid": v(86.76, -45.5) * mm, "end": v(86.46, -45.25) * mm});
            skLineSegment(sketch, "E11.67.5", {"start": v(79.81, -41.6) * mm, "end": v(86.46, -45.25) * mm});
            skLineSegment(sketch, "E11.67.6", {"start": v(77.88, -45.1) * mm, "end": v(84.54, -48.76) * mm});
            skLineSegment(sketch, "E11.68.0", {"start": v(89.65, -40.3) * mm, "end": v(90.3, -42.1) * mm});
            skArc(sketch, "E11.68.1", {"start": v(90, -42.75) * mm, "mid": v(90.3, -42.49) * mm, "end": v(90.3, -42.1) * mm});
            skLineSegment(sketch, "E11.68.2", {"start": v(88.2, -43.39) * mm, "end": v(90, -42.75) * mm});
            skArc(sketch, "E11.68.3", {"start": v(88.2, -43.39) * mm, "mid": v(87.8, -43.45) * mm, "end": v(87.43, -43.35) * mm});
            skArc(sketch, "E11.68.4", {"start": v(89.65, -40.3) * mm, "mid": v(89.45, -39.96) * mm, "end": v(89.13, -39.73) * mm});
            skLineSegment(sketch, "E11.68.5", {"start": v(82.27, -36.5) * mm, "end": v(89.13, -39.73) * mm});
            skLineSegment(sketch, "E11.68.6", {"start": v(80.56, -40.12) * mm, "end": v(87.43, -43.35) * mm});
            skLineSegment(sketch, "E11.69.0", {"start": v(92, -34.59) * mm, "end": v(92.77, -36.35) * mm});
            skArc(sketch, "E11.69.1", {"start": v(92.51, -37.01) * mm, "mid": v(92.78, -36.73) * mm, "end": v(92.77, -36.35) * mm});
            skLineSegment(sketch, "E11.69.2", {"start": v(90.74, -37.77) * mm, "end": v(92.51, -37.01) * mm});
            skArc(sketch, "E11.69.3", {"start": v(90.74, -37.77) * mm, "mid": v(90.36, -37.85) * mm, "end": v(89.98, -37.78) * mm});
            skArc(sketch, "E11.69.4", {"start": v(92, -34.59) * mm, "mid": v(91.78, -34.27) * mm, "end": v(91.45, -34.06) * mm});
            skLineSegment(sketch, "E11.69.5", {"start": v(84.4, -31.26) * mm, "end": v(91.45, -34.06) * mm});
            skLineSegment(sketch, "E11.69.6", {"start": v(82.92, -34.98) * mm, "end": v(89.98, -37.78) * mm});
            skLineSegment(sketch, "E11.70.0", {"start": v(94, -28.74) * mm, "end": v(94.87, -30.45) * mm});
            skArc(sketch, "E11.70.1", {"start": v(94.65, -31.13) * mm, "mid": v(94.9, -30.84) * mm, "end": v(94.87, -30.45) * mm});
            skLineSegment(sketch, "E11.70.2", {"start": v(92.93, -32) * mm, "end": v(94.65, -31.13) * mm});
            skArc(sketch, "E11.70.3", {"start": v(92.93, -32) * mm, "mid": v(92.56, -32.1) * mm, "end": v(92.17, -32.05) * mm});
            skArc(sketch, "E11.70.4", {"start": v(94, -28.74) * mm, "mid": v(93.75, -28.44) * mm, "end": v(93.41, -28.25) * mm});
            skLineSegment(sketch, "E11.70.5", {"start": v(86.2, -25.9) * mm, "end": v(93.41, -28.25) * mm});
            skLineSegment(sketch, "E11.70.6", {"start": v(84.96, -29.7) * mm, "end": v(92.17, -32.05) * mm});
            skLineSegment(sketch, "E11.71.0", {"start": v(95.6, -22.78) * mm, "end": v(96.6, -24.44) * mm});
            skArc(sketch, "E11.71.1", {"start": v(96.42, -25.12) * mm, "mid": v(96.65, -24.82) * mm, "end": v(96.6, -24.44) * mm});
            skLineSegment(sketch, "E11.71.2", {"start": v(94.76, -26.1) * mm, "end": v(96.42, -25.12) * mm});
            skArc(sketch, "E11.71.3", {"start": v(94.76, -26.1) * mm, "mid": v(94.4, -26.22) * mm, "end": v(94, -26.2) * mm});
            skArc(sketch, "E11.71.4", {"start": v(95.6, -22.78) * mm, "mid": v(95.35, -22.5) * mm, "end": v(95, -22.33) * mm});
            skLineSegment(sketch, "E11.71.5", {"start": v(87.65, -20.44) * mm, "end": v(95, -22.33) * mm});
            skLineSegment(sketch, "E11.71.6", {"start": v(86.65, -24.31) * mm, "end": v(94, -26.2) * mm});
            skLineSegment(sketch, "E11.72.0", {"start": v(96.85, -16.73) * mm, "end": v(97.94, -18.32) * mm});
            skArc(sketch, "E11.72.1", {"start": v(97.8, -19.02) * mm, "mid": v(98.02, -18.7) * mm, "end": v(97.94, -18.32) * mm});
            skLineSegment(sketch, "E11.72.2", {"start": v(96.21, -20.1) * mm, "end": v(97.8, -19.02) * mm});
            skArc(sketch, "E11.72.3", {"start": v(96.21, -20.1) * mm, "mid": v(95.85, -20.24) * mm, "end": v(95.47, -20.25) * mm});
            skArc(sketch, "E11.72.4", {"start": v(96.85, -16.73) * mm, "mid": v(96.57, -16.46) * mm, "end": v(96.21, -16.32) * mm});
            skLineSegment(sketch, "E11.72.5", {"start": v(88.76, -14.9) * mm, "end": v(96.21, -16.32) * mm});
            skLineSegment(sketch, "E11.72.6", {"start": v(88, -18.82) * mm, "end": v(95.47, -20.25) * mm});
            skLineSegment(sketch, "E11.73.0", {"start": v(97.71, -10.62) * mm, "end": v(98.9, -12.14) * mm});
            skArc(sketch, "E11.73.1", {"start": v(98.81, -12.84) * mm, "mid": v(99, -12.5) * mm, "end": v(98.9, -12.14) * mm});
            skLineSegment(sketch, "E11.73.2", {"start": v(97.28, -14.01) * mm, "end": v(98.81, -12.84) * mm});
            skArc(sketch, "E11.73.3", {"start": v(97.28, -14.01) * mm, "mid": v(96.94, -14.19) * mm, "end": v(96.55, -14.21) * mm});
            skArc(sketch, "E11.73.4", {"start": v(97.71, -10.62) * mm, "mid": v(97.42, -10.37) * mm, "end": v(97.05, -10.24) * mm});
            skLineSegment(sketch, "E11.73.5", {"start": v(89.52, -9.3) * mm, "end": v(97.05, -10.24) * mm});
            skLineSegment(sketch, "E11.73.6", {"start": v(89.02, -13.26) * mm, "end": v(96.55, -14.21) * mm});
            skLineSegment(sketch, "E11.74.0", {"start": v(98.19, -4.46) * mm, "end": v(99.47, -5.9) * mm});
            skArc(sketch, "E11.74.1", {"start": v(99.42, -6.61) * mm, "mid": v(99.6, -6.27) * mm, "end": v(99.47, -5.9) * mm});
            skLineSegment(sketch, "E11.74.2", {"start": v(97.97, -7.88) * mm, "end": v(99.42, -6.61) * mm});
            skArc(sketch, "E11.74.3", {"start": v(97.97, -7.88) * mm, "mid": v(97.63, -8.07) * mm, "end": v(97.25, -8.12) * mm});
            skArc(sketch, "E11.74.4", {"start": v(98.19, -4.46) * mm, "mid": v(97.88, -4.23) * mm, "end": v(97.5, -4.13) * mm});
            skLineSegment(sketch, "E11.74.5", {"start": v(89.93, -3.65) * mm, "end": v(97.5, -4.13) * mm});
            skLineSegment(sketch, "E11.74.6", {"start": v(89.67, -7.65) * mm, "end": v(97.25, -8.12) * mm});
            skLineSegment(sketch, "E11.75.0", {"start": v(98.27, 1.71) * mm, "end": v(99.64, 0.36) * mm});
            skArc(sketch, "E11.75.1", {"start": v(99.64, -0.36) * mm, "mid": v(99.79, 0) * mm, "end": v(99.64, 0.36) * mm});
            skLineSegment(sketch, "E11.75.2", {"start": v(98.27, -1.71) * mm, "end": v(99.64, -0.36) * mm});
            skArc(sketch, "E11.75.3", {"start": v(98.27, -1.71) * mm, "mid": v(97.95, -1.92) * mm, "end": v(97.57, -2) * mm});
            skArc(sketch, "E11.75.4", {"start": v(98.27, 1.71) * mm, "mid": v(97.95, 1.92) * mm, "end": v(97.57, 2) * mm});
            skLineSegment(sketch, "E11.75.5", {"start": v(89.98, 2) * mm, "end": v(97.57, 2) * mm});
            skLineSegment(sketch, "E11.75.6", {"start": v(89.98, -2) * mm, "end": v(97.57, -2) * mm});
            skLineSegment(sketch, "E11.76.0", {"start": v(97.97, 7.88) * mm, "end": v(99.42, 6.61) * mm});
            skArc(sketch, "E11.76.1", {"start": v(99.47, 5.9) * mm, "mid": v(99.6, 6.27) * mm, "end": v(99.42, 6.61) * mm});
            skLineSegment(sketch, "E11.76.2", {"start": v(98.19, 4.46) * mm, "end": v(99.47, 5.9) * mm});
            skArc(sketch, "E11.76.3", {"start": v(98.19, 4.46) * mm, "mid": v(97.88, 4.23) * mm, "end": v(97.5, 4.13) * mm});
            skArc(sketch, "E11.76.4", {"start": v(97.97, 7.88) * mm, "mid": v(97.63, 8.07) * mm, "end": v(97.25, 8.12) * mm});
            skLineSegment(sketch, "E11.76.5", {"start": v(89.67, 7.65) * mm, "end": v(97.25, 8.12) * mm});
            skLineSegment(sketch, "E11.76.6", {"start": v(89.93, 3.65) * mm, "end": v(97.5, 4.13) * mm});
            skLineSegment(sketch, "E11.77.0", {"start": v(97.28, 14.01) * mm, "end": v(98.81, 12.84) * mm});
            skArc(sketch, "E11.77.1", {"start": v(98.9, 12.14) * mm, "mid": v(99, 12.5) * mm, "end": v(98.81, 12.84) * mm});
            skLineSegment(sketch, "E11.77.2", {"start": v(97.71, 10.62) * mm, "end": v(98.9, 12.14) * mm});
            skArc(sketch, "E11.77.3", {"start": v(97.71, 10.62) * mm, "mid": v(97.42, 10.37) * mm, "end": v(97.05, 10.24) * mm});
            skArc(sketch, "E11.77.4", {"start": v(97.28, 14.01) * mm, "mid": v(96.94, 14.19) * mm, "end": v(96.55, 14.21) * mm});
            skLineSegment(sketch, "E11.77.5", {"start": v(89.02, 13.26) * mm, "end": v(96.55, 14.21) * mm});
            skLineSegment(sketch, "E11.77.6", {"start": v(89.52, 9.3) * mm, "end": v(97.05, 10.24) * mm});
            skLineSegment(sketch, "E11.78.0", {"start": v(96.21, 20.1) * mm, "end": v(97.8, 19.02) * mm});
            skArc(sketch, "E11.78.1", {"start": v(97.94, 18.32) * mm, "mid": v(98.02, 18.7) * mm, "end": v(97.8, 19.02) * mm});
            skLineSegment(sketch, "E11.78.2", {"start": v(96.85, 16.73) * mm, "end": v(97.94, 18.32) * mm});
            skArc(sketch, "E11.78.3", {"start": v(96.85, 16.73) * mm, "mid": v(96.57, 16.46) * mm, "end": v(96.21, 16.32) * mm});
            skArc(sketch, "E11.78.4", {"start": v(96.21, 20.1) * mm, "mid": v(95.85, 20.24) * mm, "end": v(95.47, 20.25) * mm});
            skLineSegment(sketch, "E11.78.5", {"start": v(88, 18.82) * mm, "end": v(95.47, 20.25) * mm});
            skLineSegment(sketch, "E11.78.6", {"start": v(88.76, 14.9) * mm, "end": v(96.21, 16.32) * mm});
            skLineSegment(sketch, "E11.79.0", {"start": v(94.76, 26.1) * mm, "end": v(96.42, 25.12) * mm});
            skArc(sketch, "E11.79.1", {"start": v(96.6, 24.44) * mm, "mid": v(96.65, 24.82) * mm, "end": v(96.42, 25.12) * mm});
            skLineSegment(sketch, "E11.79.2", {"start": v(95.6, 22.78) * mm, "end": v(96.6, 24.44) * mm});
            skArc(sketch, "E11.79.3", {"start": v(95.6, 22.78) * mm, "mid": v(95.35, 22.5) * mm, "end": v(95, 22.33) * mm});
            skArc(sketch, "E11.79.4", {"start": v(94.76, 26.1) * mm, "mid": v(94.4, 26.22) * mm, "end": v(94, 26.2) * mm});
            skLineSegment(sketch, "E11.79.5", {"start": v(86.65, 24.31) * mm, "end": v(94, 26.2) * mm});
            skLineSegment(sketch, "E11.79.6", {"start": v(87.65, 20.44) * mm, "end": v(95, 22.33) * mm});
            skLineSegment(sketch, "E11.80.0", {"start": v(92.93, 32) * mm, "end": v(94.65, 31.13) * mm});
            skArc(sketch, "E11.80.1", {"start": v(94.87, 30.45) * mm, "mid": v(94.9, 30.84) * mm, "end": v(94.65, 31.13) * mm});
            skLineSegment(sketch, "E11.80.2", {"start": v(94, 28.74) * mm, "end": v(94.87, 30.45) * mm});
            skArc(sketch, "E11.80.3", {"start": v(94, 28.74) * mm, "mid": v(93.75, 28.44) * mm, "end": v(93.41, 28.25) * mm});
            skArc(sketch, "E11.80.4", {"start": v(92.93, 32) * mm, "mid": v(92.56, 32.1) * mm, "end": v(92.17, 32.05) * mm});
            skLineSegment(sketch, "E11.80.5", {"start": v(84.96, 29.7) * mm, "end": v(92.17, 32.05) * mm});
            skLineSegment(sketch, "E11.80.6", {"start": v(86.2, 25.9) * mm, "end": v(93.41, 28.25) * mm});
            skLineSegment(sketch, "E11.81.0", {"start": v(90.74, 37.77) * mm, "end": v(92.51, 37.01) * mm});
            skArc(sketch, "E11.81.1", {"start": v(92.77, 36.35) * mm, "mid": v(92.78, 36.73) * mm, "end": v(92.51, 37.01) * mm});
            skLineSegment(sketch, "E11.81.2", {"start": v(92, 34.59) * mm, "end": v(92.77, 36.35) * mm});
            skArc(sketch, "E11.81.3", {"start": v(92, 34.59) * mm, "mid": v(91.78, 34.27) * mm, "end": v(91.45, 34.06) * mm});
            skArc(sketch, "E11.81.4", {"start": v(90.74, 37.77) * mm, "mid": v(90.36, 37.85) * mm, "end": v(89.98, 37.78) * mm});
            skLineSegment(sketch, "E11.81.5", {"start": v(82.92, 34.98) * mm, "end": v(89.98, 37.78) * mm});
            skLineSegment(sketch, "E11.81.6", {"start": v(84.4, 31.26) * mm, "end": v(91.45, 34.06) * mm});
            skLineSegment(sketch, "E11.82.0", {"start": v(88.2, 43.39) * mm, "end": v(90, 42.75) * mm});
            skArc(sketch, "E11.82.1", {"start": v(90.3, 42.1) * mm, "mid": v(90.3, 42.49) * mm, "end": v(90, 42.75) * mm});
            skLineSegment(sketch, "E11.82.2", {"start": v(89.65, 40.3) * mm, "end": v(90.3, 42.1) * mm});
            skArc(sketch, "E11.82.3", {"start": v(89.65, 40.3) * mm, "mid": v(89.45, 39.96) * mm, "end": v(89.13, 39.73) * mm});
            skArc(sketch, "E11.82.4", {"start": v(88.2, 43.39) * mm, "mid": v(87.8, 43.45) * mm, "end": v(87.43, 43.35) * mm});
            skLineSegment(sketch, "E11.82.5", {"start": v(80.56, 40.12) * mm, "end": v(87.43, 43.35) * mm});
            skLineSegment(sketch, "E11.82.6", {"start": v(82.27, 36.5) * mm, "end": v(89.13, 39.73) * mm});
            skLineSegment(sketch, "E11.83.0", {"start": v(85.3, 48.84) * mm, "end": v(87.14, 48.31) * mm});
            skArc(sketch, "E11.83.1", {"start": v(87.49, 47.7) * mm, "mid": v(87.45, 48.07) * mm, "end": v(87.14, 48.31) * mm});
            skLineSegment(sketch, "E11.83.2", {"start": v(86.94, 45.84) * mm, "end": v(87.49, 47.7) * mm});
            skArc(sketch, "E11.83.3", {"start": v(86.94, 45.84) * mm, "mid": v(86.76, 45.5) * mm, "end": v(86.46, 45.25) * mm});
            skArc(sketch, "E11.83.4", {"start": v(85.3, 48.84) * mm, "mid": v(84.9, 48.87) * mm, "end": v(84.54, 48.76) * mm});
            skLineSegment(sketch, "E11.83.5", {"start": v(77.88, 45.1) * mm, "end": v(84.54, 48.76) * mm});
            skLineSegment(sketch, "E11.83.6", {"start": v(79.81, 41.6) * mm, "end": v(86.46, 45.25) * mm});
            skLineSegment(sketch, "E11.84.0", {"start": v(82.06, 54.1) * mm, "end": v(83.94, 53.7) * mm});
            skArc(sketch, "E11.84.1", {"start": v(84.32, 53.1) * mm, "mid": v(84.25, 53.47) * mm, "end": v(83.94, 53.7) * mm});
            skLineSegment(sketch, "E11.84.2", {"start": v(83.9, 51.21) * mm, "end": v(84.32, 53.1) * mm});
            skArc(sketch, "E11.84.3", {"start": v(83.9, 51.21) * mm, "mid": v(83.73, 50.86) * mm, "end": v(83.45, 50.6) * mm});
            skArc(sketch, "E11.84.4", {"start": v(82.06, 54.1) * mm, "mid": v(81.67, 54.1) * mm, "end": v(81.3, 53.97) * mm});
            skLineSegment(sketch, "E11.84.5", {"start": v(74.9, 49.9) * mm, "end": v(81.3, 53.97) * mm});
            skLineSegment(sketch, "E11.84.6", {"start": v(77.04, 46.52) * mm, "end": v(83.45, 50.6) * mm});
            skLineSegment(sketch, "E11.85.0", {"start": v(78.5, 59.15) * mm, "end": v(80.4, 58.86) * mm});
            skArc(sketch, "E11.85.1", {"start": v(80.82, 58.28) * mm, "mid": v(80.73, 58.65) * mm, "end": v(80.4, 58.86) * mm});
            skLineSegment(sketch, "E11.85.2", {"start": v(80.5, 56.38) * mm, "end": v(80.82, 58.28) * mm});
            skArc(sketch, "E11.85.3", {"start": v(80.5, 56.38) * mm, "mid": v(80.37, 56.02) * mm, "end": v(80.11, 55.73) * mm});
            skArc(sketch, "E11.85.4", {"start": v(78.5, 59.15) * mm, "mid": v(78.11, 59.13) * mm, "end": v(77.76, 58.97) * mm});
            skLineSegment(sketch, "E11.85.5", {"start": v(71.62, 54.5) * mm, "end": v(77.76, 58.97) * mm});
            skLineSegment(sketch, "E11.85.6", {"start": v(73.97, 51.27) * mm, "end": v(80.11, 55.73) * mm});
            skLineSegment(sketch, "E11.86.0", {"start": v(74.63, 63.96) * mm, "end": v(76.55, 63.79) * mm});
            skArc(sketch, "E11.86.1", {"start": v(77, 63.24) * mm, "mid": v(76.89, 63.6) * mm, "end": v(76.55, 63.79) * mm});
            skLineSegment(sketch, "E11.86.2", {"start": v(76.81, 61.32) * mm, "end": v(77, 63.24) * mm});
            skArc(sketch, "E11.86.3", {"start": v(76.81, 61.32) * mm, "mid": v(76.7, 60.95) * mm, "end": v(76.45, 60.65) * mm});
            skArc(sketch, "E11.86.4", {"start": v(74.63, 63.96) * mm, "mid": v(74.24, 63.92) * mm, "end": v(73.9, 63.73) * mm});
            skLineSegment(sketch, "E11.86.5", {"start": v(68.05, 58.9) * mm, "end": v(73.9, 63.73) * mm});
            skLineSegment(sketch, "E11.86.6", {"start": v(70.6, 55.81) * mm, "end": v(76.45, 60.65) * mm});
            skLineSegment(sketch, "E11.87.0", {"start": v(70.47, 68.52) * mm, "end": v(72.4, 68.47) * mm});
            skArc(sketch, "E11.87.1", {"start": v(72.88, 67.95) * mm, "mid": v(72.74, 68.31) * mm, "end": v(72.4, 68.47) * mm});
            skLineSegment(sketch, "E11.87.2", {"start": v(72.8, 66.02) * mm, "end": v(72.88, 67.95) * mm});
            skArc(sketch, "E11.87.3", {"start": v(72.8, 66.02) * mm, "mid": v(72.72, 65.65) * mm, "end": v(72.5, 65.33) * mm});
            skArc(sketch, "E11.87.4", {"start": v(70.47, 68.52) * mm, "mid": v(70.08, 68.45) * mm, "end": v(69.76, 68.25) * mm});
            skLineSegment(sketch, "E11.87.5", {"start": v(64.22, 63.05) * mm, "end": v(69.76, 68.25) * mm});
            skLineSegment(sketch, "E11.87.6", {"start": v(66.96, 60.14) * mm, "end": v(72.5, 65.33) * mm});
            skLineSegment(sketch, "E11.88.0", {"start": v(66.02, 72.8) * mm, "end": v(67.95, 72.88) * mm});
            skArc(sketch, "E11.88.1", {"start": v(68.47, 72.4) * mm, "mid": v(68.31, 72.74) * mm, "end": v(67.95, 72.88) * mm});
            skLineSegment(sketch, "E11.88.2", {"start": v(68.52, 70.47) * mm, "end": v(68.47, 72.4) * mm});
            skArc(sketch, "E11.88.3", {"start": v(68.52, 70.47) * mm, "mid": v(68.45, 70.08) * mm, "end": v(68.25, 69.76) * mm});
            skArc(sketch, "E11.88.4", {"start": v(66.02, 72.8) * mm, "mid": v(65.65, 72.72) * mm, "end": v(65.33, 72.5) * mm});
            skLineSegment(sketch, "E11.88.5", {"start": v(60.14, 66.96) * mm, "end": v(65.33, 72.5) * mm});
            skLineSegment(sketch, "E11.88.6", {"start": v(63.05, 64.22) * mm, "end": v(68.25, 69.76) * mm});
            skLineSegment(sketch, "E11.89.0", {"start": v(61.32, 76.81) * mm, "end": v(63.24, 77) * mm});
            skArc(sketch, "E11.89.1", {"start": v(63.79, 76.55) * mm, "mid": v(63.6, 76.89) * mm, "end": v(63.24, 77) * mm});
            skLineSegment(sketch, "E11.89.2", {"start": v(63.96, 74.63) * mm, "end": v(63.79, 76.55) * mm});
            skArc(sketch, "E11.89.3", {"start": v(63.96, 74.63) * mm, "mid": v(63.92, 74.24) * mm, "end": v(63.73, 73.9) * mm});
            skArc(sketch, "E11.89.4", {"start": v(61.32, 76.81) * mm, "mid": v(60.95, 76.7) * mm, "end": v(60.65, 76.45) * mm});
            skLineSegment(sketch, "E11.89.5", {"start": v(55.81, 70.6) * mm, "end": v(60.65, 76.45) * mm});
            skLineSegment(sketch, "E11.89.6", {"start": v(58.9, 68.05) * mm, "end": v(63.73, 73.9) * mm});
            skLineSegment(sketch, "E11.90.0", {"start": v(56.38, 80.5) * mm, "end": v(58.28, 80.82) * mm});
            skArc(sketch, "E11.90.1", {"start": v(58.86, 80.4) * mm, "mid": v(58.65, 80.73) * mm, "end": v(58.28, 80.82) * mm});
            skLineSegment(sketch, "E11.90.2", {"start": v(59.15, 78.5) * mm, "end": v(58.86, 80.4) * mm});
            skArc(sketch, "E11.90.3", {"start": v(59.15, 78.5) * mm, "mid": v(59.13, 78.11) * mm, "end": v(58.97, 77.76) * mm});
            skArc(sketch, "E11.90.4", {"start": v(56.38, 80.5) * mm, "mid": v(56.02, 80.37) * mm, "end": v(55.73, 80.11) * mm});
            skLineSegment(sketch, "E11.90.5", {"start": v(51.27, 73.97) * mm, "end": v(55.73, 80.11) * mm});
            skLineSegment(sketch, "E11.90.6", {"start": v(54.5, 71.62) * mm, "end": v(58.97, 77.76) * mm});
            skLineSegment(sketch, "E11.91.0", {"start": v(51.21, 83.9) * mm, "end": v(53.1, 84.32) * mm});
            skArc(sketch, "E11.91.1", {"start": v(53.7, 83.94) * mm, "mid": v(53.47, 84.25) * mm, "end": v(53.1, 84.32) * mm});
            skLineSegment(sketch, "E11.91.2", {"start": v(54.1, 82.06) * mm, "end": v(53.7, 83.94) * mm});
            skArc(sketch, "E11.91.3", {"start": v(54.1, 82.06) * mm, "mid": v(54.1, 81.67) * mm, "end": v(53.97, 81.3) * mm});
            skArc(sketch, "E11.91.4", {"start": v(51.21, 83.9) * mm, "mid": v(50.86, 83.73) * mm, "end": v(50.6, 83.45) * mm});
            skLineSegment(sketch, "E11.91.5", {"start": v(46.52, 77.04) * mm, "end": v(50.6, 83.45) * mm});
            skLineSegment(sketch, "E11.91.6", {"start": v(49.9, 74.9) * mm, "end": v(53.97, 81.3) * mm});
            skLineSegment(sketch, "E11.92.0", {"start": v(45.84, 86.94) * mm, "end": v(47.7, 87.49) * mm});
            skArc(sketch, "E11.92.1", {"start": v(48.31, 87.14) * mm, "mid": v(48.07, 87.45) * mm, "end": v(47.7, 87.49) * mm});
            skLineSegment(sketch, "E11.92.2", {"start": v(48.84, 85.3) * mm, "end": v(48.31, 87.14) * mm});
            skArc(sketch, "E11.92.3", {"start": v(48.84, 85.3) * mm, "mid": v(48.87, 84.9) * mm, "end": v(48.76, 84.54) * mm});
            skArc(sketch, "E11.92.4", {"start": v(45.84, 86.94) * mm, "mid": v(45.5, 86.76) * mm, "end": v(45.25, 86.46) * mm});
            skLineSegment(sketch, "E11.92.5", {"start": v(41.6, 79.81) * mm, "end": v(45.25, 86.46) * mm});
            skLineSegment(sketch, "E11.92.6", {"start": v(45.1, 77.88) * mm, "end": v(48.76, 84.54) * mm});
            skLineSegment(sketch, "E11.93.0", {"start": v(40.3, 89.65) * mm, "end": v(42.1, 90.3) * mm});
            skArc(sketch, "E11.93.1", {"start": v(42.75, 90) * mm, "mid": v(42.49, 90.3) * mm, "end": v(42.1, 90.3) * mm});
            skLineSegment(sketch, "E11.93.2", {"start": v(43.39, 88.2) * mm, "end": v(42.75, 90) * mm});
            skArc(sketch, "E11.93.3", {"start": v(43.39, 88.2) * mm, "mid": v(43.45, 87.8) * mm, "end": v(43.35, 87.43) * mm});
            skArc(sketch, "E11.93.4", {"start": v(40.3, 89.65) * mm, "mid": v(39.96, 89.45) * mm, "end": v(39.73, 89.13) * mm});
            skLineSegment(sketch, "E11.93.5", {"start": v(36.5, 82.27) * mm, "end": v(39.73, 89.13) * mm});
            skLineSegment(sketch, "E11.93.6", {"start": v(40.12, 80.56) * mm, "end": v(43.35, 87.43) * mm});
            skLineSegment(sketch, "E11.94.0", {"start": v(34.59, 92) * mm, "end": v(36.35, 92.77) * mm});
            skArc(sketch, "E11.94.1", {"start": v(37.01, 92.51) * mm, "mid": v(36.73, 92.78) * mm, "end": v(36.35, 92.77) * mm});
            skLineSegment(sketch, "E11.94.2", {"start": v(37.77, 90.74) * mm, "end": v(37.01, 92.51) * mm});
            skArc(sketch, "E11.94.3", {"start": v(37.77, 90.74) * mm, "mid": v(37.85, 90.36) * mm, "end": v(37.78, 89.98) * mm});
            skArc(sketch, "E11.94.4", {"start": v(34.59, 92) * mm, "mid": v(34.27, 91.78) * mm, "end": v(34.06, 91.45) * mm});
            skLineSegment(sketch, "E11.94.5", {"start": v(31.26, 84.4) * mm, "end": v(34.06, 91.45) * mm});
            skLineSegment(sketch, "E11.94.6", {"start": v(34.98, 82.92) * mm, "end": v(37.78, 89.98) * mm});
            skLineSegment(sketch, "E11.95.0", {"start": v(28.74, 94) * mm, "end": v(30.45, 94.87) * mm});
            skArc(sketch, "E11.95.1", {"start": v(31.13, 94.65) * mm, "mid": v(30.84, 94.9) * mm, "end": v(30.45, 94.87) * mm});
            skLineSegment(sketch, "E11.95.2", {"start": v(32, 92.93) * mm, "end": v(31.13, 94.65) * mm});
            skArc(sketch, "E11.95.3", {"start": v(32, 92.93) * mm, "mid": v(32.1, 92.56) * mm, "end": v(32.05, 92.17) * mm});
            skArc(sketch, "E11.95.4", {"start": v(28.74, 94) * mm, "mid": v(28.44, 93.75) * mm, "end": v(28.25, 93.41) * mm});
            skLineSegment(sketch, "E11.95.5", {"start": v(25.9, 86.2) * mm, "end": v(28.25, 93.41) * mm});
            skLineSegment(sketch, "E11.95.6", {"start": v(29.7, 84.96) * mm, "end": v(32.05, 92.17) * mm});
            skLineSegment(sketch, "E11.96.0", {"start": v(22.78, 95.6) * mm, "end": v(24.44, 96.6) * mm});
            skArc(sketch, "E11.96.1", {"start": v(25.12, 96.42) * mm, "mid": v(24.82, 96.65) * mm, "end": v(24.44, 96.6) * mm});
            skLineSegment(sketch, "E11.96.2", {"start": v(26.1, 94.76) * mm, "end": v(25.12, 96.42) * mm});
            skArc(sketch, "E11.96.3", {"start": v(26.1, 94.76) * mm, "mid": v(26.22, 94.4) * mm, "end": v(26.2, 94) * mm});
            skArc(sketch, "E11.96.4", {"start": v(22.78, 95.6) * mm, "mid": v(22.5, 95.35) * mm, "end": v(22.33, 95) * mm});
            skLineSegment(sketch, "E11.96.5", {"start": v(20.44, 87.65) * mm, "end": v(22.33, 95) * mm});
            skLineSegment(sketch, "E11.96.6", {"start": v(24.31, 86.65) * mm, "end": v(26.2, 94) * mm});
            skLineSegment(sketch, "E11.97.0", {"start": v(16.73, 96.85) * mm, "end": v(18.32, 97.94) * mm});
            skArc(sketch, "E11.97.1", {"start": v(19.02, 97.8) * mm, "mid": v(18.7, 98.02) * mm, "end": v(18.32, 97.94) * mm});
            skLineSegment(sketch, "E11.97.2", {"start": v(20.1, 96.21) * mm, "end": v(19.02, 97.8) * mm});
            skArc(sketch, "E11.97.3", {"start": v(20.1, 96.21) * mm, "mid": v(20.24, 95.85) * mm, "end": v(20.25, 95.47) * mm});
            skArc(sketch, "E11.97.4", {"start": v(16.73, 96.85) * mm, "mid": v(16.46, 96.57) * mm, "end": v(16.32, 96.21) * mm});
            skLineSegment(sketch, "E11.97.5", {"start": v(14.9, 88.76) * mm, "end": v(16.32, 96.21) * mm});
            skLineSegment(sketch, "E11.97.6", {"start": v(18.82, 88) * mm, "end": v(20.25, 95.47) * mm});
            skLineSegment(sketch, "E11.98.0", {"start": v(10.62, 97.71) * mm, "end": v(12.14, 98.9) * mm});
            skArc(sketch, "E11.98.1", {"start": v(12.84, 98.81) * mm, "mid": v(12.5, 99) * mm, "end": v(12.14, 98.9) * mm});
            skLineSegment(sketch, "E11.98.2", {"start": v(14.01, 97.28) * mm, "end": v(12.84, 98.81) * mm});
            skArc(sketch, "E11.98.3", {"start": v(14.01, 97.28) * mm, "mid": v(14.19, 96.94) * mm, "end": v(14.21, 96.55) * mm});
            skArc(sketch, "E11.98.4", {"start": v(10.62, 97.71) * mm, "mid": v(10.37, 97.42) * mm, "end": v(10.24, 97.05) * mm});
            skLineSegment(sketch, "E11.98.5", {"start": v(9.3, 89.52) * mm, "end": v(10.24, 97.05) * mm});
            skLineSegment(sketch, "E11.98.6", {"start": v(13.26, 89.02) * mm, "end": v(14.21, 96.55) * mm});
            skLineSegment(sketch, "E11.99.0", {"start": v(4.46, 98.19) * mm, "end": v(5.9, 99.47) * mm});
            skArc(sketch, "E11.99.1", {"start": v(6.61, 99.42) * mm, "mid": v(6.27, 99.6) * mm, "end": v(5.9, 99.47) * mm});
            skLineSegment(sketch, "E11.99.2", {"start": v(7.88, 97.97) * mm, "end": v(6.61, 99.42) * mm});
            skArc(sketch, "E11.99.3", {"start": v(7.88, 97.97) * mm, "mid": v(8.07, 97.63) * mm, "end": v(8.12, 97.25) * mm});
            skArc(sketch, "E11.99.4", {"start": v(4.46, 98.19) * mm, "mid": v(4.23, 97.88) * mm, "end": v(4.13, 97.5) * mm});
            skLineSegment(sketch, "E11.99.5", {"start": v(3.65, 89.93) * mm, "end": v(4.13, 97.5) * mm});
            skLineSegment(sketch, "E11.99.6", {"start": v(7.65, 89.67) * mm, "end": v(8.12, 97.25) * mm});
            skArc(sketch, "E12.trimOffspring", {"start": v(-24.31, 86.65) * mm, "mid": v(-25.1, 86.43) * mm, "end": v(-25.9, 86.2) * mm});
            skLineSegment(sketch, "E13", {"start": v(-29.7, 84.96) * mm, "end": v(-31.26, 84.4) * mm});
            skLineSegment(sketch, "E14", {"start": v(-34.87, 82.83) * mm, "end": v(-36.5, 82.27) * mm});
            skLineSegment(sketch, "E15", {"start": v(-39.91, 80.81) * mm, "end": v(-41.3, 79.8) * mm});
            skLineSegment(sketch, "E16", {"start": v(-45.1, 77.88) * mm, "end": v(-46.52, 77.04) * mm});
            skLineSegment(sketch, "E17", {"start": v(-90.9, 65.54) * mm, "end": v(-93.55, 76.27) * mm});
            skArc(sketch, "E18", {"start": v(-2, 91.98) * mm, "mid": v(-2.89, 91.95) * mm, "end": v(-3.78, 91.92) * mm});
            skArc(sketch, "E19.trimOffspring", {"start": v(3.78, 91.92) * mm, "mid": v(2.89, 91.95) * mm, "end": v(2, 91.98) * mm});
            skArc(sketch, "E20.trimOffspring", {"start": v(9.54, 91.5) * mm, "mid": v(8.66, 91.6) * mm, "end": v(7.77, 91.67) * mm});
            skArc(sketch, "E21.trimOffspring", {"start": v(15.27, 90.72) * mm, "mid": v(14.4, 90.87) * mm, "end": v(13.51, 91) * mm});
            skArc(sketch, "E22.trimOffspring", {"start": v(20.94, 89.59) * mm, "mid": v(20.07, 89.78) * mm, "end": v(19.2, 89.97) * mm});
            skArc(sketch, "E23.trimOffspring", {"start": v(26.52, 88.1) * mm, "mid": v(25.67, 88.35) * mm, "end": v(24.81, 88.6) * mm});
            skArc(sketch, "E24.trimOffspring", {"start": v(32, 86.26) * mm, "mid": v(31.16, 86.56) * mm, "end": v(30.32, 86.86) * mm});
            skArc(sketch, "E25.trimOffspring", {"start": v(37.35, 84.08) * mm, "mid": v(36.54, 84.43) * mm, "end": v(35.72, 84.78) * mm});
            skArc(sketch, "E26.trimOffspring", {"start": v(42.56, 81.56) * mm, "mid": v(41.77, 81.97) * mm, "end": v(40.97, 82.37) * mm});
            skArc(sketch, "E27.trimOffspring", {"start": v(47.6, 78.73) * mm, "mid": v(46.83, 79.19) * mm, "end": v(46.06, 79.64) * mm});
            skArc(sketch, "E28.trimOffspring", {"start": v(-7.77, 91.67) * mm, "mid": v(-8.66, 91.6) * mm, "end": v(-9.54, 91.5) * mm});
            skArc(sketch, "E29.trimOffspring", {"start": v(-13.51, 91) * mm, "mid": v(-14.4, 90.87) * mm, "end": v(-15.27, 90.72) * mm});
            skArc(sketch, "E30.trimOffspring", {"start": v(-19.2, 89.97) * mm, "mid": v(-20.07, 89.78) * mm, "end": v(-20.94, 89.59) * mm});
            skArc(sketch, "E31.trimOffspring", {"start": v(-24.81, 88.6) * mm, "mid": v(-25.67, 88.35) * mm, "end": v(-26.52, 88.1) * mm});
            skArc(sketch, "E32.trimOffspring", {"start": v(-30.32, 86.86) * mm, "mid": v(-31.16, 86.56) * mm, "end": v(-32, 86.26) * mm});
            skArc(sketch, "E33.trimOffspring", {"start": v(-35.72, 84.78) * mm, "mid": v(-36.54, 84.43) * mm, "end": v(-37.35, 84.08) * mm});
            skArc(sketch, "E34.trimOffspring", {"start": v(-40.97, 82.37) * mm, "mid": v(-41.77, 81.97) * mm, "end": v(-42.56, 81.56) * mm});
            skArc(sketch, "E35.trimOffspring", {"start": v(-46.06, 79.64) * mm, "mid": v(-46.83, 79.19) * mm, "end": v(-47.6, 78.73) * mm});
            skArc(sketch, "E36.trimOffspring", {"start": v(-50.97, 76.59) * mm, "mid": v(-51.71, 76.1) * mm, "end": v(-52.45, 75.59) * mm});
            skArc(sketch, "E37.trimOffspring", {"start": v(-55.68, 73.24) * mm, "mid": v(-56.39, 72.7) * mm, "end": v(-57.09, 72.15) * mm});
            skArc(sketch, "E38.trimOffspring", {"start": v(-60.17, 69.6) * mm, "mid": v(-60.84, 69.01) * mm, "end": v(-61.5, 68.42) * mm});
            skArc(sketch, "E39.trimOffspring", {"start": v(-64.42, 65.68) * mm, "mid": v(-65.05, 65.05) * mm, "end": v(-65.68, 64.42) * mm});
            skArc(sketch, "E40.trimOffspring", {"start": v(-68.42, 61.5) * mm, "mid": v(-69.01, 60.84) * mm, "end": v(-69.6, 60.17) * mm});
            skArc(sketch, "E41.trimOffspring", {"start": v(-72.15, 57.09) * mm, "mid": v(-72.7, 56.39) * mm, "end": v(-73.24, 55.68) * mm});
            skArc(sketch, "E42.trimOffspring", {"start": v(-75.59, 52.45) * mm, "mid": v(-76.1, 51.71) * mm, "end": v(-76.59, 50.97) * mm});
            skArc(sketch, "E43.trimOffspring", {"start": v(-78.73, 47.6) * mm, "mid": v(-79.19, 46.83) * mm, "end": v(-79.64, 46.06) * mm});
            skArc(sketch, "E44.trimOffspring", {"start": v(-81.56, 42.56) * mm, "mid": v(-81.97, 41.77) * mm, "end": v(-82.37, 40.97) * mm});
            skArc(sketch, "E45.trimOffspring", {"start": v(-84.08, 37.35) * mm, "mid": v(-84.43, 36.54) * mm, "end": v(-84.78, 35.72) * mm});
            skArc(sketch, "E46.trimOffspring", {"start": v(-86.26, 32) * mm, "mid": v(-86.56, 31.16) * mm, "end": v(-86.86, 30.32) * mm});
            skArc(sketch, "E47.trimOffspring", {"start": v(-88.1, 26.52) * mm, "mid": v(-88.35, 25.67) * mm, "end": v(-88.6, 24.81) * mm});
            skArc(sketch, "E48.trimOffspring", {"start": v(-89.59, 20.94) * mm, "mid": v(-89.78, 20.07) * mm, "end": v(-89.97, 19.2) * mm});
            skArc(sketch, "E49.trimOffspring", {"start": v(-90.72, 15.27) * mm, "mid": v(-90.87, 14.4) * mm, "end": v(-91, 13.51) * mm});
            skArc(sketch, "E50.trimOffspring", {"start": v(-91.5, 9.54) * mm, "mid": v(-91.6, 8.66) * mm, "end": v(-91.67, 7.77) * mm});
            skArc(sketch, "E51.trimOffspring", {"start": v(-91.92, 3.78) * mm, "mid": v(-91.95, 2.89) * mm, "end": v(-91.98, 2) * mm});
            skArc(sketch, "E52.trimOffspring", {"start": v(-92, 0) * mm, "mid": v(-91.98, -1.9) * mm, "end": v(-91.92, -3.78) * mm});
            skArc(sketch, "E53.trimOffspring", {"start": v(52.45, 75.59) * mm, "mid": v(51.71, 76.1) * mm, "end": v(50.97, 76.59) * mm});
            skArc(sketch, "E54.trimOffspring", {"start": v(57.09, 72.15) * mm, "mid": v(56.39, 72.7) * mm, "end": v(55.68, 73.24) * mm});
            skArc(sketch, "E55.trimOffspring", {"start": v(61.5, 68.42) * mm, "mid": v(60.84, 69.01) * mm, "end": v(60.17, 69.6) * mm});
            skArc(sketch, "E56.trimOffspring", {"start": v(65.68, 64.42) * mm, "mid": v(65.05, 65.05) * mm, "end": v(64.42, 65.68) * mm});
            skArc(sketch, "E57.trimOffspring", {"start": v(69.6, 60.17) * mm, "mid": v(69.01, 60.84) * mm, "end": v(68.42, 61.5) * mm});
            skArc(sketch, "E58.trimOffspring", {"start": v(73.24, 55.68) * mm, "mid": v(72.7, 56.39) * mm, "end": v(72.15, 57.09) * mm});
            skArc(sketch, "E59.trimOffspring", {"start": v(76.59, 50.97) * mm, "mid": v(76.1, 51.71) * mm, "end": v(75.59, 52.45) * mm});
            skArc(sketch, "E60.trimOffspring", {"start": v(79.64, 46.06) * mm, "mid": v(79.19, 46.83) * mm, "end": v(78.73, 47.6) * mm});
            skArc(sketch, "E61.trimOffspring", {"start": v(82.37, 40.97) * mm, "mid": v(81.97, 41.77) * mm, "end": v(81.56, 42.56) * mm});
            skArc(sketch, "E62.trimOffspring", {"start": v(84.78, 35.72) * mm, "mid": v(84.43, 36.54) * mm, "end": v(84.08, 37.35) * mm});
            skArc(sketch, "E63.trimOffspring", {"start": v(86.86, 30.32) * mm, "mid": v(86.56, 31.16) * mm, "end": v(86.26, 32) * mm});
            skArc(sketch, "E64.trimOffspring", {"start": v(88.6, 24.81) * mm, "mid": v(88.35, 25.67) * mm, "end": v(88.1, 26.52) * mm});
            skArc(sketch, "E65.trimOffspring", {"start": v(89.97, 19.2) * mm, "mid": v(89.78, 20.07) * mm, "end": v(89.59, 20.94) * mm});
            skArc(sketch, "E66.trimOffspring", {"start": v(91, 13.51) * mm, "mid": v(90.87, 14.4) * mm, "end": v(90.72, 15.27) * mm});
            skArc(sketch, "E67.trimOffspring", {"start": v(91.67, 7.77) * mm, "mid": v(91.6, 8.66) * mm, "end": v(91.5, 9.54) * mm});
            skArc(sketch, "E68.trimOffspring", {"start": v(91.98, 2) * mm, "mid": v(91.95, 2.89) * mm, "end": v(91.92, 3.78) * mm});
            skArc(sketch, "E69.trimOffspring", {"start": v(91.92, -3.78) * mm, "mid": v(91.98, -1.9) * mm, "end": v(92, 0) * mm});
            skArc(sketch, "E70.trimOffspring", {"start": v(91.5, -9.54) * mm, "mid": v(91.6, -8.66) * mm, "end": v(91.67, -7.77) * mm});
            skArc(sketch, "E71.trimOffspring", {"start": v(90.72, -15.27) * mm, "mid": v(90.87, -14.4) * mm, "end": v(91, -13.51) * mm});
            skArc(sketch, "E72.trimOffspring", {"start": v(89.59, -20.94) * mm, "mid": v(89.78, -20.07) * mm, "end": v(89.97, -19.2) * mm});
            skArc(sketch, "E73.trimOffspring", {"start": v(88.1, -26.52) * mm, "mid": v(88.35, -25.67) * mm, "end": v(88.6, -24.81) * mm});
            skArc(sketch, "E74.trimOffspring", {"start": v(86.26, -32) * mm, "mid": v(86.56, -31.16) * mm, "end": v(86.86, -30.32) * mm});
            skArc(sketch, "E75.trimOffspring", {"start": v(84.08, -37.35) * mm, "mid": v(84.43, -36.54) * mm, "end": v(84.78, -35.72) * mm});
            skArc(sketch, "E76.trimOffspring", {"start": v(81.56, -42.56) * mm, "mid": v(81.97, -41.77) * mm, "end": v(82.37, -40.97) * mm});
            skArc(sketch, "E77.trimOffspring", {"start": v(78.73, -47.6) * mm, "mid": v(79.19, -46.83) * mm, "end": v(79.64, -46.06) * mm});
            skArc(sketch, "E78.trimOffspring", {"start": v(75.59, -52.45) * mm, "mid": v(76.1, -51.71) * mm, "end": v(76.59, -50.97) * mm});
            skArc(sketch, "E79.trimOffspring", {"start": v(72.15, -57.09) * mm, "mid": v(72.7, -56.39) * mm, "end": v(73.24, -55.68) * mm});
            skArc(sketch, "E80.trimOffspring", {"start": v(68.42, -61.5) * mm, "mid": v(69.01, -60.84) * mm, "end": v(69.6, -60.17) * mm});
            skArc(sketch, "E81.trimOffspring", {"start": v(64.42, -65.68) * mm, "mid": v(65.05, -65.05) * mm, "end": v(65.68, -64.42) * mm});
            skArc(sketch, "E82.trimOffspring", {"start": v(60.17, -69.6) * mm, "mid": v(60.84, -69.01) * mm, "end": v(61.5, -68.42) * mm});
            skArc(sketch, "E83.trimOffspring", {"start": v(55.68, -73.24) * mm, "mid": v(56.39, -72.7) * mm, "end": v(57.09, -72.15) * mm});
            skArc(sketch, "E84.trimOffspring", {"start": v(50.97, -76.59) * mm, "mid": v(51.71, -76.1) * mm, "end": v(52.45, -75.59) * mm});
            skArc(sketch, "E85.trimOffspring", {"start": v(46.06, -79.64) * mm, "mid": v(46.83, -79.19) * mm, "end": v(47.6, -78.73) * mm});
            skArc(sketch, "E86.trimOffspring", {"start": v(40.97, -82.37) * mm, "mid": v(41.77, -81.97) * mm, "end": v(42.56, -81.56) * mm});
            skArc(sketch, "E87.trimOffspring", {"start": v(35.72, -84.78) * mm, "mid": v(36.54, -84.43) * mm, "end": v(37.35, -84.08) * mm});
            skArc(sketch, "E88.trimOffspring", {"start": v(30.32, -86.86) * mm, "mid": v(31.16, -86.56) * mm, "end": v(32, -86.26) * mm});
            skArc(sketch, "E89.trimOffspring", {"start": v(24.81, -88.6) * mm, "mid": v(25.67, -88.35) * mm, "end": v(26.52, -88.1) * mm});
            skArc(sketch, "E90.trimOffspring", {"start": v(19.2, -89.97) * mm, "mid": v(20.07, -89.78) * mm, "end": v(20.94, -89.59) * mm});
            skArc(sketch, "E91.trimOffspring", {"start": v(13.51, -91) * mm, "mid": v(14.4, -90.87) * mm, "end": v(15.27, -90.72) * mm});
            skArc(sketch, "E92.trimOffspring", {"start": v(7.77, -91.67) * mm, "mid": v(8.66, -91.6) * mm, "end": v(9.54, -91.5) * mm});
            skArc(sketch, "E93.trimOffspring", {"start": v(0, -92) * mm, "mid": v(1.9, -91.98) * mm, "end": v(3.78, -91.92) * mm});
            skArc(sketch, "E94.trimOffspring", {"start": v(-3.78, -91.92) * mm, "mid": v(-2.89, -91.95) * mm, "end": v(-2, -91.98) * mm});
            skArc(sketch, "E95.trimOffspring", {"start": v(-9.54, -91.5) * mm, "mid": v(-8.66, -91.6) * mm, "end": v(-7.77, -91.67) * mm});
            skArc(sketch, "E96.trimOffspring", {"start": v(-15.27, -90.72) * mm, "mid": v(-14.4, -90.87) * mm, "end": v(-13.51, -91) * mm});
            skArc(sketch, "E97.trimOffspring", {"start": v(-20.94, -89.59) * mm, "mid": v(-20.07, -89.78) * mm, "end": v(-19.2, -89.97) * mm});
            skArc(sketch, "E98.trimOffspring", {"start": v(-26.52, -88.1) * mm, "mid": v(-25.67, -88.35) * mm, "end": v(-24.81, -88.6) * mm});
            skArc(sketch, "E99.trimOffspring", {"start": v(-32, -86.26) * mm, "mid": v(-31.16, -86.56) * mm, "end": v(-30.32, -86.86) * mm});
            skArc(sketch, "E100.trimOffspring", {"start": v(-37.35, -84.08) * mm, "mid": v(-36.54, -84.43) * mm, "end": v(-35.72, -84.78) * mm});
            skArc(sketch, "E101.trimOffspring", {"start": v(-42.56, -81.56) * mm, "mid": v(-41.77, -81.97) * mm, "end": v(-40.97, -82.37) * mm});
            skArc(sketch, "E102.trimOffspring", {"start": v(-47.6, -78.73) * mm, "mid": v(-46.83, -79.19) * mm, "end": v(-46.06, -79.64) * mm});
            skArc(sketch, "E103.trimOffspring", {"start": v(-52.45, -75.59) * mm, "mid": v(-51.71, -76.1) * mm, "end": v(-50.97, -76.59) * mm});
            skArc(sketch, "E104.trimOffspring", {"start": v(-57.09, -72.15) * mm, "mid": v(-56.39, -72.7) * mm, "end": v(-55.68, -73.24) * mm});
            skArc(sketch, "E105.trimOffspring", {"start": v(-61.5, -68.42) * mm, "mid": v(-60.84, -69.01) * mm, "end": v(-60.17, -69.6) * mm});
            skArc(sketch, "E106.trimOffspring", {"start": v(-65.68, -64.42) * mm, "mid": v(-65.05, -65.05) * mm, "end": v(-64.42, -65.68) * mm});
            skArc(sketch, "E107.trimOffspring", {"start": v(-69.6, -60.17) * mm, "mid": v(-69.01, -60.84) * mm, "end": v(-68.42, -61.5) * mm});
            skArc(sketch, "E108.trimOffspring", {"start": v(-73.24, -55.68) * mm, "mid": v(-72.7, -56.39) * mm, "end": v(-72.15, -57.09) * mm});
            skArc(sketch, "E109.trimOffspring", {"start": v(-76.59, -50.97) * mm, "mid": v(-76.1, -51.71) * mm, "end": v(-75.59, -52.45) * mm});
            skArc(sketch, "E110.trimOffspring", {"start": v(-79.64, -46.06) * mm, "mid": v(-79.19, -46.83) * mm, "end": v(-78.73, -47.6) * mm});
            skArc(sketch, "E111.trimOffspring", {"start": v(-82.37, -40.97) * mm, "mid": v(-81.97, -41.77) * mm, "end": v(-81.56, -42.56) * mm});
            skArc(sketch, "E112.trimOffspring", {"start": v(-84.78, -35.72) * mm, "mid": v(-84.43, -36.54) * mm, "end": v(-84.08, -37.35) * mm});
            skArc(sketch, "E113.trimOffspring", {"start": v(-86.86, -30.32) * mm, "mid": v(-86.56, -31.16) * mm, "end": v(-86.26, -32) * mm});
            skArc(sketch, "E114.trimOffspring", {"start": v(-88.6, -24.81) * mm, "mid": v(-88.35, -25.67) * mm, "end": v(-88.1, -26.52) * mm});
            skArc(sketch, "E115.trimOffspring", {"start": v(-89.97, -19.2) * mm, "mid": v(-89.78, -20.07) * mm, "end": v(-89.59, -20.94) * mm});
            skArc(sketch, "E116.trimOffspring", {"start": v(-91, -13.51) * mm, "mid": v(-90.87, -14.4) * mm, "end": v(-90.72, -15.27) * mm});
            skArc(sketch, "E117.trimOffspring", {"start": v(-91.67, -7.77) * mm, "mid": v(-91.6, -8.66) * mm, "end": v(-91.5, -9.54) * mm});
            skSolve(sketch);
        }
        {
            var Q0;
            Q0 = qSketchRegion(id + "F0", true);
            extrude(context, id + "F1", {"entities" : qUnion([Q0]), "depth" : 25 * mm, "offsetDistance" : 25 * mm});
        }
        {
            var Q0;
            Q0=makeQuery(id+"F1.opExtrude","CAP_FACE",FACE,{"disambiguationData":[OSD([sQuery(id+"F0.wireOp",EDGE,"E4"),sQuery(id+"F0.wireOp",EDGE,"E5"),sQuery(id+"F0.wireOp",EDGE,"E6.filletArc"),sQuery(id+"F0.wireOp",EDGE,"E7.MirrorCS"),sQuery(id+"F0.wireOp",EDGE,"E8.MirrorCS"),sQuery(id+"F0.wireOp",EDGE,"E9.MirrorCS"),sQuery(id+"F0.wireOp",EDGE,"E10.filletArc"),sQuery(id+"F0.wireOp",EDGE,"E11.1.0"),sQuery(id+"F0.wireOp",EDGE,"E11.1.1"),sQuery(id+"F0.wireOp",EDGE,"E11.1.2"),sQuery(id+"F0.wireOp",EDGE,"E11.1.3"),sQuery(id+"F0.wireOp",EDGE,"E11.1.4"),sQuery(id+"F0.wireOp",EDGE,"E11.1.5"),sQuery(id+"F0.wireOp",EDGE,"E11.1.6"),sQuery(id+"F0.wireOp",EDGE,"E11.2.0"),sQuery(id+"F0.wireOp",EDGE,"E11.2.1"),sQuery(id+"F0.wireOp",EDGE,"E11.2.2"),sQuery(id+"F0.wireOp",EDGE,"E11.2.3"),sQuery(id+"F0.wireOp",EDGE,"E11.2.4"),sQuery(id+"F0.wireOp",EDGE,"E11.2.5"),sQuery(id+"F0.wireOp",EDGE,"E11.2.6"),sQuery(id+"F0.wireOp",EDGE,"E11.3.0"),sQuery(id+"F0.wireOp",EDGE,"E11.3.1"),sQuery(id+"F0.wireOp",EDGE,"E11.3.2"),sQuery(id+"F0.wireOp",EDGE,"E11.3.3"),sQuery(id+"F0.wireOp",EDGE,"E11.3.4"),sQuery(id+"F0.wireOp",EDGE,"E11.3.5"),sQuery(id+"F0.wireOp",EDGE,"E11.3.6"),sQuery(id+"F0.wireOp",EDGE,"E11.4.0"),sQuery(id+"F0.wireOp",EDGE,"E11.4.1"),sQuery(id+"F0.wireOp",EDGE,"E11.4.2"),sQuery(id+"F0.wireOp",EDGE,"E11.4.3"),sQuery(id+"F0.wireOp",EDGE,"E11.4.4"),sQuery(id+"F0.wireOp",EDGE,"E11.4.5"),sQuery(id+"F0.wireOp",EDGE,"E11.4.6"),sQuery(id+"F0.wireOp",EDGE,"E11.5.0"),sQuery(id+"F0.wireOp",EDGE,"E11.5.1"),sQuery(id+"F0.wireOp",EDGE,"E11.5.2"),sQuery(id+"F0.wireOp",EDGE,"E11.5.3"),sQuery(id+"F0.wireOp",EDGE,"E11.5.4"),sQuery(id+"F0.wireOp",EDGE,"E11.5.5"),sQuery(id+"F0.wireOp",EDGE,"E11.5.6"),sQuery(id+"F0.wireOp",EDGE,"E11.6.0"),sQuery(id+"F0.wireOp",EDGE,"E11.6.1"),sQuery(id+"F0.wireOp",EDGE,"E11.6.2"),sQuery(id+"F0.wireOp",EDGE,"E11.6.3"),sQuery(id+"F0.wireOp",EDGE,"E11.6.4"),sQuery(id+"F0.wireOp",EDGE,"E11.6.5"),sQuery(id+"F0.wireOp",EDGE,"E11.6.6"),sQuery(id+"F0.wireOp",EDGE,"E11.7.0"),sQuery(id+"F0.wireOp",EDGE,"E11.7.1"),sQuery(id+"F0.wireOp",EDGE,"E11.7.2"),sQuery(id+"F0.wireOp",EDGE,"E11.7.3"),sQuery(id+"F0.wireOp",EDGE,"E11.7.4"),sQuery(id+"F0.wireOp",EDGE,"E11.7.5"),sQuery(id+"F0.wireOp",EDGE,"E11.7.6"),sQuery(id+"F0.wireOp",EDGE,"E11.8.0"),sQuery(id+"F0.wireOp",EDGE,"E11.8.1"),sQuery(id+"F0.wireOp",EDGE,"E11.8.2"),sQuery(id+"F0.wireOp",EDGE,"E11.8.3"),sQuery(id+"F0.wireOp",EDGE,"E11.8.4"),sQuery(id+"F0.wireOp",EDGE,"E11.8.5"),sQuery(id+"F0.wireOp",EDGE,"E11.8.6"),sQuery(id+"F0.wireOp",EDGE,"E11.9.0"),sQuery(id+"F0.wireOp",EDGE,"E11.9.1"),sQuery(id+"F0.wireOp",EDGE,"E11.9.2"),sQuery(id+"F0.wireOp",EDGE,"E11.9.3"),sQuery(id+"F0.wireOp",EDGE,"E11.9.4"),sQuery(id+"F0.wireOp",EDGE,"E11.9.5"),sQuery(id+"F0.wireOp",EDGE,"E11.9.6"),sQuery(id+"F0.wireOp",EDGE,"E11.10.0"),sQuery(id+"F0.wireOp",EDGE,"E11.10.1"),sQuery(id+"F0.wireOp",EDGE,"E11.10.2"),sQuery(id+"F0.wireOp",EDGE,"E11.10.3"),sQuery(id+"F0.wireOp",EDGE,"E11.10.4"),sQuery(id+"F0.wireOp",EDGE,"E11.10.5"),sQuery(id+"F0.wireOp",EDGE,"E11.10.6"),sQuery(id+"F0.wireOp",EDGE,"E11.11.0"),sQuery(id+"F0.wireOp",EDGE,"E11.11.1"),sQuery(id+"F0.wireOp",EDGE,"E11.11.2"),sQuery(id+"F0.wireOp",EDGE,"E11.11.3"),sQuery(id+"F0.wireOp",EDGE,"E11.11.4"),sQuery(id+"F0.wireOp",EDGE,"E11.11.5"),sQuery(id+"F0.wireOp",EDGE,"E11.11.6"),sQuery(id+"F0.wireOp",EDGE,"E11.12.0"),sQuery(id+"F0.wireOp",EDGE,"E11.12.1"),sQuery(id+"F0.wireOp",EDGE,"E11.12.2"),sQuery(id+"F0.wireOp",EDGE,"E11.12.3"),sQuery(id+"F0.wireOp",EDGE,"E11.12.4"),sQuery(id+"F0.wireOp",EDGE,"E11.12.5"),sQuery(id+"F0.wireOp",EDGE,"E11.12.6"),sQuery(id+"F0.wireOp",EDGE,"E11.13.0"),sQuery(id+"F0.wireOp",EDGE,"E11.13.1"),sQuery(id+"F0.wireOp",EDGE,"E11.13.2"),sQuery(id+"F0.wireOp",EDGE,"E11.13.3"),sQuery(id+"F0.wireOp",EDGE,"E11.13.4"),sQuery(id+"F0.wireOp",EDGE,"E11.13.5"),sQuery(id+"F0.wireOp",EDGE,"E11.13.6"),sQuery(id+"F0.wireOp",EDGE,"E11.14.0"),sQuery(id+"F0.wireOp",EDGE,"E11.14.1"),sQuery(id+"F0.wireOp",EDGE,"E11.14.2"),sQuery(id+"F0.wireOp",EDGE,"E11.14.3"),sQuery(id+"F0.wireOp",EDGE,"E11.14.4"),sQuery(id+"F0.wireOp",EDGE,"E11.14.5"),sQuery(id+"F0.wireOp",EDGE,"E11.14.6"),sQuery(id+"F0.wireOp",EDGE,"E11.15.0"),sQuery(id+"F0.wireOp",EDGE,"E11.15.1"),sQuery(id+"F0.wireOp",EDGE,"E11.15.2"),sQuery(id+"F0.wireOp",EDGE,"E11.15.3"),sQuery(id+"F0.wireOp",EDGE,"E11.15.4"),sQuery(id+"F0.wireOp",EDGE,"E11.15.5"),sQuery(id+"F0.wireOp",EDGE,"E11.15.6"),sQuery(id+"F0.wireOp",EDGE,"E11.16.0"),sQuery(id+"F0.wireOp",EDGE,"E11.16.1"),sQuery(id+"F0.wireOp",EDGE,"E11.16.2"),sQuery(id+"F0.wireOp",EDGE,"E11.16.3"),sQuery(id+"F0.wireOp",EDGE,"E11.16.4"),sQuery(id+"F0.wireOp",EDGE,"E11.16.5"),sQuery(id+"F0.wireOp",EDGE,"E11.16.6"),sQuery(id+"F0.wireOp",EDGE,"E11.17.0"),sQuery(id+"F0.wireOp",EDGE,"E11.17.1"),sQuery(id+"F0.wireOp",EDGE,"E11.17.2"),sQuery(id+"F0.wireOp",EDGE,"E11.17.3"),sQuery(id+"F0.wireOp",EDGE,"E11.17.4"),sQuery(id+"F0.wireOp",EDGE,"E11.17.5"),sQuery(id+"F0.wireOp",EDGE,"E11.17.6"),sQuery(id+"F0.wireOp",EDGE,"E11.18.0"),sQuery(id+"F0.wireOp",EDGE,"E11.18.1"),sQuery(id+"F0.wireOp",EDGE,"E11.18.2"),sQuery(id+"F0.wireOp",EDGE,"E11.18.3"),sQuery(id+"F0.wireOp",EDGE,"E11.18.4"),sQuery(id+"F0.wireOp",EDGE,"E11.18.5"),sQuery(id+"F0.wireOp",EDGE,"E11.18.6"),sQuery(id+"F0.wireOp",EDGE,"E11.19.0"),sQuery(id+"F0.wireOp",EDGE,"E11.19.1"),sQuery(id+"F0.wireOp",EDGE,"E11.19.2"),sQuery(id+"F0.wireOp",EDGE,"E11.19.3"),sQuery(id+"F0.wireOp",EDGE,"E11.19.4"),sQuery(id+"F0.wireOp",EDGE,"E11.19.5"),sQuery(id+"F0.wireOp",EDGE,"E11.19.6"),sQuery(id+"F0.wireOp",EDGE,"E11.20.0"),sQuery(id+"F0.wireOp",EDGE,"E11.20.1"),sQuery(id+"F0.wireOp",EDGE,"E11.20.2"),sQuery(id+"F0.wireOp",EDGE,"E11.20.3"),sQuery(id+"F0.wireOp",EDGE,"E11.20.4"),sQuery(id+"F0.wireOp",EDGE,"E11.20.5"),sQuery(id+"F0.wireOp",EDGE,"E11.20.6"),sQuery(id+"F0.wireOp",EDGE,"E11.21.0"),sQuery(id+"F0.wireOp",EDGE,"E11.21.1"),sQuery(id+"F0.wireOp",EDGE,"E11.21.2"),sQuery(id+"F0.wireOp",EDGE,"E11.21.3"),sQuery(id+"F0.wireOp",EDGE,"E11.21.4"),sQuery(id+"F0.wireOp",EDGE,"E11.21.5"),sQuery(id+"F0.wireOp",EDGE,"E11.21.6"),sQuery(id+"F0.wireOp",EDGE,"E11.22.0"),sQuery(id+"F0.wireOp",EDGE,"E11.22.1"),sQuery(id+"F0.wireOp",EDGE,"E11.22.2"),sQuery(id+"F0.wireOp",EDGE,"E11.22.3"),sQuery(id+"F0.wireOp",EDGE,"E11.22.4"),sQuery(id+"F0.wireOp",EDGE,"E11.22.5"),sQuery(id+"F0.wireOp",EDGE,"E11.22.6"),sQuery(id+"F0.wireOp",EDGE,"E11.23.0"),sQuery(id+"F0.wireOp",EDGE,"E11.23.1"),sQuery(id+"F0.wireOp",EDGE,"E11.23.2"),sQuery(id+"F0.wireOp",EDGE,"E11.23.3"),sQuery(id+"F0.wireOp",EDGE,"E11.23.4"),sQuery(id+"F0.wireOp",EDGE,"E11.23.5"),sQuery(id+"F0.wireOp",EDGE,"E11.23.6"),sQuery(id+"F0.wireOp",EDGE,"E11.24.0"),sQuery(id+"F0.wireOp",EDGE,"E11.24.1"),sQuery(id+"F0.wireOp",EDGE,"E11.24.2"),sQuery(id+"F0.wireOp",EDGE,"E11.24.3"),sQuery(id+"F0.wireOp",EDGE,"E11.24.4"),sQuery(id+"F0.wireOp",EDGE,"E11.24.5"),sQuery(id+"F0.wireOp",EDGE,"E11.24.6"),sQuery(id+"F0.wireOp",EDGE,"E11.25.0"),sQuery(id+"F0.wireOp",EDGE,"E11.25.1"),sQuery(id+"F0.wireOp",EDGE,"E11.25.2"),sQuery(id+"F0.wireOp",EDGE,"E11.25.3"),sQuery(id+"F0.wireOp",EDGE,"E11.25.4"),sQuery(id+"F0.wireOp",EDGE,"E11.25.5"),sQuery(id+"F0.wireOp",EDGE,"E11.25.6"),sQuery(id+"F0.wireOp",EDGE,"E11.26.0"),sQuery(id+"F0.wireOp",EDGE,"E11.26.1"),sQuery(id+"F0.wireOp",EDGE,"E11.26.2"),sQuery(id+"F0.wireOp",EDGE,"E11.26.3"),sQuery(id+"F0.wireOp",EDGE,"E11.26.4"),sQuery(id+"F0.wireOp",EDGE,"E11.26.5"),sQuery(id+"F0.wireOp",EDGE,"E11.26.6"),sQuery(id+"F0.wireOp",EDGE,"E11.27.0"),sQuery(id+"F0.wireOp",EDGE,"E11.27.1"),sQuery(id+"F0.wireOp",EDGE,"E11.27.2"),sQuery(id+"F0.wireOp",EDGE,"E11.27.3"),sQuery(id+"F0.wireOp",EDGE,"E11.27.4"),sQuery(id+"F0.wireOp",EDGE,"E11.27.5"),sQuery(id+"F0.wireOp",EDGE,"E11.27.6"),sQuery(id+"F0.wireOp",EDGE,"E11.28.0"),sQuery(id+"F0.wireOp",EDGE,"E11.28.1"),sQuery(id+"F0.wireOp",EDGE,"E11.28.2"),sQuery(id+"F0.wireOp",EDGE,"E11.28.3"),sQuery(id+"F0.wireOp",EDGE,"E11.28.4"),sQuery(id+"F0.wireOp",EDGE,"E11.28.5"),sQuery(id+"F0.wireOp",EDGE,"E11.28.6"),sQuery(id+"F0.wireOp",EDGE,"E11.29.0"),sQuery(id+"F0.wireOp",EDGE,"E11.29.1"),sQuery(id+"F0.wireOp",EDGE,"E11.29.2"),sQuery(id+"F0.wireOp",EDGE,"E11.29.3"),sQuery(id+"F0.wireOp",EDGE,"E11.29.4"),sQuery(id+"F0.wireOp",EDGE,"E11.29.5"),sQuery(id+"F0.wireOp",EDGE,"E11.29.6"),sQuery(id+"F0.wireOp",EDGE,"E11.30.0"),sQuery(id+"F0.wireOp",EDGE,"E11.30.1"),sQuery(id+"F0.wireOp",EDGE,"E11.30.2"),sQuery(id+"F0.wireOp",EDGE,"E11.30.3"),sQuery(id+"F0.wireOp",EDGE,"E11.30.4"),sQuery(id+"F0.wireOp",EDGE,"E11.30.5"),sQuery(id+"F0.wireOp",EDGE,"E11.30.6"),sQuery(id+"F0.wireOp",EDGE,"E11.31.0"),sQuery(id+"F0.wireOp",EDGE,"E11.31.1"),sQuery(id+"F0.wireOp",EDGE,"E11.31.2"),sQuery(id+"F0.wireOp",EDGE,"E11.31.3"),sQuery(id+"F0.wireOp",EDGE,"E11.31.4"),sQuery(id+"F0.wireOp",EDGE,"E11.31.5"),sQuery(id+"F0.wireOp",EDGE,"E11.31.6"),sQuery(id+"F0.wireOp",EDGE,"E11.32.0"),sQuery(id+"F0.wireOp",EDGE,"E11.32.1"),sQuery(id+"F0.wireOp",EDGE,"E11.32.2"),sQuery(id+"F0.wireOp",EDGE,"E11.32.3"),sQuery(id+"F0.wireOp",EDGE,"E11.32.4"),sQuery(id+"F0.wireOp",EDGE,"E11.32.5"),sQuery(id+"F0.wireOp",EDGE,"E11.32.6"),sQuery(id+"F0.wireOp",EDGE,"E11.33.0"),sQuery(id+"F0.wireOp",EDGE,"E11.33.1"),sQuery(id+"F0.wireOp",EDGE,"E11.33.2"),sQuery(id+"F0.wireOp",EDGE,"E11.33.3"),sQuery(id+"F0.wireOp",EDGE,"E11.33.4"),sQuery(id+"F0.wireOp",EDGE,"E11.33.5"),sQuery(id+"F0.wireOp",EDGE,"E11.33.6"),sQuery(id+"F0.wireOp",EDGE,"E11.34.0"),sQuery(id+"F0.wireOp",EDGE,"E11.34.1"),sQuery(id+"F0.wireOp",EDGE,"E11.34.2"),sQuery(id+"F0.wireOp",EDGE,"E11.34.3"),sQuery(id+"F0.wireOp",EDGE,"E11.34.4"),sQuery(id+"F0.wireOp",EDGE,"E11.34.5"),sQuery(id+"F0.wireOp",EDGE,"E11.34.6"),sQuery(id+"F0.wireOp",EDGE,"E11.35.0"),sQuery(id+"F0.wireOp",EDGE,"E11.35.1"),sQuery(id+"F0.wireOp",EDGE,"E11.35.2"),sQuery(id+"F0.wireOp",EDGE,"E11.35.3"),sQuery(id+"F0.wireOp",EDGE,"E11.35.4"),sQuery(id+"F0.wireOp",EDGE,"E11.35.5"),sQuery(id+"F0.wireOp",EDGE,"E11.35.6"),sQuery(id+"F0.wireOp",EDGE,"E11.36.0"),sQuery(id+"F0.wireOp",EDGE,"E11.36.1"),sQuery(id+"F0.wireOp",EDGE,"E11.36.2"),sQuery(id+"F0.wireOp",EDGE,"E11.36.3"),sQuery(id+"F0.wireOp",EDGE,"E11.36.4"),sQuery(id+"F0.wireOp",EDGE,"E11.36.5"),sQuery(id+"F0.wireOp",EDGE,"E11.36.6"),sQuery(id+"F0.wireOp",EDGE,"E11.37.0"),sQuery(id+"F0.wireOp",EDGE,"E11.37.1"),sQuery(id+"F0.wireOp",EDGE,"E11.37.2"),sQuery(id+"F0.wireOp",EDGE,"E11.37.3"),sQuery(id+"F0.wireOp",EDGE,"E11.37.4"),sQuery(id+"F0.wireOp",EDGE,"E11.37.5"),sQuery(id+"F0.wireOp",EDGE,"E11.37.6"),sQuery(id+"F0.wireOp",EDGE,"E11.38.0"),sQuery(id+"F0.wireOp",EDGE,"E11.38.1"),sQuery(id+"F0.wireOp",EDGE,"E11.38.2"),sQuery(id+"F0.wireOp",EDGE,"E11.38.3"),sQuery(id+"F0.wireOp",EDGE,"E11.38.4"),sQuery(id+"F0.wireOp",EDGE,"E11.38.5"),sQuery(id+"F0.wireOp",EDGE,"E11.38.6"),sQuery(id+"F0.wireOp",EDGE,"E11.39.0"),sQuery(id+"F0.wireOp",EDGE,"E11.39.1"),sQuery(id+"F0.wireOp",EDGE,"E11.39.2"),sQuery(id+"F0.wireOp",EDGE,"E11.39.3"),sQuery(id+"F0.wireOp",EDGE,"E11.39.4"),sQuery(id+"F0.wireOp",EDGE,"E11.39.5"),sQuery(id+"F0.wireOp",EDGE,"E11.39.6"),sQuery(id+"F0.wireOp",EDGE,"E11.40.0"),sQuery(id+"F0.wireOp",EDGE,"E11.40.1"),sQuery(id+"F0.wireOp",EDGE,"E11.40.2"),sQuery(id+"F0.wireOp",EDGE,"E11.40.3"),sQuery(id+"F0.wireOp",EDGE,"E11.40.4"),sQuery(id+"F0.wireOp",EDGE,"E11.40.5"),sQuery(id+"F0.wireOp",EDGE,"E11.40.6"),sQuery(id+"F0.wireOp",EDGE,"E11.41.0"),sQuery(id+"F0.wireOp",EDGE,"E11.41.1"),sQuery(id+"F0.wireOp",EDGE,"E11.41.2"),sQuery(id+"F0.wireOp",EDGE,"E11.41.3"),sQuery(id+"F0.wireOp",EDGE,"E11.41.4"),sQuery(id+"F0.wireOp",EDGE,"E11.41.5"),sQuery(id+"F0.wireOp",EDGE,"E11.41.6"),sQuery(id+"F0.wireOp",EDGE,"E11.42.0"),sQuery(id+"F0.wireOp",EDGE,"E11.42.1"),sQuery(id+"F0.wireOp",EDGE,"E11.42.2"),sQuery(id+"F0.wireOp",EDGE,"E11.42.3"),sQuery(id+"F0.wireOp",EDGE,"E11.42.4"),sQuery(id+"F0.wireOp",EDGE,"E11.42.5"),sQuery(id+"F0.wireOp",EDGE,"E11.42.6"),sQuery(id+"F0.wireOp",EDGE,"E11.43.0"),sQuery(id+"F0.wireOp",EDGE,"E11.43.1"),sQuery(id+"F0.wireOp",EDGE,"E11.43.2"),sQuery(id+"F0.wireOp",EDGE,"E11.43.3"),sQuery(id+"F0.wireOp",EDGE,"E11.43.4"),sQuery(id+"F0.wireOp",EDGE,"E11.43.5"),sQuery(id+"F0.wireOp",EDGE,"E11.43.6"),sQuery(id+"F0.wireOp",EDGE,"E11.44.0"),sQuery(id+"F0.wireOp",EDGE,"E11.44.1"),sQuery(id+"F0.wireOp",EDGE,"E11.44.2"),sQuery(id+"F0.wireOp",EDGE,"E11.44.3"),sQuery(id+"F0.wireOp",EDGE,"E11.44.4"),sQuery(id+"F0.wireOp",EDGE,"E11.44.5"),sQuery(id+"F0.wireOp",EDGE,"E11.44.6"),sQuery(id+"F0.wireOp",EDGE,"E11.45.0"),sQuery(id+"F0.wireOp",EDGE,"E11.45.1"),sQuery(id+"F0.wireOp",EDGE,"E11.45.2"),sQuery(id+"F0.wireOp",EDGE,"E11.45.3"),sQuery(id+"F0.wireOp",EDGE,"E11.45.4"),sQuery(id+"F0.wireOp",EDGE,"E11.45.5"),sQuery(id+"F0.wireOp",EDGE,"E11.45.6"),sQuery(id+"F0.wireOp",EDGE,"E11.46.0"),sQuery(id+"F0.wireOp",EDGE,"E11.46.1"),sQuery(id+"F0.wireOp",EDGE,"E11.46.2"),sQuery(id+"F0.wireOp",EDGE,"E11.46.3"),sQuery(id+"F0.wireOp",EDGE,"E11.46.4"),sQuery(id+"F0.wireOp",EDGE,"E11.46.5"),sQuery(id+"F0.wireOp",EDGE,"E11.46.6"),sQuery(id+"F0.wireOp",EDGE,"E11.47.0"),sQuery(id+"F0.wireOp",EDGE,"E11.47.1"),sQuery(id+"F0.wireOp",EDGE,"E11.47.2"),sQuery(id+"F0.wireOp",EDGE,"E11.47.3"),sQuery(id+"F0.wireOp",EDGE,"E11.47.4"),sQuery(id+"F0.wireOp",EDGE,"E11.47.5"),sQuery(id+"F0.wireOp",EDGE,"E11.47.6"),sQuery(id+"F0.wireOp",EDGE,"E11.48.0"),sQuery(id+"F0.wireOp",EDGE,"E11.48.1"),sQuery(id+"F0.wireOp",EDGE,"E11.48.2"),sQuery(id+"F0.wireOp",EDGE,"E11.48.3"),sQuery(id+"F0.wireOp",EDGE,"E11.48.4"),sQuery(id+"F0.wireOp",EDGE,"E11.48.5"),sQuery(id+"F0.wireOp",EDGE,"E11.48.6"),sQuery(id+"F0.wireOp",EDGE,"E11.49.0"),sQuery(id+"F0.wireOp",EDGE,"E11.49.1"),sQuery(id+"F0.wireOp",EDGE,"E11.49.2"),sQuery(id+"F0.wireOp",EDGE,"E11.49.3"),sQuery(id+"F0.wireOp",EDGE,"E11.49.4"),sQuery(id+"F0.wireOp",EDGE,"E11.49.5"),sQuery(id+"F0.wireOp",EDGE,"E11.49.6"),sQuery(id+"F0.wireOp",EDGE,"E11.50.0"),sQuery(id+"F0.wireOp",EDGE,"E11.50.1"),sQuery(id+"F0.wireOp",EDGE,"E11.50.2"),sQuery(id+"F0.wireOp",EDGE,"E11.50.3"),sQuery(id+"F0.wireOp",EDGE,"E11.50.4"),sQuery(id+"F0.wireOp",EDGE,"E11.50.5"),sQuery(id+"F0.wireOp",EDGE,"E11.50.6"),sQuery(id+"F0.wireOp",EDGE,"E11.51.0"),sQuery(id+"F0.wireOp",EDGE,"E11.51.1"),sQuery(id+"F0.wireOp",EDGE,"E11.51.2"),sQuery(id+"F0.wireOp",EDGE,"E11.51.3"),sQuery(id+"F0.wireOp",EDGE,"E11.51.4"),sQuery(id+"F0.wireOp",EDGE,"E11.51.5"),sQuery(id+"F0.wireOp",EDGE,"E11.51.6"),sQuery(id+"F0.wireOp",EDGE,"E11.52.0"),sQuery(id+"F0.wireOp",EDGE,"E11.52.1"),sQuery(id+"F0.wireOp",EDGE,"E11.52.2"),sQuery(id+"F0.wireOp",EDGE,"E11.52.3"),sQuery(id+"F0.wireOp",EDGE,"E11.52.4"),sQuery(id+"F0.wireOp",EDGE,"E11.52.5"),sQuery(id+"F0.wireOp",EDGE,"E11.52.6"),sQuery(id+"F0.wireOp",EDGE,"E11.53.0"),sQuery(id+"F0.wireOp",EDGE,"E11.53.1"),sQuery(id+"F0.wireOp",EDGE,"E11.53.2"),sQuery(id+"F0.wireOp",EDGE,"E11.53.3"),sQuery(id+"F0.wireOp",EDGE,"E11.53.4"),sQuery(id+"F0.wireOp",EDGE,"E11.53.5"),sQuery(id+"F0.wireOp",EDGE,"E11.53.6"),sQuery(id+"F0.wireOp",EDGE,"E11.54.0"),sQuery(id+"F0.wireOp",EDGE,"E11.54.1"),sQuery(id+"F0.wireOp",EDGE,"E11.54.2"),sQuery(id+"F0.wireOp",EDGE,"E11.54.3"),sQuery(id+"F0.wireOp",EDGE,"E11.54.4"),sQuery(id+"F0.wireOp",EDGE,"E11.54.5"),sQuery(id+"F0.wireOp",EDGE,"E11.54.6"),sQuery(id+"F0.wireOp",EDGE,"E11.55.0"),sQuery(id+"F0.wireOp",EDGE,"E11.55.1"),sQuery(id+"F0.wireOp",EDGE,"E11.55.2"),sQuery(id+"F0.wireOp",EDGE,"E11.55.3"),sQuery(id+"F0.wireOp",EDGE,"E11.55.4"),sQuery(id+"F0.wireOp",EDGE,"E11.55.5"),sQuery(id+"F0.wireOp",EDGE,"E11.55.6"),sQuery(id+"F0.wireOp",EDGE,"E11.56.0"),sQuery(id+"F0.wireOp",EDGE,"E11.56.1"),sQuery(id+"F0.wireOp",EDGE,"E11.56.2"),sQuery(id+"F0.wireOp",EDGE,"E11.56.3"),sQuery(id+"F0.wireOp",EDGE,"E11.56.4"),sQuery(id+"F0.wireOp",EDGE,"E11.56.5"),sQuery(id+"F0.wireOp",EDGE,"E11.56.6"),sQuery(id+"F0.wireOp",EDGE,"E11.57.0"),sQuery(id+"F0.wireOp",EDGE,"E11.57.1"),sQuery(id+"F0.wireOp",EDGE,"E11.57.2"),sQuery(id+"F0.wireOp",EDGE,"E11.57.3"),sQuery(id+"F0.wireOp",EDGE,"E11.57.4"),sQuery(id+"F0.wireOp",EDGE,"E11.57.5"),sQuery(id+"F0.wireOp",EDGE,"E11.57.6"),sQuery(id+"F0.wireOp",EDGE,"E11.58.0"),sQuery(id+"F0.wireOp",EDGE,"E11.58.1"),sQuery(id+"F0.wireOp",EDGE,"E11.58.2"),sQuery(id+"F0.wireOp",EDGE,"E11.58.3"),sQuery(id+"F0.wireOp",EDGE,"E11.58.4"),sQuery(id+"F0.wireOp",EDGE,"E11.58.5"),sQuery(id+"F0.wireOp",EDGE,"E11.58.6"),sQuery(id+"F0.wireOp",EDGE,"E11.59.0"),sQuery(id+"F0.wireOp",EDGE,"E11.59.1"),sQuery(id+"F0.wireOp",EDGE,"E11.59.2"),sQuery(id+"F0.wireOp",EDGE,"E11.59.3"),sQuery(id+"F0.wireOp",EDGE,"E11.59.4"),sQuery(id+"F0.wireOp",EDGE,"E11.59.5"),sQuery(id+"F0.wireOp",EDGE,"E11.59.6"),sQuery(id+"F0.wireOp",EDGE,"E11.60.0"),sQuery(id+"F0.wireOp",EDGE,"E11.60.1"),sQuery(id+"F0.wireOp",EDGE,"E11.60.2"),sQuery(id+"F0.wireOp",EDGE,"E11.60.3"),sQuery(id+"F0.wireOp",EDGE,"E11.60.4"),sQuery(id+"F0.wireOp",EDGE,"E11.60.5"),sQuery(id+"F0.wireOp",EDGE,"E11.60.6"),sQuery(id+"F0.wireOp",EDGE,"E11.61.0"),sQuery(id+"F0.wireOp",EDGE,"E11.61.1"),sQuery(id+"F0.wireOp",EDGE,"E11.61.2"),sQuery(id+"F0.wireOp",EDGE,"E11.61.3"),sQuery(id+"F0.wireOp",EDGE,"E11.61.4"),sQuery(id+"F0.wireOp",EDGE,"E11.61.5"),sQuery(id+"F0.wireOp",EDGE,"E11.61.6"),sQuery(id+"F0.wireOp",EDGE,"E11.62.0"),sQuery(id+"F0.wireOp",EDGE,"E11.62.1"),sQuery(id+"F0.wireOp",EDGE,"E11.62.2"),sQuery(id+"F0.wireOp",EDGE,"E11.62.3"),sQuery(id+"F0.wireOp",EDGE,"E11.62.4"),sQuery(id+"F0.wireOp",EDGE,"E11.62.5"),sQuery(id+"F0.wireOp",EDGE,"E11.62.6"),sQuery(id+"F0.wireOp",EDGE,"E11.63.0"),sQuery(id+"F0.wireOp",EDGE,"E11.63.1"),sQuery(id+"F0.wireOp",EDGE,"E11.63.2"),sQuery(id+"F0.wireOp",EDGE,"E11.63.3"),sQuery(id+"F0.wireOp",EDGE,"E11.63.4"),sQuery(id+"F0.wireOp",EDGE,"E11.63.5"),sQuery(id+"F0.wireOp",EDGE,"E11.63.6"),sQuery(id+"F0.wireOp",EDGE,"E11.64.0"),sQuery(id+"F0.wireOp",EDGE,"E11.64.1"),sQuery(id+"F0.wireOp",EDGE,"E11.64.2"),sQuery(id+"F0.wireOp",EDGE,"E11.64.3"),sQuery(id+"F0.wireOp",EDGE,"E11.64.4"),sQuery(id+"F0.wireOp",EDGE,"E11.64.5"),sQuery(id+"F0.wireOp",EDGE,"E11.64.6"),sQuery(id+"F0.wireOp",EDGE,"E11.65.0"),sQuery(id+"F0.wireOp",EDGE,"E11.65.1"),sQuery(id+"F0.wireOp",EDGE,"E11.65.2"),sQuery(id+"F0.wireOp",EDGE,"E11.65.3"),sQuery(id+"F0.wireOp",EDGE,"E11.65.4"),sQuery(id+"F0.wireOp",EDGE,"E11.65.5"),sQuery(id+"F0.wireOp",EDGE,"E11.65.6"),sQuery(id+"F0.wireOp",EDGE,"E11.66.0"),sQuery(id+"F0.wireOp",EDGE,"E11.66.1"),sQuery(id+"F0.wireOp",EDGE,"E11.66.2"),sQuery(id+"F0.wireOp",EDGE,"E11.66.3"),sQuery(id+"F0.wireOp",EDGE,"E11.66.4"),sQuery(id+"F0.wireOp",EDGE,"E11.66.5"),sQuery(id+"F0.wireOp",EDGE,"E11.66.6"),sQuery(id+"F0.wireOp",EDGE,"E11.67.0"),sQuery(id+"F0.wireOp",EDGE,"E11.67.1"),sQuery(id+"F0.wireOp",EDGE,"E11.67.2"),sQuery(id+"F0.wireOp",EDGE,"E11.67.3"),sQuery(id+"F0.wireOp",EDGE,"E11.67.4"),sQuery(id+"F0.wireOp",EDGE,"E11.67.5"),sQuery(id+"F0.wireOp",EDGE,"E11.67.6"),sQuery(id+"F0.wireOp",EDGE,"E11.68.0"),sQuery(id+"F0.wireOp",EDGE,"E11.68.1"),sQuery(id+"F0.wireOp",EDGE,"E11.68.2"),sQuery(id+"F0.wireOp",EDGE,"E11.68.3"),sQuery(id+"F0.wireOp",EDGE,"E11.68.4"),sQuery(id+"F0.wireOp",EDGE,"E11.68.5"),sQuery(id+"F0.wireOp",EDGE,"E11.68.6"),sQuery(id+"F0.wireOp",EDGE,"E11.69.0"),sQuery(id+"F0.wireOp",EDGE,"E11.69.1"),sQuery(id+"F0.wireOp",EDGE,"E11.69.2"),sQuery(id+"F0.wireOp",EDGE,"E11.69.3"),sQuery(id+"F0.wireOp",EDGE,"E11.69.4"),sQuery(id+"F0.wireOp",EDGE,"E11.69.5"),sQuery(id+"F0.wireOp",EDGE,"E11.69.6"),sQuery(id+"F0.wireOp",EDGE,"E11.70.0"),sQuery(id+"F0.wireOp",EDGE,"E11.70.1"),sQuery(id+"F0.wireOp",EDGE,"E11.70.2"),sQuery(id+"F0.wireOp",EDGE,"E11.70.3"),sQuery(id+"F0.wireOp",EDGE,"E11.70.4"),sQuery(id+"F0.wireOp",EDGE,"E11.70.5"),sQuery(id+"F0.wireOp",EDGE,"E11.70.6"),sQuery(id+"F0.wireOp",EDGE,"E11.71.0"),sQuery(id+"F0.wireOp",EDGE,"E11.71.1"),sQuery(id+"F0.wireOp",EDGE,"E11.71.2"),sQuery(id+"F0.wireOp",EDGE,"E11.71.3"),sQuery(id+"F0.wireOp",EDGE,"E11.71.4"),sQuery(id+"F0.wireOp",EDGE,"E11.71.5"),sQuery(id+"F0.wireOp",EDGE,"E11.71.6"),sQuery(id+"F0.wireOp",EDGE,"E11.72.0"),sQuery(id+"F0.wireOp",EDGE,"E11.72.1"),sQuery(id+"F0.wireOp",EDGE,"E11.72.2"),sQuery(id+"F0.wireOp",EDGE,"E11.72.3"),sQuery(id+"F0.wireOp",EDGE,"E11.72.4"),sQuery(id+"F0.wireOp",EDGE,"E11.72.5"),sQuery(id+"F0.wireOp",EDGE,"E11.72.6"),sQuery(id+"F0.wireOp",EDGE,"E11.73.0"),sQuery(id+"F0.wireOp",EDGE,"E11.73.1"),sQuery(id+"F0.wireOp",EDGE,"E11.73.2"),sQuery(id+"F0.wireOp",EDGE,"E11.73.3"),sQuery(id+"F0.wireOp",EDGE,"E11.73.4"),sQuery(id+"F0.wireOp",EDGE,"E11.73.5"),sQuery(id+"F0.wireOp",EDGE,"E11.73.6"),sQuery(id+"F0.wireOp",EDGE,"E11.74.0"),sQuery(id+"F0.wireOp",EDGE,"E11.74.1"),sQuery(id+"F0.wireOp",EDGE,"E11.74.2"),sQuery(id+"F0.wireOp",EDGE,"E11.74.3"),sQuery(id+"F0.wireOp",EDGE,"E11.74.4"),sQuery(id+"F0.wireOp",EDGE,"E11.74.5"),sQuery(id+"F0.wireOp",EDGE,"E11.74.6"),sQuery(id+"F0.wireOp",EDGE,"E11.75.0"),sQuery(id+"F0.wireOp",EDGE,"E11.75.1"),sQuery(id+"F0.wireOp",EDGE,"E11.75.2"),sQuery(id+"F0.wireOp",EDGE,"E11.75.3"),sQuery(id+"F0.wireOp",EDGE,"E11.75.4"),sQuery(id+"F0.wireOp",EDGE,"E11.75.5"),sQuery(id+"F0.wireOp",EDGE,"E11.75.6"),sQuery(id+"F0.wireOp",EDGE,"E11.76.0"),sQuery(id+"F0.wireOp",EDGE,"E11.76.1"),sQuery(id+"F0.wireOp",EDGE,"E11.76.2"),sQuery(id+"F0.wireOp",EDGE,"E11.76.3"),sQuery(id+"F0.wireOp",EDGE,"E11.76.4"),sQuery(id+"F0.wireOp",EDGE,"E11.76.5"),sQuery(id+"F0.wireOp",EDGE,"E11.76.6"),sQuery(id+"F0.wireOp",EDGE,"E11.77.0"),sQuery(id+"F0.wireOp",EDGE,"E11.77.1"),sQuery(id+"F0.wireOp",EDGE,"E11.77.2"),sQuery(id+"F0.wireOp",EDGE,"E11.77.3"),sQuery(id+"F0.wireOp",EDGE,"E11.77.4"),sQuery(id+"F0.wireOp",EDGE,"E11.77.5"),sQuery(id+"F0.wireOp",EDGE,"E11.77.6"),sQuery(id+"F0.wireOp",EDGE,"E11.78.0"),sQuery(id+"F0.wireOp",EDGE,"E11.78.1"),sQuery(id+"F0.wireOp",EDGE,"E11.78.2"),sQuery(id+"F0.wireOp",EDGE,"E11.78.3"),sQuery(id+"F0.wireOp",EDGE,"E11.78.4"),sQuery(id+"F0.wireOp",EDGE,"E11.78.5"),sQuery(id+"F0.wireOp",EDGE,"E11.78.6"),sQuery(id+"F0.wireOp",EDGE,"E11.79.0"),sQuery(id+"F0.wireOp",EDGE,"E11.79.1"),sQuery(id+"F0.wireOp",EDGE,"E11.79.2"),sQuery(id+"F0.wireOp",EDGE,"E11.79.3"),sQuery(id+"F0.wireOp",EDGE,"E11.79.4"),sQuery(id+"F0.wireOp",EDGE,"E11.79.5"),sQuery(id+"F0.wireOp",EDGE,"E11.79.6"),sQuery(id+"F0.wireOp",EDGE,"E11.80.0"),sQuery(id+"F0.wireOp",EDGE,"E11.80.1"),sQuery(id+"F0.wireOp",EDGE,"E11.80.2"),sQuery(id+"F0.wireOp",EDGE,"E11.80.3"),sQuery(id+"F0.wireOp",EDGE,"E11.80.4"),sQuery(id+"F0.wireOp",EDGE,"E11.80.5"),sQuery(id+"F0.wireOp",EDGE,"E11.80.6"),sQuery(id+"F0.wireOp",EDGE,"E11.81.0"),sQuery(id+"F0.wireOp",EDGE,"E11.81.1"),sQuery(id+"F0.wireOp",EDGE,"E11.81.2"),sQuery(id+"F0.wireOp",EDGE,"E11.81.3"),sQuery(id+"F0.wireOp",EDGE,"E11.81.4"),sQuery(id+"F0.wireOp",EDGE,"E11.81.5"),sQuery(id+"F0.wireOp",EDGE,"E11.81.6"),sQuery(id+"F0.wireOp",EDGE,"E11.82.0"),sQuery(id+"F0.wireOp",EDGE,"E11.82.1"),sQuery(id+"F0.wireOp",EDGE,"E11.82.2"),sQuery(id+"F0.wireOp",EDGE,"E11.82.3"),sQuery(id+"F0.wireOp",EDGE,"E11.82.4"),sQuery(id+"F0.wireOp",EDGE,"E11.82.5"),sQuery(id+"F0.wireOp",EDGE,"E11.82.6"),sQuery(id+"F0.wireOp",EDGE,"E11.83.0"),sQuery(id+"F0.wireOp",EDGE,"E11.83.1"),sQuery(id+"F0.wireOp",EDGE,"E11.83.2"),sQuery(id+"F0.wireOp",EDGE,"E11.83.3"),sQuery(id+"F0.wireOp",EDGE,"E11.83.4"),sQuery(id+"F0.wireOp",EDGE,"E11.83.5"),sQuery(id+"F0.wireOp",EDGE,"E11.83.6"),sQuery(id+"F0.wireOp",EDGE,"E11.84.0"),sQuery(id+"F0.wireOp",EDGE,"E11.84.1"),sQuery(id+"F0.wireOp",EDGE,"E11.84.2"),sQuery(id+"F0.wireOp",EDGE,"E11.84.3"),sQuery(id+"F0.wireOp",EDGE,"E11.84.4"),sQuery(id+"F0.wireOp",EDGE,"E11.84.5"),sQuery(id+"F0.wireOp",EDGE,"E11.84.6"),sQuery(id+"F0.wireOp",EDGE,"E11.85.0"),sQuery(id+"F0.wireOp",EDGE,"E11.85.1"),sQuery(id+"F0.wireOp",EDGE,"E11.85.2"),sQuery(id+"F0.wireOp",EDGE,"E11.85.3"),sQuery(id+"F0.wireOp",EDGE,"E11.85.4"),sQuery(id+"F0.wireOp",EDGE,"E11.85.5"),sQuery(id+"F0.wireOp",EDGE,"E11.85.6"),sQuery(id+"F0.wireOp",EDGE,"E11.86.0"),sQuery(id+"F0.wireOp",EDGE,"E11.86.1"),sQuery(id+"F0.wireOp",EDGE,"E11.86.2"),sQuery(id+"F0.wireOp",EDGE,"E11.86.3"),sQuery(id+"F0.wireOp",EDGE,"E11.86.4"),sQuery(id+"F0.wireOp",EDGE,"E11.86.5"),sQuery(id+"F0.wireOp",EDGE,"E11.86.6"),sQuery(id+"F0.wireOp",EDGE,"E11.87.0"),sQuery(id+"F0.wireOp",EDGE,"E11.87.1"),sQuery(id+"F0.wireOp",EDGE,"E11.87.2"),sQuery(id+"F0.wireOp",EDGE,"E11.87.3"),sQuery(id+"F0.wireOp",EDGE,"E11.87.4"),sQuery(id+"F0.wireOp",EDGE,"E11.87.5"),sQuery(id+"F0.wireOp",EDGE,"E11.87.6"),sQuery(id+"F0.wireOp",EDGE,"E11.88.0"),sQuery(id+"F0.wireOp",EDGE,"E11.88.1"),sQuery(id+"F0.wireOp",EDGE,"E11.88.2"),sQuery(id+"F0.wireOp",EDGE,"E11.88.3"),sQuery(id+"F0.wireOp",EDGE,"E11.88.4"),sQuery(id+"F0.wireOp",EDGE,"E11.88.5"),sQuery(id+"F0.wireOp",EDGE,"E11.88.6"),sQuery(id+"F0.wireOp",EDGE,"E11.89.0"),sQuery(id+"F0.wireOp",EDGE,"E11.89.1"),sQuery(id+"F0.wireOp",EDGE,"E11.89.2"),sQuery(id+"F0.wireOp",EDGE,"E11.89.3"),sQuery(id+"F0.wireOp",EDGE,"E11.89.4"),sQuery(id+"F0.wireOp",EDGE,"E11.89.5"),sQuery(id+"F0.wireOp",EDGE,"E11.89.6"),sQuery(id+"F0.wireOp",EDGE,"E11.90.0"),sQuery(id+"F0.wireOp",EDGE,"E11.90.1"),sQuery(id+"F0.wireOp",EDGE,"E11.90.2"),sQuery(id+"F0.wireOp",EDGE,"E11.90.3"),sQuery(id+"F0.wireOp",EDGE,"E11.90.4"),sQuery(id+"F0.wireOp",EDGE,"E11.90.5"),sQuery(id+"F0.wireOp",EDGE,"E11.90.6"),sQuery(id+"F0.wireOp",EDGE,"E11.91.0"),sQuery(id+"F0.wireOp",EDGE,"E11.91.1"),sQuery(id+"F0.wireOp",EDGE,"E11.91.2"),sQuery(id+"F0.wireOp",EDGE,"E11.91.3"),sQuery(id+"F0.wireOp",EDGE,"E11.91.4"),sQuery(id+"F0.wireOp",EDGE,"E11.91.5"),sQuery(id+"F0.wireOp",EDGE,"E11.91.6"),sQuery(id+"F0.wireOp",EDGE,"E11.92.0"),sQuery(id+"F0.wireOp",EDGE,"E11.92.1"),sQuery(id+"F0.wireOp",EDGE,"E11.92.2"),sQuery(id+"F0.wireOp",EDGE,"E11.92.3"),sQuery(id+"F0.wireOp",EDGE,"E11.92.4"),sQuery(id+"F0.wireOp",EDGE,"E11.92.5"),sQuery(id+"F0.wireOp",EDGE,"E11.92.6"),sQuery(id+"F0.wireOp",EDGE,"E11.93.0"),sQuery(id+"F0.wireOp",EDGE,"E11.93.1"),sQuery(id+"F0.wireOp",EDGE,"E11.93.2"),sQuery(id+"F0.wireOp",EDGE,"E11.93.3"),sQuery(id+"F0.wireOp",EDGE,"E11.93.4"),sQuery(id+"F0.wireOp",EDGE,"E11.93.5"),sQuery(id+"F0.wireOp",EDGE,"E11.93.6"),sQuery(id+"F0.wireOp",EDGE,"E11.94.0"),sQuery(id+"F0.wireOp",EDGE,"E11.94.1"),sQuery(id+"F0.wireOp",EDGE,"E11.94.2"),sQuery(id+"F0.wireOp",EDGE,"E11.94.3"),sQuery(id+"F0.wireOp",EDGE,"E11.94.4"),sQuery(id+"F0.wireOp",EDGE,"E11.94.5"),sQuery(id+"F0.wireOp",EDGE,"E11.94.6"),sQuery(id+"F0.wireOp",EDGE,"E11.95.0"),sQuery(id+"F0.wireOp",EDGE,"E11.95.1"),sQuery(id+"F0.wireOp",EDGE,"E11.95.2"),sQuery(id+"F0.wireOp",EDGE,"E11.95.3"),sQuery(id+"F0.wireOp",EDGE,"E11.95.4"),sQuery(id+"F0.wireOp",EDGE,"E11.95.5"),sQuery(id+"F0.wireOp",EDGE,"E11.95.6"),sQuery(id+"F0.wireOp",EDGE,"E11.96.0"),sQuery(id+"F0.wireOp",EDGE,"E11.96.1"),sQuery(id+"F0.wireOp",EDGE,"E11.96.2"),sQuery(id+"F0.wireOp",EDGE,"E11.96.3"),sQuery(id+"F0.wireOp",EDGE,"E11.96.4"),sQuery(id+"F0.wireOp",EDGE,"E11.96.5"),sQuery(id+"F0.wireOp",EDGE,"E11.96.6"),sQuery(id+"F0.wireOp",EDGE,"E11.97.0"),sQuery(id+"F0.wireOp",EDGE,"E11.97.1"),sQuery(id+"F0.wireOp",EDGE,"E11.97.2"),sQuery(id+"F0.wireOp",EDGE,"E11.97.3"),sQuery(id+"F0.wireOp",EDGE,"E11.97.4"),sQuery(id+"F0.wireOp",EDGE,"E11.97.5"),sQuery(id+"F0.wireOp",EDGE,"E11.97.6"),sQuery(id+"F0.wireOp",EDGE,"E11.98.0"),sQuery(id+"F0.wireOp",EDGE,"E11.98.1"),sQuery(id+"F0.wireOp",EDGE,"E11.98.2"),sQuery(id+"F0.wireOp",EDGE,"E11.98.3"),sQuery(id+"F0.wireOp",EDGE,"E11.98.4"),sQuery(id+"F0.wireOp",EDGE,"E11.98.5"),sQuery(id+"F0.wireOp",EDGE,"E11.98.6"),sQuery(id+"F0.wireOp",EDGE,"E11.99.0"),sQuery(id+"F0.wireOp",EDGE,"E11.99.1"),sQuery(id+"F0.wireOp",EDGE,"E11.99.2"),sQuery(id+"F0.wireOp",EDGE,"E11.99.3"),sQuery(id+"F0.wireOp",EDGE,"E11.99.4"),sQuery(id+"F0.wireOp",EDGE,"E11.99.5"),sQuery(id+"F0.wireOp",EDGE,"E11.99.6"),sQuery(id+"F0.wireOp",EDGE,"E18"),sQuery(id+"F0.wireOp",EDGE,"E19.trimOffspring"),sQuery(id+"F0.wireOp",EDGE,"E20.trimOffspring"),sQuery(id+"F0.wireOp",EDGE,"E21.trimOffspring"),sQuery(id+"F0.wireOp",EDGE,"E22.trimOffspring"),sQuery(id+"F0.wireOp",EDGE,"E23.trimOffspring"),sQuery(id+"F0.wireOp",EDGE,"E24.trimOffspring"),sQuery(id+"F0.wireOp",EDGE,"E25.trimOffspring"),sQuery(id+"F0.wireOp",EDGE,"E26.trimOffspring"),sQuery(id+"F0.wireOp",EDGE,"E27.trimOffspring"),sQuery(id+"F0.wireOp",EDGE,"E28.trimOffspring"),sQuery(id+"F0.wireOp",EDGE,"E29.trimOffspring"),sQuery(id+"F0.wireOp",EDGE,"E30.trimOffspring"),sQuery(id+"F0.wireOp",EDGE,"E31.trimOffspring"),sQuery(id+"F0.wireOp",EDGE,"E32.trimOffspring"),sQuery(id+"F0.wireOp",EDGE,"E33.trimOffspring"),sQuery(id+"F0.wireOp",EDGE,"E34.trimOffspring"),sQuery(id+"F0.wireOp",EDGE,"E35.trimOffspring"),sQuery(id+"F0.wireOp",EDGE,"E36.trimOffspring"),sQuery(id+"F0.wireOp",EDGE,"E37.trimOffspring"),sQuery(id+"F0.wireOp",EDGE,"E38.trimOffspring"),sQuery(id+"F0.wireOp",EDGE,"E39.trimOffspring"),sQuery(id+"F0.wireOp",EDGE,"E40.trimOffspring"),sQuery(id+"F0.wireOp",EDGE,"E41.trimOffspring"),sQuery(id+"F0.wireOp",EDGE,"E42.trimOffspring"),sQuery(id+"F0.wireOp",EDGE,"E43.trimOffspring"),sQuery(id+"F0.wireOp",EDGE,"E44.trimOffspring"),sQuery(id+"F0.wireOp",EDGE,"E45.trimOffspring"),sQuery(id+"F0.wireOp",EDGE,"E46.trimOffspring"),sQuery(id+"F0.wireOp",EDGE,"E47.trimOffspring"),sQuery(id+"F0.wireOp",EDGE,"E48.trimOffspring"),sQuery(id+"F0.wireOp",EDGE,"E49.trimOffspring"),sQuery(id+"F0.wireOp",EDGE,"E50.trimOffspring"),sQuery(id+"F0.wireOp",EDGE,"E51.trimOffspring"),sQuery(id+"F0.wireOp",EDGE,"E52.trimOffspring"),sQuery(id+"F0.wireOp",EDGE,"E53.trimOffspring"),sQuery(id+"F0.wireOp",EDGE,"E54.trimOffspring"),sQuery(id+"F0.wireOp",EDGE,"E55.trimOffspring"),sQuery(id+"F0.wireOp",EDGE,"E56.trimOffspring"),sQuery(id+"F0.wireOp",EDGE,"E57.trimOffspring"),sQuery(id+"F0.wireOp",EDGE,"E58.trimOffspring"),sQuery(id+"F0.wireOp",EDGE,"E59.trimOffspring"),sQuery(id+"F0.wireOp",EDGE,"E60.trimOffspring"),sQuery(id+"F0.wireOp",EDGE,"E61.trimOffspring"),sQuery(id+"F0.wireOp",EDGE,"E62.trimOffspring"),sQuery(id+"F0.wireOp",EDGE,"E63.trimOffspring"),sQuery(id+"F0.wireOp",EDGE,"E64.trimOffspring"),sQuery(id+"F0.wireOp",EDGE,"E65.trimOffspring"),sQuery(id+"F0.wireOp",EDGE,"E66.trimOffspring"),sQuery(id+"F0.wireOp",EDGE,"E67.trimOffspring"),sQuery(id+"F0.wireOp",EDGE,"E68.trimOffspring"),sQuery(id+"F0.wireOp",EDGE,"E69.trimOffspring"),sQuery(id+"F0.wireOp",EDGE,"E70.trimOffspring"),sQuery(id+"F0.wireOp",EDGE,"E71.trimOffspring"),sQuery(id+"F0.wireOp",EDGE,"E72.trimOffspring"),sQuery(id+"F0.wireOp",EDGE,"E73.trimOffspring"),sQuery(id+"F0.wireOp",EDGE,"E74.trimOffspring"),sQuery(id+"F0.wireOp",EDGE,"E75.trimOffspring"),sQuery(id+"F0.wireOp",EDGE,"E76.trimOffspring"),sQuery(id+"F0.wireOp",EDGE,"E77.trimOffspring"),sQuery(id+"F0.wireOp",EDGE,"E78.trimOffspring"),sQuery(id+"F0.wireOp",EDGE,"E79.trimOffspring"),sQuery(id+"F0.wireOp",EDGE,"E80.trimOffspring"),sQuery(id+"F0.wireOp",EDGE,"E81.trimOffspring"),sQuery(id+"F0.wireOp",EDGE,"E82.trimOffspring"),sQuery(id+"F0.wireOp",EDGE,"E83.trimOffspring"),sQuery(id+"F0.wireOp",EDGE,"E84.trimOffspring"),sQuery(id+"F0.wireOp",EDGE,"E85.trimOffspring"),sQuery(id+"F0.wireOp",EDGE,"E86.trimOffspring"),sQuery(id+"F0.wireOp",EDGE,"E87.trimOffspring"),sQuery(id+"F0.wireOp",EDGE,"E88.trimOffspring"),sQuery(id+"F0.wireOp",EDGE,"E89.trimOffspring"),sQuery(id+"F0.wireOp",EDGE,"E90.trimOffspring"),sQuery(id+"F0.wireOp",EDGE,"E91.trimOffspring"),sQuery(id+"F0.wireOp",EDGE,"E92.trimOffspring"),sQuery(id+"F0.wireOp",EDGE,"E93.trimOffspring"),sQuery(id+"F0.wireOp",EDGE,"E94.trimOffspring"),sQuery(id+"F0.wireOp",EDGE,"E95.trimOffspring"),sQuery(id+"F0.wireOp",EDGE,"E96.trimOffspring"),sQuery(id+"F0.wireOp",EDGE,"E97.trimOffspring"),sQuery(id+"F0.wireOp",EDGE,"E98.trimOffspring"),sQuery(id+"F0.wireOp",EDGE,"E99.trimOffspring"),sQuery(id+"F0.wireOp",EDGE,"E100.trimOffspring"),sQuery(id+"F0.wireOp",EDGE,"E101.trimOffspring"),sQuery(id+"F0.wireOp",EDGE,"E102.trimOffspring"),sQuery(id+"F0.wireOp",EDGE,"E103.trimOffspring"),sQuery(id+"F0.wireOp",EDGE,"E104.trimOffspring"),sQuery(id+"F0.wireOp",EDGE,"E105.trimOffspring"),sQuery(id+"F0.wireOp",EDGE,"E106.trimOffspring"),sQuery(id+"F0.wireOp",EDGE,"E107.trimOffspring"),sQuery(id+"F0.wireOp",EDGE,"E108.trimOffspring"),sQuery(id+"F0.wireOp",EDGE,"E109.trimOffspring"),sQuery(id+"F0.wireOp",EDGE,"E110.trimOffspring"),sQuery(id+"F0.wireOp",EDGE,"E111.trimOffspring"),sQuery(id+"F0.wireOp",EDGE,"E112.trimOffspring"),sQuery(id+"F0.wireOp",EDGE,"E113.trimOffspring"),sQuery(id+"F0.wireOp",EDGE,"E114.trimOffspring"),sQuery(id+"F0.wireOp",EDGE,"E115.trimOffspring"),sQuery(id+"F0.wireOp",EDGE,"E116.trimOffspring"),sQuery(id+"F0.wireOp",EDGE,"E117.trimOffspring")])],"isStart":true});
            chamfer(context, id + "F2", {"entities" : qUnion([Q0]), "width" : 0.5 * mm, "tangentPropagation" : true});
        }
        {
            var Q0;
            Q0=makeQuery(id+"F1.opExtrude","CAP_FACE",FACE,{"disambiguationData":[OSD([sQuery(id+"F0.wireOp",EDGE,"E4"),sQuery(id+"F0.wireOp",EDGE,"E5"),sQuery(id+"F0.wireOp",EDGE,"E6.filletArc"),sQuery(id+"F0.wireOp",EDGE,"E7.MirrorCS"),sQuery(id+"F0.wireOp",EDGE,"E8.MirrorCS"),sQuery(id+"F0.wireOp",EDGE,"E9.MirrorCS"),sQuery(id+"F0.wireOp",EDGE,"E10.filletArc"),sQuery(id+"F0.wireOp",EDGE,"E11.1.0"),sQuery(id+"F0.wireOp",EDGE,"E11.1.1"),sQuery(id+"F0.wireOp",EDGE,"E11.1.2"),sQuery(id+"F0.wireOp",EDGE,"E11.1.3"),sQuery(id+"F0.wireOp",EDGE,"E11.1.4"),sQuery(id+"F0.wireOp",EDGE,"E11.1.5"),sQuery(id+"F0.wireOp",EDGE,"E11.1.6"),sQuery(id+"F0.wireOp",EDGE,"E11.2.0"),sQuery(id+"F0.wireOp",EDGE,"E11.2.1"),sQuery(id+"F0.wireOp",EDGE,"E11.2.2"),sQuery(id+"F0.wireOp",EDGE,"E11.2.3"),sQuery(id+"F0.wireOp",EDGE,"E11.2.4"),sQuery(id+"F0.wireOp",EDGE,"E11.2.5"),sQuery(id+"F0.wireOp",EDGE,"E11.2.6"),sQuery(id+"F0.wireOp",EDGE,"E11.3.0"),sQuery(id+"F0.wireOp",EDGE,"E11.3.1"),sQuery(id+"F0.wireOp",EDGE,"E11.3.2"),sQuery(id+"F0.wireOp",EDGE,"E11.3.3"),sQuery(id+"F0.wireOp",EDGE,"E11.3.4"),sQuery(id+"F0.wireOp",EDGE,"E11.3.5"),sQuery(id+"F0.wireOp",EDGE,"E11.3.6"),sQuery(id+"F0.wireOp",EDGE,"E11.4.0"),sQuery(id+"F0.wireOp",EDGE,"E11.4.1"),sQuery(id+"F0.wireOp",EDGE,"E11.4.2"),sQuery(id+"F0.wireOp",EDGE,"E11.4.3"),sQuery(id+"F0.wireOp",EDGE,"E11.4.4"),sQuery(id+"F0.wireOp",EDGE,"E11.4.5"),sQuery(id+"F0.wireOp",EDGE,"E11.4.6"),sQuery(id+"F0.wireOp",EDGE,"E11.5.0"),sQuery(id+"F0.wireOp",EDGE,"E11.5.1"),sQuery(id+"F0.wireOp",EDGE,"E11.5.2"),sQuery(id+"F0.wireOp",EDGE,"E11.5.3"),sQuery(id+"F0.wireOp",EDGE,"E11.5.4"),sQuery(id+"F0.wireOp",EDGE,"E11.5.5"),sQuery(id+"F0.wireOp",EDGE,"E11.5.6"),sQuery(id+"F0.wireOp",EDGE,"E11.6.0"),sQuery(id+"F0.wireOp",EDGE,"E11.6.1"),sQuery(id+"F0.wireOp",EDGE,"E11.6.2"),sQuery(id+"F0.wireOp",EDGE,"E11.6.3"),sQuery(id+"F0.wireOp",EDGE,"E11.6.4"),sQuery(id+"F0.wireOp",EDGE,"E11.6.5"),sQuery(id+"F0.wireOp",EDGE,"E11.6.6"),sQuery(id+"F0.wireOp",EDGE,"E11.7.0"),sQuery(id+"F0.wireOp",EDGE,"E11.7.1"),sQuery(id+"F0.wireOp",EDGE,"E11.7.2"),sQuery(id+"F0.wireOp",EDGE,"E11.7.3"),sQuery(id+"F0.wireOp",EDGE,"E11.7.4"),sQuery(id+"F0.wireOp",EDGE,"E11.7.5"),sQuery(id+"F0.wireOp",EDGE,"E11.7.6"),sQuery(id+"F0.wireOp",EDGE,"E11.8.0"),sQuery(id+"F0.wireOp",EDGE,"E11.8.1"),sQuery(id+"F0.wireOp",EDGE,"E11.8.2"),sQuery(id+"F0.wireOp",EDGE,"E11.8.3"),sQuery(id+"F0.wireOp",EDGE,"E11.8.4"),sQuery(id+"F0.wireOp",EDGE,"E11.8.5"),sQuery(id+"F0.wireOp",EDGE,"E11.8.6"),sQuery(id+"F0.wireOp",EDGE,"E11.9.0"),sQuery(id+"F0.wireOp",EDGE,"E11.9.1"),sQuery(id+"F0.wireOp",EDGE,"E11.9.2"),sQuery(id+"F0.wireOp",EDGE,"E11.9.3"),sQuery(id+"F0.wireOp",EDGE,"E11.9.4"),sQuery(id+"F0.wireOp",EDGE,"E11.9.5"),sQuery(id+"F0.wireOp",EDGE,"E11.9.6"),sQuery(id+"F0.wireOp",EDGE,"E11.10.0"),sQuery(id+"F0.wireOp",EDGE,"E11.10.1"),sQuery(id+"F0.wireOp",EDGE,"E11.10.2"),sQuery(id+"F0.wireOp",EDGE,"E11.10.3"),sQuery(id+"F0.wireOp",EDGE,"E11.10.4"),sQuery(id+"F0.wireOp",EDGE,"E11.10.5"),sQuery(id+"F0.wireOp",EDGE,"E11.10.6"),sQuery(id+"F0.wireOp",EDGE,"E11.11.0"),sQuery(id+"F0.wireOp",EDGE,"E11.11.1"),sQuery(id+"F0.wireOp",EDGE,"E11.11.2"),sQuery(id+"F0.wireOp",EDGE,"E11.11.3"),sQuery(id+"F0.wireOp",EDGE,"E11.11.4"),sQuery(id+"F0.wireOp",EDGE,"E11.11.5"),sQuery(id+"F0.wireOp",EDGE,"E11.11.6"),sQuery(id+"F0.wireOp",EDGE,"E11.12.0"),sQuery(id+"F0.wireOp",EDGE,"E11.12.1"),sQuery(id+"F0.wireOp",EDGE,"E11.12.2"),sQuery(id+"F0.wireOp",EDGE,"E11.12.3"),sQuery(id+"F0.wireOp",EDGE,"E11.12.4"),sQuery(id+"F0.wireOp",EDGE,"E11.12.5"),sQuery(id+"F0.wireOp",EDGE,"E11.12.6"),sQuery(id+"F0.wireOp",EDGE,"E11.13.0"),sQuery(id+"F0.wireOp",EDGE,"E11.13.1"),sQuery(id+"F0.wireOp",EDGE,"E11.13.2"),sQuery(id+"F0.wireOp",EDGE,"E11.13.3"),sQuery(id+"F0.wireOp",EDGE,"E11.13.4"),sQuery(id+"F0.wireOp",EDGE,"E11.13.5"),sQuery(id+"F0.wireOp",EDGE,"E11.13.6"),sQuery(id+"F0.wireOp",EDGE,"E11.14.0"),sQuery(id+"F0.wireOp",EDGE,"E11.14.1"),sQuery(id+"F0.wireOp",EDGE,"E11.14.2"),sQuery(id+"F0.wireOp",EDGE,"E11.14.3"),sQuery(id+"F0.wireOp",EDGE,"E11.14.4"),sQuery(id+"F0.wireOp",EDGE,"E11.14.5"),sQuery(id+"F0.wireOp",EDGE,"E11.14.6"),sQuery(id+"F0.wireOp",EDGE,"E11.15.0"),sQuery(id+"F0.wireOp",EDGE,"E11.15.1"),sQuery(id+"F0.wireOp",EDGE,"E11.15.2"),sQuery(id+"F0.wireOp",EDGE,"E11.15.3"),sQuery(id+"F0.wireOp",EDGE,"E11.15.4"),sQuery(id+"F0.wireOp",EDGE,"E11.15.5"),sQuery(id+"F0.wireOp",EDGE,"E11.15.6"),sQuery(id+"F0.wireOp",EDGE,"E11.16.0"),sQuery(id+"F0.wireOp",EDGE,"E11.16.1"),sQuery(id+"F0.wireOp",EDGE,"E11.16.2"),sQuery(id+"F0.wireOp",EDGE,"E11.16.3"),sQuery(id+"F0.wireOp",EDGE,"E11.16.4"),sQuery(id+"F0.wireOp",EDGE,"E11.16.5"),sQuery(id+"F0.wireOp",EDGE,"E11.16.6"),sQuery(id+"F0.wireOp",EDGE,"E11.17.0"),sQuery(id+"F0.wireOp",EDGE,"E11.17.1"),sQuery(id+"F0.wireOp",EDGE,"E11.17.2"),sQuery(id+"F0.wireOp",EDGE,"E11.17.3"),sQuery(id+"F0.wireOp",EDGE,"E11.17.4"),sQuery(id+"F0.wireOp",EDGE,"E11.17.5"),sQuery(id+"F0.wireOp",EDGE,"E11.17.6"),sQuery(id+"F0.wireOp",EDGE,"E11.18.0"),sQuery(id+"F0.wireOp",EDGE,"E11.18.1"),sQuery(id+"F0.wireOp",EDGE,"E11.18.2"),sQuery(id+"F0.wireOp",EDGE,"E11.18.3"),sQuery(id+"F0.wireOp",EDGE,"E11.18.4"),sQuery(id+"F0.wireOp",EDGE,"E11.18.5"),sQuery(id+"F0.wireOp",EDGE,"E11.18.6"),sQuery(id+"F0.wireOp",EDGE,"E11.19.0"),sQuery(id+"F0.wireOp",EDGE,"E11.19.1"),sQuery(id+"F0.wireOp",EDGE,"E11.19.2"),sQuery(id+"F0.wireOp",EDGE,"E11.19.3"),sQuery(id+"F0.wireOp",EDGE,"E11.19.4"),sQuery(id+"F0.wireOp",EDGE,"E11.19.5"),sQuery(id+"F0.wireOp",EDGE,"E11.19.6"),sQuery(id+"F0.wireOp",EDGE,"E11.20.0"),sQuery(id+"F0.wireOp",EDGE,"E11.20.1"),sQuery(id+"F0.wireOp",EDGE,"E11.20.2"),sQuery(id+"F0.wireOp",EDGE,"E11.20.3"),sQuery(id+"F0.wireOp",EDGE,"E11.20.4"),sQuery(id+"F0.wireOp",EDGE,"E11.20.5"),sQuery(id+"F0.wireOp",EDGE,"E11.20.6"),sQuery(id+"F0.wireOp",EDGE,"E11.21.0"),sQuery(id+"F0.wireOp",EDGE,"E11.21.1"),sQuery(id+"F0.wireOp",EDGE,"E11.21.2"),sQuery(id+"F0.wireOp",EDGE,"E11.21.3"),sQuery(id+"F0.wireOp",EDGE,"E11.21.4"),sQuery(id+"F0.wireOp",EDGE,"E11.21.5"),sQuery(id+"F0.wireOp",EDGE,"E11.21.6"),sQuery(id+"F0.wireOp",EDGE,"E11.22.0"),sQuery(id+"F0.wireOp",EDGE,"E11.22.1"),sQuery(id+"F0.wireOp",EDGE,"E11.22.2"),sQuery(id+"F0.wireOp",EDGE,"E11.22.3"),sQuery(id+"F0.wireOp",EDGE,"E11.22.4"),sQuery(id+"F0.wireOp",EDGE,"E11.22.5"),sQuery(id+"F0.wireOp",EDGE,"E11.22.6"),sQuery(id+"F0.wireOp",EDGE,"E11.23.0"),sQuery(id+"F0.wireOp",EDGE,"E11.23.1"),sQuery(id+"F0.wireOp",EDGE,"E11.23.2"),sQuery(id+"F0.wireOp",EDGE,"E11.23.3"),sQuery(id+"F0.wireOp",EDGE,"E11.23.4"),sQuery(id+"F0.wireOp",EDGE,"E11.23.5"),sQuery(id+"F0.wireOp",EDGE,"E11.23.6"),sQuery(id+"F0.wireOp",EDGE,"E11.24.0"),sQuery(id+"F0.wireOp",EDGE,"E11.24.1"),sQuery(id+"F0.wireOp",EDGE,"E11.24.2"),sQuery(id+"F0.wireOp",EDGE,"E11.24.3"),sQuery(id+"F0.wireOp",EDGE,"E11.24.4"),sQuery(id+"F0.wireOp",EDGE,"E11.24.5"),sQuery(id+"F0.wireOp",EDGE,"E11.24.6"),sQuery(id+"F0.wireOp",EDGE,"E11.25.0"),sQuery(id+"F0.wireOp",EDGE,"E11.25.1"),sQuery(id+"F0.wireOp",EDGE,"E11.25.2"),sQuery(id+"F0.wireOp",EDGE,"E11.25.3"),sQuery(id+"F0.wireOp",EDGE,"E11.25.4"),sQuery(id+"F0.wireOp",EDGE,"E11.25.5"),sQuery(id+"F0.wireOp",EDGE,"E11.25.6"),sQuery(id+"F0.wireOp",EDGE,"E11.26.0"),sQuery(id+"F0.wireOp",EDGE,"E11.26.1"),sQuery(id+"F0.wireOp",EDGE,"E11.26.2"),sQuery(id+"F0.wireOp",EDGE,"E11.26.3"),sQuery(id+"F0.wireOp",EDGE,"E11.26.4"),sQuery(id+"F0.wireOp",EDGE,"E11.26.5"),sQuery(id+"F0.wireOp",EDGE,"E11.26.6"),sQuery(id+"F0.wireOp",EDGE,"E11.27.0"),sQuery(id+"F0.wireOp",EDGE,"E11.27.1"),sQuery(id+"F0.wireOp",EDGE,"E11.27.2"),sQuery(id+"F0.wireOp",EDGE,"E11.27.3"),sQuery(id+"F0.wireOp",EDGE,"E11.27.4"),sQuery(id+"F0.wireOp",EDGE,"E11.27.5"),sQuery(id+"F0.wireOp",EDGE,"E11.27.6"),sQuery(id+"F0.wireOp",EDGE,"E11.28.0"),sQuery(id+"F0.wireOp",EDGE,"E11.28.1"),sQuery(id+"F0.wireOp",EDGE,"E11.28.2"),sQuery(id+"F0.wireOp",EDGE,"E11.28.3"),sQuery(id+"F0.wireOp",EDGE,"E11.28.4"),sQuery(id+"F0.wireOp",EDGE,"E11.28.5"),sQuery(id+"F0.wireOp",EDGE,"E11.28.6"),sQuery(id+"F0.wireOp",EDGE,"E11.29.0"),sQuery(id+"F0.wireOp",EDGE,"E11.29.1"),sQuery(id+"F0.wireOp",EDGE,"E11.29.2"),sQuery(id+"F0.wireOp",EDGE,"E11.29.3"),sQuery(id+"F0.wireOp",EDGE,"E11.29.4"),sQuery(id+"F0.wireOp",EDGE,"E11.29.5"),sQuery(id+"F0.wireOp",EDGE,"E11.29.6"),sQuery(id+"F0.wireOp",EDGE,"E11.30.0"),sQuery(id+"F0.wireOp",EDGE,"E11.30.1"),sQuery(id+"F0.wireOp",EDGE,"E11.30.2"),sQuery(id+"F0.wireOp",EDGE,"E11.30.3"),sQuery(id+"F0.wireOp",EDGE,"E11.30.4"),sQuery(id+"F0.wireOp",EDGE,"E11.30.5"),sQuery(id+"F0.wireOp",EDGE,"E11.30.6"),sQuery(id+"F0.wireOp",EDGE,"E11.31.0"),sQuery(id+"F0.wireOp",EDGE,"E11.31.1"),sQuery(id+"F0.wireOp",EDGE,"E11.31.2"),sQuery(id+"F0.wireOp",EDGE,"E11.31.3"),sQuery(id+"F0.wireOp",EDGE,"E11.31.4"),sQuery(id+"F0.wireOp",EDGE,"E11.31.5"),sQuery(id+"F0.wireOp",EDGE,"E11.31.6"),sQuery(id+"F0.wireOp",EDGE,"E11.32.0"),sQuery(id+"F0.wireOp",EDGE,"E11.32.1"),sQuery(id+"F0.wireOp",EDGE,"E11.32.2"),sQuery(id+"F0.wireOp",EDGE,"E11.32.3"),sQuery(id+"F0.wireOp",EDGE,"E11.32.4"),sQuery(id+"F0.wireOp",EDGE,"E11.32.5"),sQuery(id+"F0.wireOp",EDGE,"E11.32.6"),sQuery(id+"F0.wireOp",EDGE,"E11.33.0"),sQuery(id+"F0.wireOp",EDGE,"E11.33.1"),sQuery(id+"F0.wireOp",EDGE,"E11.33.2"),sQuery(id+"F0.wireOp",EDGE,"E11.33.3"),sQuery(id+"F0.wireOp",EDGE,"E11.33.4"),sQuery(id+"F0.wireOp",EDGE,"E11.33.5"),sQuery(id+"F0.wireOp",EDGE,"E11.33.6"),sQuery(id+"F0.wireOp",EDGE,"E11.34.0"),sQuery(id+"F0.wireOp",EDGE,"E11.34.1"),sQuery(id+"F0.wireOp",EDGE,"E11.34.2"),sQuery(id+"F0.wireOp",EDGE,"E11.34.3"),sQuery(id+"F0.wireOp",EDGE,"E11.34.4"),sQuery(id+"F0.wireOp",EDGE,"E11.34.5"),sQuery(id+"F0.wireOp",EDGE,"E11.34.6"),sQuery(id+"F0.wireOp",EDGE,"E11.35.0"),sQuery(id+"F0.wireOp",EDGE,"E11.35.1"),sQuery(id+"F0.wireOp",EDGE,"E11.35.2"),sQuery(id+"F0.wireOp",EDGE,"E11.35.3"),sQuery(id+"F0.wireOp",EDGE,"E11.35.4"),sQuery(id+"F0.wireOp",EDGE,"E11.35.5"),sQuery(id+"F0.wireOp",EDGE,"E11.35.6"),sQuery(id+"F0.wireOp",EDGE,"E11.36.0"),sQuery(id+"F0.wireOp",EDGE,"E11.36.1"),sQuery(id+"F0.wireOp",EDGE,"E11.36.2"),sQuery(id+"F0.wireOp",EDGE,"E11.36.3"),sQuery(id+"F0.wireOp",EDGE,"E11.36.4"),sQuery(id+"F0.wireOp",EDGE,"E11.36.5"),sQuery(id+"F0.wireOp",EDGE,"E11.36.6"),sQuery(id+"F0.wireOp",EDGE,"E11.37.0"),sQuery(id+"F0.wireOp",EDGE,"E11.37.1"),sQuery(id+"F0.wireOp",EDGE,"E11.37.2"),sQuery(id+"F0.wireOp",EDGE,"E11.37.3"),sQuery(id+"F0.wireOp",EDGE,"E11.37.4"),sQuery(id+"F0.wireOp",EDGE,"E11.37.5"),sQuery(id+"F0.wireOp",EDGE,"E11.37.6"),sQuery(id+"F0.wireOp",EDGE,"E11.38.0"),sQuery(id+"F0.wireOp",EDGE,"E11.38.1"),sQuery(id+"F0.wireOp",EDGE,"E11.38.2"),sQuery(id+"F0.wireOp",EDGE,"E11.38.3"),sQuery(id+"F0.wireOp",EDGE,"E11.38.4"),sQuery(id+"F0.wireOp",EDGE,"E11.38.5"),sQuery(id+"F0.wireOp",EDGE,"E11.38.6"),sQuery(id+"F0.wireOp",EDGE,"E11.39.0"),sQuery(id+"F0.wireOp",EDGE,"E11.39.1"),sQuery(id+"F0.wireOp",EDGE,"E11.39.2"),sQuery(id+"F0.wireOp",EDGE,"E11.39.3"),sQuery(id+"F0.wireOp",EDGE,"E11.39.4"),sQuery(id+"F0.wireOp",EDGE,"E11.39.5"),sQuery(id+"F0.wireOp",EDGE,"E11.39.6"),sQuery(id+"F0.wireOp",EDGE,"E11.40.0"),sQuery(id+"F0.wireOp",EDGE,"E11.40.1"),sQuery(id+"F0.wireOp",EDGE,"E11.40.2"),sQuery(id+"F0.wireOp",EDGE,"E11.40.3"),sQuery(id+"F0.wireOp",EDGE,"E11.40.4"),sQuery(id+"F0.wireOp",EDGE,"E11.40.5"),sQuery(id+"F0.wireOp",EDGE,"E11.40.6"),sQuery(id+"F0.wireOp",EDGE,"E11.41.0"),sQuery(id+"F0.wireOp",EDGE,"E11.41.1"),sQuery(id+"F0.wireOp",EDGE,"E11.41.2"),sQuery(id+"F0.wireOp",EDGE,"E11.41.3"),sQuery(id+"F0.wireOp",EDGE,"E11.41.4"),sQuery(id+"F0.wireOp",EDGE,"E11.41.5"),sQuery(id+"F0.wireOp",EDGE,"E11.41.6"),sQuery(id+"F0.wireOp",EDGE,"E11.42.0"),sQuery(id+"F0.wireOp",EDGE,"E11.42.1"),sQuery(id+"F0.wireOp",EDGE,"E11.42.2"),sQuery(id+"F0.wireOp",EDGE,"E11.42.3"),sQuery(id+"F0.wireOp",EDGE,"E11.42.4"),sQuery(id+"F0.wireOp",EDGE,"E11.42.5"),sQuery(id+"F0.wireOp",EDGE,"E11.42.6"),sQuery(id+"F0.wireOp",EDGE,"E11.43.0"),sQuery(id+"F0.wireOp",EDGE,"E11.43.1"),sQuery(id+"F0.wireOp",EDGE,"E11.43.2"),sQuery(id+"F0.wireOp",EDGE,"E11.43.3"),sQuery(id+"F0.wireOp",EDGE,"E11.43.4"),sQuery(id+"F0.wireOp",EDGE,"E11.43.5"),sQuery(id+"F0.wireOp",EDGE,"E11.43.6"),sQuery(id+"F0.wireOp",EDGE,"E11.44.0"),sQuery(id+"F0.wireOp",EDGE,"E11.44.1"),sQuery(id+"F0.wireOp",EDGE,"E11.44.2"),sQuery(id+"F0.wireOp",EDGE,"E11.44.3"),sQuery(id+"F0.wireOp",EDGE,"E11.44.4"),sQuery(id+"F0.wireOp",EDGE,"E11.44.5"),sQuery(id+"F0.wireOp",EDGE,"E11.44.6"),sQuery(id+"F0.wireOp",EDGE,"E11.45.0"),sQuery(id+"F0.wireOp",EDGE,"E11.45.1"),sQuery(id+"F0.wireOp",EDGE,"E11.45.2"),sQuery(id+"F0.wireOp",EDGE,"E11.45.3"),sQuery(id+"F0.wireOp",EDGE,"E11.45.4"),sQuery(id+"F0.wireOp",EDGE,"E11.45.5"),sQuery(id+"F0.wireOp",EDGE,"E11.45.6"),sQuery(id+"F0.wireOp",EDGE,"E11.46.0"),sQuery(id+"F0.wireOp",EDGE,"E11.46.1"),sQuery(id+"F0.wireOp",EDGE,"E11.46.2"),sQuery(id+"F0.wireOp",EDGE,"E11.46.3"),sQuery(id+"F0.wireOp",EDGE,"E11.46.4"),sQuery(id+"F0.wireOp",EDGE,"E11.46.5"),sQuery(id+"F0.wireOp",EDGE,"E11.46.6"),sQuery(id+"F0.wireOp",EDGE,"E11.47.0"),sQuery(id+"F0.wireOp",EDGE,"E11.47.1"),sQuery(id+"F0.wireOp",EDGE,"E11.47.2"),sQuery(id+"F0.wireOp",EDGE,"E11.47.3"),sQuery(id+"F0.wireOp",EDGE,"E11.47.4"),sQuery(id+"F0.wireOp",EDGE,"E11.47.5"),sQuery(id+"F0.wireOp",EDGE,"E11.47.6"),sQuery(id+"F0.wireOp",EDGE,"E11.48.0"),sQuery(id+"F0.wireOp",EDGE,"E11.48.1"),sQuery(id+"F0.wireOp",EDGE,"E11.48.2"),sQuery(id+"F0.wireOp",EDGE,"E11.48.3"),sQuery(id+"F0.wireOp",EDGE,"E11.48.4"),sQuery(id+"F0.wireOp",EDGE,"E11.48.5"),sQuery(id+"F0.wireOp",EDGE,"E11.48.6"),sQuery(id+"F0.wireOp",EDGE,"E11.49.0"),sQuery(id+"F0.wireOp",EDGE,"E11.49.1"),sQuery(id+"F0.wireOp",EDGE,"E11.49.2"),sQuery(id+"F0.wireOp",EDGE,"E11.49.3"),sQuery(id+"F0.wireOp",EDGE,"E11.49.4"),sQuery(id+"F0.wireOp",EDGE,"E11.49.5"),sQuery(id+"F0.wireOp",EDGE,"E11.49.6"),sQuery(id+"F0.wireOp",EDGE,"E11.50.0"),sQuery(id+"F0.wireOp",EDGE,"E11.50.1"),sQuery(id+"F0.wireOp",EDGE,"E11.50.2"),sQuery(id+"F0.wireOp",EDGE,"E11.50.3"),sQuery(id+"F0.wireOp",EDGE,"E11.50.4"),sQuery(id+"F0.wireOp",EDGE,"E11.50.5"),sQuery(id+"F0.wireOp",EDGE,"E11.50.6"),sQuery(id+"F0.wireOp",EDGE,"E11.51.0"),sQuery(id+"F0.wireOp",EDGE,"E11.51.1"),sQuery(id+"F0.wireOp",EDGE,"E11.51.2"),sQuery(id+"F0.wireOp",EDGE,"E11.51.3"),sQuery(id+"F0.wireOp",EDGE,"E11.51.4"),sQuery(id+"F0.wireOp",EDGE,"E11.51.5"),sQuery(id+"F0.wireOp",EDGE,"E11.51.6"),sQuery(id+"F0.wireOp",EDGE,"E11.52.0"),sQuery(id+"F0.wireOp",EDGE,"E11.52.1"),sQuery(id+"F0.wireOp",EDGE,"E11.52.2"),sQuery(id+"F0.wireOp",EDGE,"E11.52.3"),sQuery(id+"F0.wireOp",EDGE,"E11.52.4"),sQuery(id+"F0.wireOp",EDGE,"E11.52.5"),sQuery(id+"F0.wireOp",EDGE,"E11.52.6"),sQuery(id+"F0.wireOp",EDGE,"E11.53.0"),sQuery(id+"F0.wireOp",EDGE,"E11.53.1"),sQuery(id+"F0.wireOp",EDGE,"E11.53.2"),sQuery(id+"F0.wireOp",EDGE,"E11.53.3"),sQuery(id+"F0.wireOp",EDGE,"E11.53.4"),sQuery(id+"F0.wireOp",EDGE,"E11.53.5"),sQuery(id+"F0.wireOp",EDGE,"E11.53.6"),sQuery(id+"F0.wireOp",EDGE,"E11.54.0"),sQuery(id+"F0.wireOp",EDGE,"E11.54.1"),sQuery(id+"F0.wireOp",EDGE,"E11.54.2"),sQuery(id+"F0.wireOp",EDGE,"E11.54.3"),sQuery(id+"F0.wireOp",EDGE,"E11.54.4"),sQuery(id+"F0.wireOp",EDGE,"E11.54.5"),sQuery(id+"F0.wireOp",EDGE,"E11.54.6"),sQuery(id+"F0.wireOp",EDGE,"E11.55.0"),sQuery(id+"F0.wireOp",EDGE,"E11.55.1"),sQuery(id+"F0.wireOp",EDGE,"E11.55.2"),sQuery(id+"F0.wireOp",EDGE,"E11.55.3"),sQuery(id+"F0.wireOp",EDGE,"E11.55.4"),sQuery(id+"F0.wireOp",EDGE,"E11.55.5"),sQuery(id+"F0.wireOp",EDGE,"E11.55.6"),sQuery(id+"F0.wireOp",EDGE,"E11.56.0"),sQuery(id+"F0.wireOp",EDGE,"E11.56.1"),sQuery(id+"F0.wireOp",EDGE,"E11.56.2"),sQuery(id+"F0.wireOp",EDGE,"E11.56.3"),sQuery(id+"F0.wireOp",EDGE,"E11.56.4"),sQuery(id+"F0.wireOp",EDGE,"E11.56.5"),sQuery(id+"F0.wireOp",EDGE,"E11.56.6"),sQuery(id+"F0.wireOp",EDGE,"E11.57.0"),sQuery(id+"F0.wireOp",EDGE,"E11.57.1"),sQuery(id+"F0.wireOp",EDGE,"E11.57.2"),sQuery(id+"F0.wireOp",EDGE,"E11.57.3"),sQuery(id+"F0.wireOp",EDGE,"E11.57.4"),sQuery(id+"F0.wireOp",EDGE,"E11.57.5"),sQuery(id+"F0.wireOp",EDGE,"E11.57.6"),sQuery(id+"F0.wireOp",EDGE,"E11.58.0"),sQuery(id+"F0.wireOp",EDGE,"E11.58.1"),sQuery(id+"F0.wireOp",EDGE,"E11.58.2"),sQuery(id+"F0.wireOp",EDGE,"E11.58.3"),sQuery(id+"F0.wireOp",EDGE,"E11.58.4"),sQuery(id+"F0.wireOp",EDGE,"E11.58.5"),sQuery(id+"F0.wireOp",EDGE,"E11.58.6"),sQuery(id+"F0.wireOp",EDGE,"E11.59.0"),sQuery(id+"F0.wireOp",EDGE,"E11.59.1"),sQuery(id+"F0.wireOp",EDGE,"E11.59.2"),sQuery(id+"F0.wireOp",EDGE,"E11.59.3"),sQuery(id+"F0.wireOp",EDGE,"E11.59.4"),sQuery(id+"F0.wireOp",EDGE,"E11.59.5"),sQuery(id+"F0.wireOp",EDGE,"E11.59.6"),sQuery(id+"F0.wireOp",EDGE,"E11.60.0"),sQuery(id+"F0.wireOp",EDGE,"E11.60.1"),sQuery(id+"F0.wireOp",EDGE,"E11.60.2"),sQuery(id+"F0.wireOp",EDGE,"E11.60.3"),sQuery(id+"F0.wireOp",EDGE,"E11.60.4"),sQuery(id+"F0.wireOp",EDGE,"E11.60.5"),sQuery(id+"F0.wireOp",EDGE,"E11.60.6"),sQuery(id+"F0.wireOp",EDGE,"E11.61.0"),sQuery(id+"F0.wireOp",EDGE,"E11.61.1"),sQuery(id+"F0.wireOp",EDGE,"E11.61.2"),sQuery(id+"F0.wireOp",EDGE,"E11.61.3"),sQuery(id+"F0.wireOp",EDGE,"E11.61.4"),sQuery(id+"F0.wireOp",EDGE,"E11.61.5"),sQuery(id+"F0.wireOp",EDGE,"E11.61.6"),sQuery(id+"F0.wireOp",EDGE,"E11.62.0"),sQuery(id+"F0.wireOp",EDGE,"E11.62.1"),sQuery(id+"F0.wireOp",EDGE,"E11.62.2"),sQuery(id+"F0.wireOp",EDGE,"E11.62.3"),sQuery(id+"F0.wireOp",EDGE,"E11.62.4"),sQuery(id+"F0.wireOp",EDGE,"E11.62.5"),sQuery(id+"F0.wireOp",EDGE,"E11.62.6"),sQuery(id+"F0.wireOp",EDGE,"E11.63.0"),sQuery(id+"F0.wireOp",EDGE,"E11.63.1"),sQuery(id+"F0.wireOp",EDGE,"E11.63.2"),sQuery(id+"F0.wireOp",EDGE,"E11.63.3"),sQuery(id+"F0.wireOp",EDGE,"E11.63.4"),sQuery(id+"F0.wireOp",EDGE,"E11.63.5"),sQuery(id+"F0.wireOp",EDGE,"E11.63.6"),sQuery(id+"F0.wireOp",EDGE,"E11.64.0"),sQuery(id+"F0.wireOp",EDGE,"E11.64.1"),sQuery(id+"F0.wireOp",EDGE,"E11.64.2"),sQuery(id+"F0.wireOp",EDGE,"E11.64.3"),sQuery(id+"F0.wireOp",EDGE,"E11.64.4"),sQuery(id+"F0.wireOp",EDGE,"E11.64.5"),sQuery(id+"F0.wireOp",EDGE,"E11.64.6"),sQuery(id+"F0.wireOp",EDGE,"E11.65.0"),sQuery(id+"F0.wireOp",EDGE,"E11.65.1"),sQuery(id+"F0.wireOp",EDGE,"E11.65.2"),sQuery(id+"F0.wireOp",EDGE,"E11.65.3"),sQuery(id+"F0.wireOp",EDGE,"E11.65.4"),sQuery(id+"F0.wireOp",EDGE,"E11.65.5"),sQuery(id+"F0.wireOp",EDGE,"E11.65.6"),sQuery(id+"F0.wireOp",EDGE,"E11.66.0"),sQuery(id+"F0.wireOp",EDGE,"E11.66.1"),sQuery(id+"F0.wireOp",EDGE,"E11.66.2"),sQuery(id+"F0.wireOp",EDGE,"E11.66.3"),sQuery(id+"F0.wireOp",EDGE,"E11.66.4"),sQuery(id+"F0.wireOp",EDGE,"E11.66.5"),sQuery(id+"F0.wireOp",EDGE,"E11.66.6"),sQuery(id+"F0.wireOp",EDGE,"E11.67.0"),sQuery(id+"F0.wireOp",EDGE,"E11.67.1"),sQuery(id+"F0.wireOp",EDGE,"E11.67.2"),sQuery(id+"F0.wireOp",EDGE,"E11.67.3"),sQuery(id+"F0.wireOp",EDGE,"E11.67.4"),sQuery(id+"F0.wireOp",EDGE,"E11.67.5"),sQuery(id+"F0.wireOp",EDGE,"E11.67.6"),sQuery(id+"F0.wireOp",EDGE,"E11.68.0"),sQuery(id+"F0.wireOp",EDGE,"E11.68.1"),sQuery(id+"F0.wireOp",EDGE,"E11.68.2"),sQuery(id+"F0.wireOp",EDGE,"E11.68.3"),sQuery(id+"F0.wireOp",EDGE,"E11.68.4"),sQuery(id+"F0.wireOp",EDGE,"E11.68.5"),sQuery(id+"F0.wireOp",EDGE,"E11.68.6"),sQuery(id+"F0.wireOp",EDGE,"E11.69.0"),sQuery(id+"F0.wireOp",EDGE,"E11.69.1"),sQuery(id+"F0.wireOp",EDGE,"E11.69.2"),sQuery(id+"F0.wireOp",EDGE,"E11.69.3"),sQuery(id+"F0.wireOp",EDGE,"E11.69.4"),sQuery(id+"F0.wireOp",EDGE,"E11.69.5"),sQuery(id+"F0.wireOp",EDGE,"E11.69.6"),sQuery(id+"F0.wireOp",EDGE,"E11.70.0"),sQuery(id+"F0.wireOp",EDGE,"E11.70.1"),sQuery(id+"F0.wireOp",EDGE,"E11.70.2"),sQuery(id+"F0.wireOp",EDGE,"E11.70.3"),sQuery(id+"F0.wireOp",EDGE,"E11.70.4"),sQuery(id+"F0.wireOp",EDGE,"E11.70.5"),sQuery(id+"F0.wireOp",EDGE,"E11.70.6"),sQuery(id+"F0.wireOp",EDGE,"E11.71.0"),sQuery(id+"F0.wireOp",EDGE,"E11.71.1"),sQuery(id+"F0.wireOp",EDGE,"E11.71.2"),sQuery(id+"F0.wireOp",EDGE,"E11.71.3"),sQuery(id+"F0.wireOp",EDGE,"E11.71.4"),sQuery(id+"F0.wireOp",EDGE,"E11.71.5"),sQuery(id+"F0.wireOp",EDGE,"E11.71.6"),sQuery(id+"F0.wireOp",EDGE,"E11.72.0"),sQuery(id+"F0.wireOp",EDGE,"E11.72.1"),sQuery(id+"F0.wireOp",EDGE,"E11.72.2"),sQuery(id+"F0.wireOp",EDGE,"E11.72.3"),sQuery(id+"F0.wireOp",EDGE,"E11.72.4"),sQuery(id+"F0.wireOp",EDGE,"E11.72.5"),sQuery(id+"F0.wireOp",EDGE,"E11.72.6"),sQuery(id+"F0.wireOp",EDGE,"E11.73.0"),sQuery(id+"F0.wireOp",EDGE,"E11.73.1"),sQuery(id+"F0.wireOp",EDGE,"E11.73.2"),sQuery(id+"F0.wireOp",EDGE,"E11.73.3"),sQuery(id+"F0.wireOp",EDGE,"E11.73.4"),sQuery(id+"F0.wireOp",EDGE,"E11.73.5"),sQuery(id+"F0.wireOp",EDGE,"E11.73.6"),sQuery(id+"F0.wireOp",EDGE,"E11.74.0"),sQuery(id+"F0.wireOp",EDGE,"E11.74.1"),sQuery(id+"F0.wireOp",EDGE,"E11.74.2"),sQuery(id+"F0.wireOp",EDGE,"E11.74.3"),sQuery(id+"F0.wireOp",EDGE,"E11.74.4"),sQuery(id+"F0.wireOp",EDGE,"E11.74.5"),sQuery(id+"F0.wireOp",EDGE,"E11.74.6"),sQuery(id+"F0.wireOp",EDGE,"E11.75.0"),sQuery(id+"F0.wireOp",EDGE,"E11.75.1"),sQuery(id+"F0.wireOp",EDGE,"E11.75.2"),sQuery(id+"F0.wireOp",EDGE,"E11.75.3"),sQuery(id+"F0.wireOp",EDGE,"E11.75.4"),sQuery(id+"F0.wireOp",EDGE,"E11.75.5"),sQuery(id+"F0.wireOp",EDGE,"E11.75.6"),sQuery(id+"F0.wireOp",EDGE,"E11.76.0"),sQuery(id+"F0.wireOp",EDGE,"E11.76.1"),sQuery(id+"F0.wireOp",EDGE,"E11.76.2"),sQuery(id+"F0.wireOp",EDGE,"E11.76.3"),sQuery(id+"F0.wireOp",EDGE,"E11.76.4"),sQuery(id+"F0.wireOp",EDGE,"E11.76.5"),sQuery(id+"F0.wireOp",EDGE,"E11.76.6"),sQuery(id+"F0.wireOp",EDGE,"E11.77.0"),sQuery(id+"F0.wireOp",EDGE,"E11.77.1"),sQuery(id+"F0.wireOp",EDGE,"E11.77.2"),sQuery(id+"F0.wireOp",EDGE,"E11.77.3"),sQuery(id+"F0.wireOp",EDGE,"E11.77.4"),sQuery(id+"F0.wireOp",EDGE,"E11.77.5"),sQuery(id+"F0.wireOp",EDGE,"E11.77.6"),sQuery(id+"F0.wireOp",EDGE,"E11.78.0"),sQuery(id+"F0.wireOp",EDGE,"E11.78.1"),sQuery(id+"F0.wireOp",EDGE,"E11.78.2"),sQuery(id+"F0.wireOp",EDGE,"E11.78.3"),sQuery(id+"F0.wireOp",EDGE,"E11.78.4"),sQuery(id+"F0.wireOp",EDGE,"E11.78.5"),sQuery(id+"F0.wireOp",EDGE,"E11.78.6"),sQuery(id+"F0.wireOp",EDGE,"E11.79.0"),sQuery(id+"F0.wireOp",EDGE,"E11.79.1"),sQuery(id+"F0.wireOp",EDGE,"E11.79.2"),sQuery(id+"F0.wireOp",EDGE,"E11.79.3"),sQuery(id+"F0.wireOp",EDGE,"E11.79.4"),sQuery(id+"F0.wireOp",EDGE,"E11.79.5"),sQuery(id+"F0.wireOp",EDGE,"E11.79.6"),sQuery(id+"F0.wireOp",EDGE,"E11.80.0"),sQuery(id+"F0.wireOp",EDGE,"E11.80.1"),sQuery(id+"F0.wireOp",EDGE,"E11.80.2"),sQuery(id+"F0.wireOp",EDGE,"E11.80.3"),sQuery(id+"F0.wireOp",EDGE,"E11.80.4"),sQuery(id+"F0.wireOp",EDGE,"E11.80.5"),sQuery(id+"F0.wireOp",EDGE,"E11.80.6"),sQuery(id+"F0.wireOp",EDGE,"E11.81.0"),sQuery(id+"F0.wireOp",EDGE,"E11.81.1"),sQuery(id+"F0.wireOp",EDGE,"E11.81.2"),sQuery(id+"F0.wireOp",EDGE,"E11.81.3"),sQuery(id+"F0.wireOp",EDGE,"E11.81.4"),sQuery(id+"F0.wireOp",EDGE,"E11.81.5"),sQuery(id+"F0.wireOp",EDGE,"E11.81.6"),sQuery(id+"F0.wireOp",EDGE,"E11.82.0"),sQuery(id+"F0.wireOp",EDGE,"E11.82.1"),sQuery(id+"F0.wireOp",EDGE,"E11.82.2"),sQuery(id+"F0.wireOp",EDGE,"E11.82.3"),sQuery(id+"F0.wireOp",EDGE,"E11.82.4"),sQuery(id+"F0.wireOp",EDGE,"E11.82.5"),sQuery(id+"F0.wireOp",EDGE,"E11.82.6"),sQuery(id+"F0.wireOp",EDGE,"E11.83.0"),sQuery(id+"F0.wireOp",EDGE,"E11.83.1"),sQuery(id+"F0.wireOp",EDGE,"E11.83.2"),sQuery(id+"F0.wireOp",EDGE,"E11.83.3"),sQuery(id+"F0.wireOp",EDGE,"E11.83.4"),sQuery(id+"F0.wireOp",EDGE,"E11.83.5"),sQuery(id+"F0.wireOp",EDGE,"E11.83.6"),sQuery(id+"F0.wireOp",EDGE,"E11.84.0"),sQuery(id+"F0.wireOp",EDGE,"E11.84.1"),sQuery(id+"F0.wireOp",EDGE,"E11.84.2"),sQuery(id+"F0.wireOp",EDGE,"E11.84.3"),sQuery(id+"F0.wireOp",EDGE,"E11.84.4"),sQuery(id+"F0.wireOp",EDGE,"E11.84.5"),sQuery(id+"F0.wireOp",EDGE,"E11.84.6"),sQuery(id+"F0.wireOp",EDGE,"E11.85.0"),sQuery(id+"F0.wireOp",EDGE,"E11.85.1"),sQuery(id+"F0.wireOp",EDGE,"E11.85.2"),sQuery(id+"F0.wireOp",EDGE,"E11.85.3"),sQuery(id+"F0.wireOp",EDGE,"E11.85.4"),sQuery(id+"F0.wireOp",EDGE,"E11.85.5"),sQuery(id+"F0.wireOp",EDGE,"E11.85.6"),sQuery(id+"F0.wireOp",EDGE,"E11.86.0"),sQuery(id+"F0.wireOp",EDGE,"E11.86.1"),sQuery(id+"F0.wireOp",EDGE,"E11.86.2"),sQuery(id+"F0.wireOp",EDGE,"E11.86.3"),sQuery(id+"F0.wireOp",EDGE,"E11.86.4"),sQuery(id+"F0.wireOp",EDGE,"E11.86.5"),sQuery(id+"F0.wireOp",EDGE,"E11.86.6"),sQuery(id+"F0.wireOp",EDGE,"E11.87.0"),sQuery(id+"F0.wireOp",EDGE,"E11.87.1"),sQuery(id+"F0.wireOp",EDGE,"E11.87.2"),sQuery(id+"F0.wireOp",EDGE,"E11.87.3"),sQuery(id+"F0.wireOp",EDGE,"E11.87.4"),sQuery(id+"F0.wireOp",EDGE,"E11.87.5"),sQuery(id+"F0.wireOp",EDGE,"E11.87.6"),sQuery(id+"F0.wireOp",EDGE,"E11.88.0"),sQuery(id+"F0.wireOp",EDGE,"E11.88.1"),sQuery(id+"F0.wireOp",EDGE,"E11.88.2"),sQuery(id+"F0.wireOp",EDGE,"E11.88.3"),sQuery(id+"F0.wireOp",EDGE,"E11.88.4"),sQuery(id+"F0.wireOp",EDGE,"E11.88.5"),sQuery(id+"F0.wireOp",EDGE,"E11.88.6"),sQuery(id+"F0.wireOp",EDGE,"E11.89.0"),sQuery(id+"F0.wireOp",EDGE,"E11.89.1"),sQuery(id+"F0.wireOp",EDGE,"E11.89.2"),sQuery(id+"F0.wireOp",EDGE,"E11.89.3"),sQuery(id+"F0.wireOp",EDGE,"E11.89.4"),sQuery(id+"F0.wireOp",EDGE,"E11.89.5"),sQuery(id+"F0.wireOp",EDGE,"E11.89.6"),sQuery(id+"F0.wireOp",EDGE,"E11.90.0"),sQuery(id+"F0.wireOp",EDGE,"E11.90.1"),sQuery(id+"F0.wireOp",EDGE,"E11.90.2"),sQuery(id+"F0.wireOp",EDGE,"E11.90.3"),sQuery(id+"F0.wireOp",EDGE,"E11.90.4"),sQuery(id+"F0.wireOp",EDGE,"E11.90.5"),sQuery(id+"F0.wireOp",EDGE,"E11.90.6"),sQuery(id+"F0.wireOp",EDGE,"E11.91.0"),sQuery(id+"F0.wireOp",EDGE,"E11.91.1"),sQuery(id+"F0.wireOp",EDGE,"E11.91.2"),sQuery(id+"F0.wireOp",EDGE,"E11.91.3"),sQuery(id+"F0.wireOp",EDGE,"E11.91.4"),sQuery(id+"F0.wireOp",EDGE,"E11.91.5"),sQuery(id+"F0.wireOp",EDGE,"E11.91.6"),sQuery(id+"F0.wireOp",EDGE,"E11.92.0"),sQuery(id+"F0.wireOp",EDGE,"E11.92.1"),sQuery(id+"F0.wireOp",EDGE,"E11.92.2"),sQuery(id+"F0.wireOp",EDGE,"E11.92.3"),sQuery(id+"F0.wireOp",EDGE,"E11.92.4"),sQuery(id+"F0.wireOp",EDGE,"E11.92.5"),sQuery(id+"F0.wireOp",EDGE,"E11.92.6"),sQuery(id+"F0.wireOp",EDGE,"E11.93.0"),sQuery(id+"F0.wireOp",EDGE,"E11.93.1"),sQuery(id+"F0.wireOp",EDGE,"E11.93.2"),sQuery(id+"F0.wireOp",EDGE,"E11.93.3"),sQuery(id+"F0.wireOp",EDGE,"E11.93.4"),sQuery(id+"F0.wireOp",EDGE,"E11.93.5"),sQuery(id+"F0.wireOp",EDGE,"E11.93.6"),sQuery(id+"F0.wireOp",EDGE,"E11.94.0"),sQuery(id+"F0.wireOp",EDGE,"E11.94.1"),sQuery(id+"F0.wireOp",EDGE,"E11.94.2"),sQuery(id+"F0.wireOp",EDGE,"E11.94.3"),sQuery(id+"F0.wireOp",EDGE,"E11.94.4"),sQuery(id+"F0.wireOp",EDGE,"E11.94.5"),sQuery(id+"F0.wireOp",EDGE,"E11.94.6"),sQuery(id+"F0.wireOp",EDGE,"E11.95.0"),sQuery(id+"F0.wireOp",EDGE,"E11.95.1"),sQuery(id+"F0.wireOp",EDGE,"E11.95.2"),sQuery(id+"F0.wireOp",EDGE,"E11.95.3"),sQuery(id+"F0.wireOp",EDGE,"E11.95.4"),sQuery(id+"F0.wireOp",EDGE,"E11.95.5"),sQuery(id+"F0.wireOp",EDGE,"E11.95.6"),sQuery(id+"F0.wireOp",EDGE,"E11.96.0"),sQuery(id+"F0.wireOp",EDGE,"E11.96.1"),sQuery(id+"F0.wireOp",EDGE,"E11.96.2"),sQuery(id+"F0.wireOp",EDGE,"E11.96.3"),sQuery(id+"F0.wireOp",EDGE,"E11.96.4"),sQuery(id+"F0.wireOp",EDGE,"E11.96.5"),sQuery(id+"F0.wireOp",EDGE,"E11.96.6"),sQuery(id+"F0.wireOp",EDGE,"E11.97.0"),sQuery(id+"F0.wireOp",EDGE,"E11.97.1"),sQuery(id+"F0.wireOp",EDGE,"E11.97.2"),sQuery(id+"F0.wireOp",EDGE,"E11.97.3"),sQuery(id+"F0.wireOp",EDGE,"E11.97.4"),sQuery(id+"F0.wireOp",EDGE,"E11.97.5"),sQuery(id+"F0.wireOp",EDGE,"E11.97.6"),sQuery(id+"F0.wireOp",EDGE,"E11.98.0"),sQuery(id+"F0.wireOp",EDGE,"E11.98.1"),sQuery(id+"F0.wireOp",EDGE,"E11.98.2"),sQuery(id+"F0.wireOp",EDGE,"E11.98.3"),sQuery(id+"F0.wireOp",EDGE,"E11.98.4"),sQuery(id+"F0.wireOp",EDGE,"E11.98.5"),sQuery(id+"F0.wireOp",EDGE,"E11.98.6"),sQuery(id+"F0.wireOp",EDGE,"E11.99.0"),sQuery(id+"F0.wireOp",EDGE,"E11.99.1"),sQuery(id+"F0.wireOp",EDGE,"E11.99.2"),sQuery(id+"F0.wireOp",EDGE,"E11.99.3"),sQuery(id+"F0.wireOp",EDGE,"E11.99.4"),sQuery(id+"F0.wireOp",EDGE,"E11.99.5"),sQuery(id+"F0.wireOp",EDGE,"E11.99.6"),sQuery(id+"F0.wireOp",EDGE,"E18"),sQuery(id+"F0.wireOp",EDGE,"E19.trimOffspring"),sQuery(id+"F0.wireOp",EDGE,"E20.trimOffspring"),sQuery(id+"F0.wireOp",EDGE,"E21.trimOffspring"),sQuery(id+"F0.wireOp",EDGE,"E22.trimOffspring"),sQuery(id+"F0.wireOp",EDGE,"E23.trimOffspring"),sQuery(id+"F0.wireOp",EDGE,"E24.trimOffspring"),sQuery(id+"F0.wireOp",EDGE,"E25.trimOffspring"),sQuery(id+"F0.wireOp",EDGE,"E26.trimOffspring"),sQuery(id+"F0.wireOp",EDGE,"E27.trimOffspring"),sQuery(id+"F0.wireOp",EDGE,"E28.trimOffspring"),sQuery(id+"F0.wireOp",EDGE,"E29.trimOffspring"),sQuery(id+"F0.wireOp",EDGE,"E30.trimOffspring"),sQuery(id+"F0.wireOp",EDGE,"E31.trimOffspring"),sQuery(id+"F0.wireOp",EDGE,"E32.trimOffspring"),sQuery(id+"F0.wireOp",EDGE,"E33.trimOffspring"),sQuery(id+"F0.wireOp",EDGE,"E34.trimOffspring"),sQuery(id+"F0.wireOp",EDGE,"E35.trimOffspring"),sQuery(id+"F0.wireOp",EDGE,"E36.trimOffspring"),sQuery(id+"F0.wireOp",EDGE,"E37.trimOffspring"),sQuery(id+"F0.wireOp",EDGE,"E38.trimOffspring"),sQuery(id+"F0.wireOp",EDGE,"E39.trimOffspring"),sQuery(id+"F0.wireOp",EDGE,"E40.trimOffspring"),sQuery(id+"F0.wireOp",EDGE,"E41.trimOffspring"),sQuery(id+"F0.wireOp",EDGE,"E42.trimOffspring"),sQuery(id+"F0.wireOp",EDGE,"E43.trimOffspring"),sQuery(id+"F0.wireOp",EDGE,"E44.trimOffspring"),sQuery(id+"F0.wireOp",EDGE,"E45.trimOffspring"),sQuery(id+"F0.wireOp",EDGE,"E46.trimOffspring"),sQuery(id+"F0.wireOp",EDGE,"E47.trimOffspring"),sQuery(id+"F0.wireOp",EDGE,"E48.trimOffspring"),sQuery(id+"F0.wireOp",EDGE,"E49.trimOffspring"),sQuery(id+"F0.wireOp",EDGE,"E50.trimOffspring"),sQuery(id+"F0.wireOp",EDGE,"E51.trimOffspring"),sQuery(id+"F0.wireOp",EDGE,"E52.trimOffspring"),sQuery(id+"F0.wireOp",EDGE,"E53.trimOffspring"),sQuery(id+"F0.wireOp",EDGE,"E54.trimOffspring"),sQuery(id+"F0.wireOp",EDGE,"E55.trimOffspring"),sQuery(id+"F0.wireOp",EDGE,"E56.trimOffspring"),sQuery(id+"F0.wireOp",EDGE,"E57.trimOffspring"),sQuery(id+"F0.wireOp",EDGE,"E58.trimOffspring"),sQuery(id+"F0.wireOp",EDGE,"E59.trimOffspring"),sQuery(id+"F0.wireOp",EDGE,"E60.trimOffspring"),sQuery(id+"F0.wireOp",EDGE,"E61.trimOffspring"),sQuery(id+"F0.wireOp",EDGE,"E62.trimOffspring"),sQuery(id+"F0.wireOp",EDGE,"E63.trimOffspring"),sQuery(id+"F0.wireOp",EDGE,"E64.trimOffspring"),sQuery(id+"F0.wireOp",EDGE,"E65.trimOffspring"),sQuery(id+"F0.wireOp",EDGE,"E66.trimOffspring"),sQuery(id+"F0.wireOp",EDGE,"E67.trimOffspring"),sQuery(id+"F0.wireOp",EDGE,"E68.trimOffspring"),sQuery(id+"F0.wireOp",EDGE,"E69.trimOffspring"),sQuery(id+"F0.wireOp",EDGE,"E70.trimOffspring"),sQuery(id+"F0.wireOp",EDGE,"E71.trimOffspring"),sQuery(id+"F0.wireOp",EDGE,"E72.trimOffspring"),sQuery(id+"F0.wireOp",EDGE,"E73.trimOffspring"),sQuery(id+"F0.wireOp",EDGE,"E74.trimOffspring"),sQuery(id+"F0.wireOp",EDGE,"E75.trimOffspring"),sQuery(id+"F0.wireOp",EDGE,"E76.trimOffspring"),sQuery(id+"F0.wireOp",EDGE,"E77.trimOffspring"),sQuery(id+"F0.wireOp",EDGE,"E78.trimOffspring"),sQuery(id+"F0.wireOp",EDGE,"E79.trimOffspring"),sQuery(id+"F0.wireOp",EDGE,"E80.trimOffspring"),sQuery(id+"F0.wireOp",EDGE,"E81.trimOffspring"),sQuery(id+"F0.wireOp",EDGE,"E82.trimOffspring"),sQuery(id+"F0.wireOp",EDGE,"E83.trimOffspring"),sQuery(id+"F0.wireOp",EDGE,"E84.trimOffspring"),sQuery(id+"F0.wireOp",EDGE,"E85.trimOffspring"),sQuery(id+"F0.wireOp",EDGE,"E86.trimOffspring"),sQuery(id+"F0.wireOp",EDGE,"E87.trimOffspring"),sQuery(id+"F0.wireOp",EDGE,"E88.trimOffspring"),sQuery(id+"F0.wireOp",EDGE,"E89.trimOffspring"),sQuery(id+"F0.wireOp",EDGE,"E90.trimOffspring"),sQuery(id+"F0.wireOp",EDGE,"E91.trimOffspring"),sQuery(id+"F0.wireOp",EDGE,"E92.trimOffspring"),sQuery(id+"F0.wireOp",EDGE,"E93.trimOffspring"),sQuery(id+"F0.wireOp",EDGE,"E94.trimOffspring"),sQuery(id+"F0.wireOp",EDGE,"E95.trimOffspring"),sQuery(id+"F0.wireOp",EDGE,"E96.trimOffspring"),sQuery(id+"F0.wireOp",EDGE,"E97.trimOffspring"),sQuery(id+"F0.wireOp",EDGE,"E98.trimOffspring"),sQuery(id+"F0.wireOp",EDGE,"E99.trimOffspring"),sQuery(id+"F0.wireOp",EDGE,"E100.trimOffspring"),sQuery(id+"F0.wireOp",EDGE,"E101.trimOffspring"),sQuery(id+"F0.wireOp",EDGE,"E102.trimOffspring"),sQuery(id+"F0.wireOp",EDGE,"E103.trimOffspring"),sQuery(id+"F0.wireOp",EDGE,"E104.trimOffspring"),sQuery(id+"F0.wireOp",EDGE,"E105.trimOffspring"),sQuery(id+"F0.wireOp",EDGE,"E106.trimOffspring"),sQuery(id+"F0.wireOp",EDGE,"E107.trimOffspring"),sQuery(id+"F0.wireOp",EDGE,"E108.trimOffspring"),sQuery(id+"F0.wireOp",EDGE,"E109.trimOffspring"),sQuery(id+"F0.wireOp",EDGE,"E110.trimOffspring"),sQuery(id+"F0.wireOp",EDGE,"E111.trimOffspring"),sQuery(id+"F0.wireOp",EDGE,"E112.trimOffspring"),sQuery(id+"F0.wireOp",EDGE,"E113.trimOffspring"),sQuery(id+"F0.wireOp",EDGE,"E114.trimOffspring"),sQuery(id+"F0.wireOp",EDGE,"E115.trimOffspring"),sQuery(id+"F0.wireOp",EDGE,"E116.trimOffspring"),sQuery(id+"F0.wireOp",EDGE,"E117.trimOffspring")])],"isStart":false});
            var sketch = newSketch(context, id + "F3", { "sketchPlane" : qUnion([Q0])});
            skCircle(sketch, "E118", {"center": v(0, 0) * mm, "radius": 87.53 * mm});
            skSolve(sketch);
        }
        {
            var Q0;
            Q0=makeQuery(id+"F3.imprint","IMPRINT",FACE,{"disambiguationData":[TD([[makeQuery(id+"F3.imprint","IMPRINT",EDGE,{"derivedFrom":sQuery(id+"F3.wireOp",EDGE,"E118")}),1.0]])]});
            extrude(context, id + "F4", {"entities" : qUnion([Q0]), "operationType" : NewBodyOperationType.REMOVE, "oppositeDirection" : true, "depth" : 30 * mm, "offsetDistance" : 25 * mm, "hasDraft" : true, "draftAngle" : 8 * degree});
        }
        {
            var Q0;
            Q0=qCreatedBy(makeId("Front.planeOp"),FACE);
            var sketch = newSketch(context, id + "F5", { "sketchPlane" : qUnion([Q0])});
            skCircle(sketch, "E119", {"center": v(0, 0) * mm, "radius": 92 * mm});
            skCircle(sketch, "E120", {"center": v(0, 0) * mm, "radius": 99.93 * mm});
            skSolve(sketch);
        }
        {
            var Q0;
            Q0 = qSketchRegion(id + "F5", true);
            extrude(context, id + "F6", {"entities" : qUnion([Q0]), "operationType" : NewBodyOperationType.REMOVE, "depth" : 20 * mm, "offsetDistance" : 25 * mm});
        }
        {
            var Q0;
            Q0=qCreatedBy(makeId("Top.planeOp"),FACE);
            var Q1;
            Q1 = qBodyType(qCreatedBy(id + "F8" ,EDGE), BodyType.WIRE);
            cPlane(context, id + "F7", {"entities" : qUnion([Q0, Q1]), "cplaneType" : CPlaneType.OFFSET, "offset" : 101 * mm, "width" : 150 * mm, "height" : 150 * mm});
        }
        {
            var Q0;
            Q0=qCreatedBy(id+"F7.planeOp",FACE);
            var sketch = newSketch(context, id + "F8", { "sketchPlane" : qUnion([Q0])});
            skLineSegment(sketch, "E121.0.0", {"start": v(-2, 0) * mm, "end": v(2, 0) * mm});
            skLineSegment(sketch, "E121.0.1", {"start": v(-2, 0) * mm, "end": v(-2, -20) * mm});
            skLineSegment(sketch, "E121.0.2", {"start": v(-2, -20) * mm, "end": v(2, -20) * mm});
            skLineSegment(sketch, "E121.0.3", {"start": v(2, 0) * mm, "end": v(2, -20) * mm});
            skSolve(sketch);
        }
        {
            var Q0;
            Q0 = qSketchRegion(id + "F8", true);
            extrude(context, id + "F9", {"entities" : qUnion([Q0]), "oppositeDirection" : true, "depth" : 9.6 * mm, "offsetDistance" : 25 * mm, "hasSecondDirection" : true, "secondDirectionOppositeDirection" : false, "secondDirectionDepth" : -7 * mm});
        }
        {
            var Q0;
            Q0=makeQuery(id+"F9.opExtrude","SWEPT_BODY",BODY,{"disambiguationData":[OSD([sQuery(id+"F8.wireOp",EDGE,"E121.0.0"),sQuery(id+"F8.wireOp",EDGE,"E121.0.1"),sQuery(id+"F8.wireOp",EDGE,"E121.0.2"),sQuery(id+"F8.wireOp",EDGE,"E121.0.3")])]});
            var Q1;
            Q1=makeQuery(id+"F4.boolean.opBoolean","INTERSECT",EDGE,{"derivedFrom":[makeQuery(id+"F1.opExtrude","CAP_FACE",FACE,{"disambiguationData":[OSD([sQuery(id+"F0.wireOp",EDGE,"E4"),sQuery(id+"F0.wireOp",EDGE,"E5"),sQuery(id+"F0.wireOp",EDGE,"E6.filletArc"),sQuery(id+"F0.wireOp",EDGE,"E7.MirrorCS"),sQuery(id+"F0.wireOp",EDGE,"E8.MirrorCS"),sQuery(id+"F0.wireOp",EDGE,"E9.MirrorCS"),sQuery(id+"F0.wireOp",EDGE,"E10.filletArc"),sQuery(id+"F0.wireOp",EDGE,"E11.1.0"),sQuery(id+"F0.wireOp",EDGE,"E11.1.1"),sQuery(id+"F0.wireOp",EDGE,"E11.1.2"),sQuery(id+"F0.wireOp",EDGE,"E11.1.3"),sQuery(id+"F0.wireOp",EDGE,"E11.1.4"),sQuery(id+"F0.wireOp",EDGE,"E11.1.5"),sQuery(id+"F0.wireOp",EDGE,"E11.1.6"),sQuery(id+"F0.wireOp",EDGE,"E11.2.0"),sQuery(id+"F0.wireOp",EDGE,"E11.2.1"),sQuery(id+"F0.wireOp",EDGE,"E11.2.2"),sQuery(id+"F0.wireOp",EDGE,"E11.2.3"),sQuery(id+"F0.wireOp",EDGE,"E11.2.4"),sQuery(id+"F0.wireOp",EDGE,"E11.2.5"),sQuery(id+"F0.wireOp",EDGE,"E11.2.6"),sQuery(id+"F0.wireOp",EDGE,"E11.3.0"),sQuery(id+"F0.wireOp",EDGE,"E11.3.1"),sQuery(id+"F0.wireOp",EDGE,"E11.3.2"),sQuery(id+"F0.wireOp",EDGE,"E11.3.3"),sQuery(id+"F0.wireOp",EDGE,"E11.3.4"),sQuery(id+"F0.wireOp",EDGE,"E11.3.5"),sQuery(id+"F0.wireOp",EDGE,"E11.3.6"),sQuery(id+"F0.wireOp",EDGE,"E11.4.0"),sQuery(id+"F0.wireOp",EDGE,"E11.4.1"),sQuery(id+"F0.wireOp",EDGE,"E11.4.2"),sQuery(id+"F0.wireOp",EDGE,"E11.4.3"),sQuery(id+"F0.wireOp",EDGE,"E11.4.4"),sQuery(id+"F0.wireOp",EDGE,"E11.4.5"),sQuery(id+"F0.wireOp",EDGE,"E11.4.6"),sQuery(id+"F0.wireOp",EDGE,"E11.5.0"),sQuery(id+"F0.wireOp",EDGE,"E11.5.1"),sQuery(id+"F0.wireOp",EDGE,"E11.5.2"),sQuery(id+"F0.wireOp",EDGE,"E11.5.3"),sQuery(id+"F0.wireOp",EDGE,"E11.5.4"),sQuery(id+"F0.wireOp",EDGE,"E11.5.5"),sQuery(id+"F0.wireOp",EDGE,"E11.5.6"),sQuery(id+"F0.wireOp",EDGE,"E11.6.0"),sQuery(id+"F0.wireOp",EDGE,"E11.6.1"),sQuery(id+"F0.wireOp",EDGE,"E11.6.2"),sQuery(id+"F0.wireOp",EDGE,"E11.6.3"),sQuery(id+"F0.wireOp",EDGE,"E11.6.4"),sQuery(id+"F0.wireOp",EDGE,"E11.6.5"),sQuery(id+"F0.wireOp",EDGE,"E11.6.6"),sQuery(id+"F0.wireOp",EDGE,"E11.7.0"),sQuery(id+"F0.wireOp",EDGE,"E11.7.1"),sQuery(id+"F0.wireOp",EDGE,"E11.7.2"),sQuery(id+"F0.wireOp",EDGE,"E11.7.3"),sQuery(id+"F0.wireOp",EDGE,"E11.7.4"),sQuery(id+"F0.wireOp",EDGE,"E11.7.5"),sQuery(id+"F0.wireOp",EDGE,"E11.7.6"),sQuery(id+"F0.wireOp",EDGE,"E11.8.0"),sQuery(id+"F0.wireOp",EDGE,"E11.8.1"),sQuery(id+"F0.wireOp",EDGE,"E11.8.2"),sQuery(id+"F0.wireOp",EDGE,"E11.8.3"),sQuery(id+"F0.wireOp",EDGE,"E11.8.4"),sQuery(id+"F0.wireOp",EDGE,"E11.8.5"),sQuery(id+"F0.wireOp",EDGE,"E11.8.6"),sQuery(id+"F0.wireOp",EDGE,"E11.9.0"),sQuery(id+"F0.wireOp",EDGE,"E11.9.1"),sQuery(id+"F0.wireOp",EDGE,"E11.9.2"),sQuery(id+"F0.wireOp",EDGE,"E11.9.3"),sQuery(id+"F0.wireOp",EDGE,"E11.9.4"),sQuery(id+"F0.wireOp",EDGE,"E11.9.5"),sQuery(id+"F0.wireOp",EDGE,"E11.9.6"),sQuery(id+"F0.wireOp",EDGE,"E11.10.0"),sQuery(id+"F0.wireOp",EDGE,"E11.10.1"),sQuery(id+"F0.wireOp",EDGE,"E11.10.2"),sQuery(id+"F0.wireOp",EDGE,"E11.10.3"),sQuery(id+"F0.wireOp",EDGE,"E11.10.4"),sQuery(id+"F0.wireOp",EDGE,"E11.10.5"),sQuery(id+"F0.wireOp",EDGE,"E11.10.6"),sQuery(id+"F0.wireOp",EDGE,"E11.11.0"),sQuery(id+"F0.wireOp",EDGE,"E11.11.1"),sQuery(id+"F0.wireOp",EDGE,"E11.11.2"),sQuery(id+"F0.wireOp",EDGE,"E11.11.3"),sQuery(id+"F0.wireOp",EDGE,"E11.11.4"),sQuery(id+"F0.wireOp",EDGE,"E11.11.5"),sQuery(id+"F0.wireOp",EDGE,"E11.11.6"),sQuery(id+"F0.wireOp",EDGE,"E11.12.0"),sQuery(id+"F0.wireOp",EDGE,"E11.12.1"),sQuery(id+"F0.wireOp",EDGE,"E11.12.2"),sQuery(id+"F0.wireOp",EDGE,"E11.12.3"),sQuery(id+"F0.wireOp",EDGE,"E11.12.4"),sQuery(id+"F0.wireOp",EDGE,"E11.12.5"),sQuery(id+"F0.wireOp",EDGE,"E11.12.6"),sQuery(id+"F0.wireOp",EDGE,"E11.13.0"),sQuery(id+"F0.wireOp",EDGE,"E11.13.1"),sQuery(id+"F0.wireOp",EDGE,"E11.13.2"),sQuery(id+"F0.wireOp",EDGE,"E11.13.3"),sQuery(id+"F0.wireOp",EDGE,"E11.13.4"),sQuery(id+"F0.wireOp",EDGE,"E11.13.5"),sQuery(id+"F0.wireOp",EDGE,"E11.13.6"),sQuery(id+"F0.wireOp",EDGE,"E11.14.0"),sQuery(id+"F0.wireOp",EDGE,"E11.14.1"),sQuery(id+"F0.wireOp",EDGE,"E11.14.2"),sQuery(id+"F0.wireOp",EDGE,"E11.14.3"),sQuery(id+"F0.wireOp",EDGE,"E11.14.4"),sQuery(id+"F0.wireOp",EDGE,"E11.14.5"),sQuery(id+"F0.wireOp",EDGE,"E11.14.6"),sQuery(id+"F0.wireOp",EDGE,"E11.15.0"),sQuery(id+"F0.wireOp",EDGE,"E11.15.1"),sQuery(id+"F0.wireOp",EDGE,"E11.15.2"),sQuery(id+"F0.wireOp",EDGE,"E11.15.3"),sQuery(id+"F0.wireOp",EDGE,"E11.15.4"),sQuery(id+"F0.wireOp",EDGE,"E11.15.5"),sQuery(id+"F0.wireOp",EDGE,"E11.15.6"),sQuery(id+"F0.wireOp",EDGE,"E11.16.0"),sQuery(id+"F0.wireOp",EDGE,"E11.16.1"),sQuery(id+"F0.wireOp",EDGE,"E11.16.2"),sQuery(id+"F0.wireOp",EDGE,"E11.16.3"),sQuery(id+"F0.wireOp",EDGE,"E11.16.4"),sQuery(id+"F0.wireOp",EDGE,"E11.16.5"),sQuery(id+"F0.wireOp",EDGE,"E11.16.6"),sQuery(id+"F0.wireOp",EDGE,"E11.17.0"),sQuery(id+"F0.wireOp",EDGE,"E11.17.1"),sQuery(id+"F0.wireOp",EDGE,"E11.17.2"),sQuery(id+"F0.wireOp",EDGE,"E11.17.3"),sQuery(id+"F0.wireOp",EDGE,"E11.17.4"),sQuery(id+"F0.wireOp",EDGE,"E11.17.5"),sQuery(id+"F0.wireOp",EDGE,"E11.17.6"),sQuery(id+"F0.wireOp",EDGE,"E11.18.0"),sQuery(id+"F0.wireOp",EDGE,"E11.18.1"),sQuery(id+"F0.wireOp",EDGE,"E11.18.2"),sQuery(id+"F0.wireOp",EDGE,"E11.18.3"),sQuery(id+"F0.wireOp",EDGE,"E11.18.4"),sQuery(id+"F0.wireOp",EDGE,"E11.18.5"),sQuery(id+"F0.wireOp",EDGE,"E11.18.6"),sQuery(id+"F0.wireOp",EDGE,"E11.19.0"),sQuery(id+"F0.wireOp",EDGE,"E11.19.1"),sQuery(id+"F0.wireOp",EDGE,"E11.19.2"),sQuery(id+"F0.wireOp",EDGE,"E11.19.3"),sQuery(id+"F0.wireOp",EDGE,"E11.19.4"),sQuery(id+"F0.wireOp",EDGE,"E11.19.5"),sQuery(id+"F0.wireOp",EDGE,"E11.19.6"),sQuery(id+"F0.wireOp",EDGE,"E11.20.0"),sQuery(id+"F0.wireOp",EDGE,"E11.20.1"),sQuery(id+"F0.wireOp",EDGE,"E11.20.2"),sQuery(id+"F0.wireOp",EDGE,"E11.20.3"),sQuery(id+"F0.wireOp",EDGE,"E11.20.4"),sQuery(id+"F0.wireOp",EDGE,"E11.20.5"),sQuery(id+"F0.wireOp",EDGE,"E11.20.6"),sQuery(id+"F0.wireOp",EDGE,"E11.21.0"),sQuery(id+"F0.wireOp",EDGE,"E11.21.1"),sQuery(id+"F0.wireOp",EDGE,"E11.21.2"),sQuery(id+"F0.wireOp",EDGE,"E11.21.3"),sQuery(id+"F0.wireOp",EDGE,"E11.21.4"),sQuery(id+"F0.wireOp",EDGE,"E11.21.5"),sQuery(id+"F0.wireOp",EDGE,"E11.21.6"),sQuery(id+"F0.wireOp",EDGE,"E11.22.0"),sQuery(id+"F0.wireOp",EDGE,"E11.22.1"),sQuery(id+"F0.wireOp",EDGE,"E11.22.2"),sQuery(id+"F0.wireOp",EDGE,"E11.22.3"),sQuery(id+"F0.wireOp",EDGE,"E11.22.4"),sQuery(id+"F0.wireOp",EDGE,"E11.22.5"),sQuery(id+"F0.wireOp",EDGE,"E11.22.6"),sQuery(id+"F0.wireOp",EDGE,"E11.23.0"),sQuery(id+"F0.wireOp",EDGE,"E11.23.1"),sQuery(id+"F0.wireOp",EDGE,"E11.23.2"),sQuery(id+"F0.wireOp",EDGE,"E11.23.3"),sQuery(id+"F0.wireOp",EDGE,"E11.23.4"),sQuery(id+"F0.wireOp",EDGE,"E11.23.5"),sQuery(id+"F0.wireOp",EDGE,"E11.23.6"),sQuery(id+"F0.wireOp",EDGE,"E11.24.0"),sQuery(id+"F0.wireOp",EDGE,"E11.24.1"),sQuery(id+"F0.wireOp",EDGE,"E11.24.2"),sQuery(id+"F0.wireOp",EDGE,"E11.24.3"),sQuery(id+"F0.wireOp",EDGE,"E11.24.4"),sQuery(id+"F0.wireOp",EDGE,"E11.24.5"),sQuery(id+"F0.wireOp",EDGE,"E11.24.6"),sQuery(id+"F0.wireOp",EDGE,"E11.25.0"),sQuery(id+"F0.wireOp",EDGE,"E11.25.1"),sQuery(id+"F0.wireOp",EDGE,"E11.25.2"),sQuery(id+"F0.wireOp",EDGE,"E11.25.3"),sQuery(id+"F0.wireOp",EDGE,"E11.25.4"),sQuery(id+"F0.wireOp",EDGE,"E11.25.5"),sQuery(id+"F0.wireOp",EDGE,"E11.25.6"),sQuery(id+"F0.wireOp",EDGE,"E11.26.0"),sQuery(id+"F0.wireOp",EDGE,"E11.26.1"),sQuery(id+"F0.wireOp",EDGE,"E11.26.2"),sQuery(id+"F0.wireOp",EDGE,"E11.26.3"),sQuery(id+"F0.wireOp",EDGE,"E11.26.4"),sQuery(id+"F0.wireOp",EDGE,"E11.26.5"),sQuery(id+"F0.wireOp",EDGE,"E11.26.6"),sQuery(id+"F0.wireOp",EDGE,"E11.27.0"),sQuery(id+"F0.wireOp",EDGE,"E11.27.1"),sQuery(id+"F0.wireOp",EDGE,"E11.27.2"),sQuery(id+"F0.wireOp",EDGE,"E11.27.3"),sQuery(id+"F0.wireOp",EDGE,"E11.27.4"),sQuery(id+"F0.wireOp",EDGE,"E11.27.5"),sQuery(id+"F0.wireOp",EDGE,"E11.27.6"),sQuery(id+"F0.wireOp",EDGE,"E11.28.0"),sQuery(id+"F0.wireOp",EDGE,"E11.28.1"),sQuery(id+"F0.wireOp",EDGE,"E11.28.2"),sQuery(id+"F0.wireOp",EDGE,"E11.28.3"),sQuery(id+"F0.wireOp",EDGE,"E11.28.4"),sQuery(id+"F0.wireOp",EDGE,"E11.28.5"),sQuery(id+"F0.wireOp",EDGE,"E11.28.6"),sQuery(id+"F0.wireOp",EDGE,"E11.29.0"),sQuery(id+"F0.wireOp",EDGE,"E11.29.1"),sQuery(id+"F0.wireOp",EDGE,"E11.29.2"),sQuery(id+"F0.wireOp",EDGE,"E11.29.3"),sQuery(id+"F0.wireOp",EDGE,"E11.29.4"),sQuery(id+"F0.wireOp",EDGE,"E11.29.5"),sQuery(id+"F0.wireOp",EDGE,"E11.29.6"),sQuery(id+"F0.wireOp",EDGE,"E11.30.0"),sQuery(id+"F0.wireOp",EDGE,"E11.30.1"),sQuery(id+"F0.wireOp",EDGE,"E11.30.2"),sQuery(id+"F0.wireOp",EDGE,"E11.30.3"),sQuery(id+"F0.wireOp",EDGE,"E11.30.4"),sQuery(id+"F0.wireOp",EDGE,"E11.30.5"),sQuery(id+"F0.wireOp",EDGE,"E11.30.6"),sQuery(id+"F0.wireOp",EDGE,"E11.31.0"),sQuery(id+"F0.wireOp",EDGE,"E11.31.1"),sQuery(id+"F0.wireOp",EDGE,"E11.31.2"),sQuery(id+"F0.wireOp",EDGE,"E11.31.3"),sQuery(id+"F0.wireOp",EDGE,"E11.31.4"),sQuery(id+"F0.wireOp",EDGE,"E11.31.5"),sQuery(id+"F0.wireOp",EDGE,"E11.31.6"),sQuery(id+"F0.wireOp",EDGE,"E11.32.0"),sQuery(id+"F0.wireOp",EDGE,"E11.32.1"),sQuery(id+"F0.wireOp",EDGE,"E11.32.2"),sQuery(id+"F0.wireOp",EDGE,"E11.32.3"),sQuery(id+"F0.wireOp",EDGE,"E11.32.4"),sQuery(id+"F0.wireOp",EDGE,"E11.32.5"),sQuery(id+"F0.wireOp",EDGE,"E11.32.6"),sQuery(id+"F0.wireOp",EDGE,"E11.33.0"),sQuery(id+"F0.wireOp",EDGE,"E11.33.1"),sQuery(id+"F0.wireOp",EDGE,"E11.33.2"),sQuery(id+"F0.wireOp",EDGE,"E11.33.3"),sQuery(id+"F0.wireOp",EDGE,"E11.33.4"),sQuery(id+"F0.wireOp",EDGE,"E11.33.5"),sQuery(id+"F0.wireOp",EDGE,"E11.33.6"),sQuery(id+"F0.wireOp",EDGE,"E11.34.0"),sQuery(id+"F0.wireOp",EDGE,"E11.34.1"),sQuery(id+"F0.wireOp",EDGE,"E11.34.2"),sQuery(id+"F0.wireOp",EDGE,"E11.34.3"),sQuery(id+"F0.wireOp",EDGE,"E11.34.4"),sQuery(id+"F0.wireOp",EDGE,"E11.34.5"),sQuery(id+"F0.wireOp",EDGE,"E11.34.6"),sQuery(id+"F0.wireOp",EDGE,"E11.35.0"),sQuery(id+"F0.wireOp",EDGE,"E11.35.1"),sQuery(id+"F0.wireOp",EDGE,"E11.35.2"),sQuery(id+"F0.wireOp",EDGE,"E11.35.3"),sQuery(id+"F0.wireOp",EDGE,"E11.35.4"),sQuery(id+"F0.wireOp",EDGE,"E11.35.5"),sQuery(id+"F0.wireOp",EDGE,"E11.35.6"),sQuery(id+"F0.wireOp",EDGE,"E11.36.0"),sQuery(id+"F0.wireOp",EDGE,"E11.36.1"),sQuery(id+"F0.wireOp",EDGE,"E11.36.2"),sQuery(id+"F0.wireOp",EDGE,"E11.36.3"),sQuery(id+"F0.wireOp",EDGE,"E11.36.4"),sQuery(id+"F0.wireOp",EDGE,"E11.36.5"),sQuery(id+"F0.wireOp",EDGE,"E11.36.6"),sQuery(id+"F0.wireOp",EDGE,"E11.37.0"),sQuery(id+"F0.wireOp",EDGE,"E11.37.1"),sQuery(id+"F0.wireOp",EDGE,"E11.37.2"),sQuery(id+"F0.wireOp",EDGE,"E11.37.3"),sQuery(id+"F0.wireOp",EDGE,"E11.37.4"),sQuery(id+"F0.wireOp",EDGE,"E11.37.5"),sQuery(id+"F0.wireOp",EDGE,"E11.37.6"),sQuery(id+"F0.wireOp",EDGE,"E11.38.0"),sQuery(id+"F0.wireOp",EDGE,"E11.38.1"),sQuery(id+"F0.wireOp",EDGE,"E11.38.2"),sQuery(id+"F0.wireOp",EDGE,"E11.38.3"),sQuery(id+"F0.wireOp",EDGE,"E11.38.4"),sQuery(id+"F0.wireOp",EDGE,"E11.38.5"),sQuery(id+"F0.wireOp",EDGE,"E11.38.6"),sQuery(id+"F0.wireOp",EDGE,"E11.39.0"),sQuery(id+"F0.wireOp",EDGE,"E11.39.1"),sQuery(id+"F0.wireOp",EDGE,"E11.39.2"),sQuery(id+"F0.wireOp",EDGE,"E11.39.3"),sQuery(id+"F0.wireOp",EDGE,"E11.39.4"),sQuery(id+"F0.wireOp",EDGE,"E11.39.5"),sQuery(id+"F0.wireOp",EDGE,"E11.39.6"),sQuery(id+"F0.wireOp",EDGE,"E11.40.0"),sQuery(id+"F0.wireOp",EDGE,"E11.40.1"),sQuery(id+"F0.wireOp",EDGE,"E11.40.2"),sQuery(id+"F0.wireOp",EDGE,"E11.40.3"),sQuery(id+"F0.wireOp",EDGE,"E11.40.4"),sQuery(id+"F0.wireOp",EDGE,"E11.40.5"),sQuery(id+"F0.wireOp",EDGE,"E11.40.6"),sQuery(id+"F0.wireOp",EDGE,"E11.41.0"),sQuery(id+"F0.wireOp",EDGE,"E11.41.1"),sQuery(id+"F0.wireOp",EDGE,"E11.41.2"),sQuery(id+"F0.wireOp",EDGE,"E11.41.3"),sQuery(id+"F0.wireOp",EDGE,"E11.41.4"),sQuery(id+"F0.wireOp",EDGE,"E11.41.5"),sQuery(id+"F0.wireOp",EDGE,"E11.41.6"),sQuery(id+"F0.wireOp",EDGE,"E11.42.0"),sQuery(id+"F0.wireOp",EDGE,"E11.42.1"),sQuery(id+"F0.wireOp",EDGE,"E11.42.2"),sQuery(id+"F0.wireOp",EDGE,"E11.42.3"),sQuery(id+"F0.wireOp",EDGE,"E11.42.4"),sQuery(id+"F0.wireOp",EDGE,"E11.42.5"),sQuery(id+"F0.wireOp",EDGE,"E11.42.6"),sQuery(id+"F0.wireOp",EDGE,"E11.43.0"),sQuery(id+"F0.wireOp",EDGE,"E11.43.1"),sQuery(id+"F0.wireOp",EDGE,"E11.43.2"),sQuery(id+"F0.wireOp",EDGE,"E11.43.3"),sQuery(id+"F0.wireOp",EDGE,"E11.43.4"),sQuery(id+"F0.wireOp",EDGE,"E11.43.5"),sQuery(id+"F0.wireOp",EDGE,"E11.43.6"),sQuery(id+"F0.wireOp",EDGE,"E11.44.0"),sQuery(id+"F0.wireOp",EDGE,"E11.44.1"),sQuery(id+"F0.wireOp",EDGE,"E11.44.2"),sQuery(id+"F0.wireOp",EDGE,"E11.44.3"),sQuery(id+"F0.wireOp",EDGE,"E11.44.4"),sQuery(id+"F0.wireOp",EDGE,"E11.44.5"),sQuery(id+"F0.wireOp",EDGE,"E11.44.6"),sQuery(id+"F0.wireOp",EDGE,"E11.45.0"),sQuery(id+"F0.wireOp",EDGE,"E11.45.1"),sQuery(id+"F0.wireOp",EDGE,"E11.45.2"),sQuery(id+"F0.wireOp",EDGE,"E11.45.3"),sQuery(id+"F0.wireOp",EDGE,"E11.45.4"),sQuery(id+"F0.wireOp",EDGE,"E11.45.5"),sQuery(id+"F0.wireOp",EDGE,"E11.45.6"),sQuery(id+"F0.wireOp",EDGE,"E11.46.0"),sQuery(id+"F0.wireOp",EDGE,"E11.46.1"),sQuery(id+"F0.wireOp",EDGE,"E11.46.2"),sQuery(id+"F0.wireOp",EDGE,"E11.46.3"),sQuery(id+"F0.wireOp",EDGE,"E11.46.4"),sQuery(id+"F0.wireOp",EDGE,"E11.46.5"),sQuery(id+"F0.wireOp",EDGE,"E11.46.6"),sQuery(id+"F0.wireOp",EDGE,"E11.47.0"),sQuery(id+"F0.wireOp",EDGE,"E11.47.1"),sQuery(id+"F0.wireOp",EDGE,"E11.47.2"),sQuery(id+"F0.wireOp",EDGE,"E11.47.3"),sQuery(id+"F0.wireOp",EDGE,"E11.47.4"),sQuery(id+"F0.wireOp",EDGE,"E11.47.5"),sQuery(id+"F0.wireOp",EDGE,"E11.47.6"),sQuery(id+"F0.wireOp",EDGE,"E11.48.0"),sQuery(id+"F0.wireOp",EDGE,"E11.48.1"),sQuery(id+"F0.wireOp",EDGE,"E11.48.2"),sQuery(id+"F0.wireOp",EDGE,"E11.48.3"),sQuery(id+"F0.wireOp",EDGE,"E11.48.4"),sQuery(id+"F0.wireOp",EDGE,"E11.48.5"),sQuery(id+"F0.wireOp",EDGE,"E11.48.6"),sQuery(id+"F0.wireOp",EDGE,"E11.49.0"),sQuery(id+"F0.wireOp",EDGE,"E11.49.1"),sQuery(id+"F0.wireOp",EDGE,"E11.49.2"),sQuery(id+"F0.wireOp",EDGE,"E11.49.3"),sQuery(id+"F0.wireOp",EDGE,"E11.49.4"),sQuery(id+"F0.wireOp",EDGE,"E11.49.5"),sQuery(id+"F0.wireOp",EDGE,"E11.49.6"),sQuery(id+"F0.wireOp",EDGE,"E11.50.0"),sQuery(id+"F0.wireOp",EDGE,"E11.50.1"),sQuery(id+"F0.wireOp",EDGE,"E11.50.2"),sQuery(id+"F0.wireOp",EDGE,"E11.50.3"),sQuery(id+"F0.wireOp",EDGE,"E11.50.4"),sQuery(id+"F0.wireOp",EDGE,"E11.50.5"),sQuery(id+"F0.wireOp",EDGE,"E11.50.6"),sQuery(id+"F0.wireOp",EDGE,"E11.51.0"),sQuery(id+"F0.wireOp",EDGE,"E11.51.1"),sQuery(id+"F0.wireOp",EDGE,"E11.51.2"),sQuery(id+"F0.wireOp",EDGE,"E11.51.3"),sQuery(id+"F0.wireOp",EDGE,"E11.51.4"),sQuery(id+"F0.wireOp",EDGE,"E11.51.5"),sQuery(id+"F0.wireOp",EDGE,"E11.51.6"),sQuery(id+"F0.wireOp",EDGE,"E11.52.0"),sQuery(id+"F0.wireOp",EDGE,"E11.52.1"),sQuery(id+"F0.wireOp",EDGE,"E11.52.2"),sQuery(id+"F0.wireOp",EDGE,"E11.52.3"),sQuery(id+"F0.wireOp",EDGE,"E11.52.4"),sQuery(id+"F0.wireOp",EDGE,"E11.52.5"),sQuery(id+"F0.wireOp",EDGE,"E11.52.6"),sQuery(id+"F0.wireOp",EDGE,"E11.53.0"),sQuery(id+"F0.wireOp",EDGE,"E11.53.1"),sQuery(id+"F0.wireOp",EDGE,"E11.53.2"),sQuery(id+"F0.wireOp",EDGE,"E11.53.3"),sQuery(id+"F0.wireOp",EDGE,"E11.53.4"),sQuery(id+"F0.wireOp",EDGE,"E11.53.5"),sQuery(id+"F0.wireOp",EDGE,"E11.53.6"),sQuery(id+"F0.wireOp",EDGE,"E11.54.0"),sQuery(id+"F0.wireOp",EDGE,"E11.54.1"),sQuery(id+"F0.wireOp",EDGE,"E11.54.2"),sQuery(id+"F0.wireOp",EDGE,"E11.54.3"),sQuery(id+"F0.wireOp",EDGE,"E11.54.4"),sQuery(id+"F0.wireOp",EDGE,"E11.54.5"),sQuery(id+"F0.wireOp",EDGE,"E11.54.6"),sQuery(id+"F0.wireOp",EDGE,"E11.55.0"),sQuery(id+"F0.wireOp",EDGE,"E11.55.1"),sQuery(id+"F0.wireOp",EDGE,"E11.55.2"),sQuery(id+"F0.wireOp",EDGE,"E11.55.3"),sQuery(id+"F0.wireOp",EDGE,"E11.55.4"),sQuery(id+"F0.wireOp",EDGE,"E11.55.5"),sQuery(id+"F0.wireOp",EDGE,"E11.55.6"),sQuery(id+"F0.wireOp",EDGE,"E11.56.0"),sQuery(id+"F0.wireOp",EDGE,"E11.56.1"),sQuery(id+"F0.wireOp",EDGE,"E11.56.2"),sQuery(id+"F0.wireOp",EDGE,"E11.56.3"),sQuery(id+"F0.wireOp",EDGE,"E11.56.4"),sQuery(id+"F0.wireOp",EDGE,"E11.56.5"),sQuery(id+"F0.wireOp",EDGE,"E11.56.6"),sQuery(id+"F0.wireOp",EDGE,"E11.57.0"),sQuery(id+"F0.wireOp",EDGE,"E11.57.1"),sQuery(id+"F0.wireOp",EDGE,"E11.57.2"),sQuery(id+"F0.wireOp",EDGE,"E11.57.3"),sQuery(id+"F0.wireOp",EDGE,"E11.57.4"),sQuery(id+"F0.wireOp",EDGE,"E11.57.5"),sQuery(id+"F0.wireOp",EDGE,"E11.57.6"),sQuery(id+"F0.wireOp",EDGE,"E11.58.0"),sQuery(id+"F0.wireOp",EDGE,"E11.58.1"),sQuery(id+"F0.wireOp",EDGE,"E11.58.2"),sQuery(id+"F0.wireOp",EDGE,"E11.58.3"),sQuery(id+"F0.wireOp",EDGE,"E11.58.4"),sQuery(id+"F0.wireOp",EDGE,"E11.58.5"),sQuery(id+"F0.wireOp",EDGE,"E11.58.6"),sQuery(id+"F0.wireOp",EDGE,"E11.59.0"),sQuery(id+"F0.wireOp",EDGE,"E11.59.1"),sQuery(id+"F0.wireOp",EDGE,"E11.59.2"),sQuery(id+"F0.wireOp",EDGE,"E11.59.3"),sQuery(id+"F0.wireOp",EDGE,"E11.59.4"),sQuery(id+"F0.wireOp",EDGE,"E11.59.5"),sQuery(id+"F0.wireOp",EDGE,"E11.59.6"),sQuery(id+"F0.wireOp",EDGE,"E11.60.0"),sQuery(id+"F0.wireOp",EDGE,"E11.60.1"),sQuery(id+"F0.wireOp",EDGE,"E11.60.2"),sQuery(id+"F0.wireOp",EDGE,"E11.60.3"),sQuery(id+"F0.wireOp",EDGE,"E11.60.4"),sQuery(id+"F0.wireOp",EDGE,"E11.60.5"),sQuery(id+"F0.wireOp",EDGE,"E11.60.6"),sQuery(id+"F0.wireOp",EDGE,"E11.61.0"),sQuery(id+"F0.wireOp",EDGE,"E11.61.1"),sQuery(id+"F0.wireOp",EDGE,"E11.61.2"),sQuery(id+"F0.wireOp",EDGE,"E11.61.3"),sQuery(id+"F0.wireOp",EDGE,"E11.61.4"),sQuery(id+"F0.wireOp",EDGE,"E11.61.5"),sQuery(id+"F0.wireOp",EDGE,"E11.61.6"),sQuery(id+"F0.wireOp",EDGE,"E11.62.0"),sQuery(id+"F0.wireOp",EDGE,"E11.62.1"),sQuery(id+"F0.wireOp",EDGE,"E11.62.2"),sQuery(id+"F0.wireOp",EDGE,"E11.62.3"),sQuery(id+"F0.wireOp",EDGE,"E11.62.4"),sQuery(id+"F0.wireOp",EDGE,"E11.62.5"),sQuery(id+"F0.wireOp",EDGE,"E11.62.6"),sQuery(id+"F0.wireOp",EDGE,"E11.63.0"),sQuery(id+"F0.wireOp",EDGE,"E11.63.1"),sQuery(id+"F0.wireOp",EDGE,"E11.63.2"),sQuery(id+"F0.wireOp",EDGE,"E11.63.3"),sQuery(id+"F0.wireOp",EDGE,"E11.63.4"),sQuery(id+"F0.wireOp",EDGE,"E11.63.5"),sQuery(id+"F0.wireOp",EDGE,"E11.63.6"),sQuery(id+"F0.wireOp",EDGE,"E11.64.0"),sQuery(id+"F0.wireOp",EDGE,"E11.64.1"),sQuery(id+"F0.wireOp",EDGE,"E11.64.2"),sQuery(id+"F0.wireOp",EDGE,"E11.64.3"),sQuery(id+"F0.wireOp",EDGE,"E11.64.4"),sQuery(id+"F0.wireOp",EDGE,"E11.64.5"),sQuery(id+"F0.wireOp",EDGE,"E11.64.6"),sQuery(id+"F0.wireOp",EDGE,"E11.65.0"),sQuery(id+"F0.wireOp",EDGE,"E11.65.1"),sQuery(id+"F0.wireOp",EDGE,"E11.65.2"),sQuery(id+"F0.wireOp",EDGE,"E11.65.3"),sQuery(id+"F0.wireOp",EDGE,"E11.65.4"),sQuery(id+"F0.wireOp",EDGE,"E11.65.5"),sQuery(id+"F0.wireOp",EDGE,"E11.65.6"),sQuery(id+"F0.wireOp",EDGE,"E11.66.0"),sQuery(id+"F0.wireOp",EDGE,"E11.66.1"),sQuery(id+"F0.wireOp",EDGE,"E11.66.2"),sQuery(id+"F0.wireOp",EDGE,"E11.66.3"),sQuery(id+"F0.wireOp",EDGE,"E11.66.4"),sQuery(id+"F0.wireOp",EDGE,"E11.66.5"),sQuery(id+"F0.wireOp",EDGE,"E11.66.6"),sQuery(id+"F0.wireOp",EDGE,"E11.67.0"),sQuery(id+"F0.wireOp",EDGE,"E11.67.1"),sQuery(id+"F0.wireOp",EDGE,"E11.67.2"),sQuery(id+"F0.wireOp",EDGE,"E11.67.3"),sQuery(id+"F0.wireOp",EDGE,"E11.67.4"),sQuery(id+"F0.wireOp",EDGE,"E11.67.5"),sQuery(id+"F0.wireOp",EDGE,"E11.67.6"),sQuery(id+"F0.wireOp",EDGE,"E11.68.0"),sQuery(id+"F0.wireOp",EDGE,"E11.68.1"),sQuery(id+"F0.wireOp",EDGE,"E11.68.2"),sQuery(id+"F0.wireOp",EDGE,"E11.68.3"),sQuery(id+"F0.wireOp",EDGE,"E11.68.4"),sQuery(id+"F0.wireOp",EDGE,"E11.68.5"),sQuery(id+"F0.wireOp",EDGE,"E11.68.6"),sQuery(id+"F0.wireOp",EDGE,"E11.69.0"),sQuery(id+"F0.wireOp",EDGE,"E11.69.1"),sQuery(id+"F0.wireOp",EDGE,"E11.69.2"),sQuery(id+"F0.wireOp",EDGE,"E11.69.3"),sQuery(id+"F0.wireOp",EDGE,"E11.69.4"),sQuery(id+"F0.wireOp",EDGE,"E11.69.5"),sQuery(id+"F0.wireOp",EDGE,"E11.69.6"),sQuery(id+"F0.wireOp",EDGE,"E11.70.0"),sQuery(id+"F0.wireOp",EDGE,"E11.70.1"),sQuery(id+"F0.wireOp",EDGE,"E11.70.2"),sQuery(id+"F0.wireOp",EDGE,"E11.70.3"),sQuery(id+"F0.wireOp",EDGE,"E11.70.4"),sQuery(id+"F0.wireOp",EDGE,"E11.70.5"),sQuery(id+"F0.wireOp",EDGE,"E11.70.6"),sQuery(id+"F0.wireOp",EDGE,"E11.71.0"),sQuery(id+"F0.wireOp",EDGE,"E11.71.1"),sQuery(id+"F0.wireOp",EDGE,"E11.71.2"),sQuery(id+"F0.wireOp",EDGE,"E11.71.3"),sQuery(id+"F0.wireOp",EDGE,"E11.71.4"),sQuery(id+"F0.wireOp",EDGE,"E11.71.5"),sQuery(id+"F0.wireOp",EDGE,"E11.71.6"),sQuery(id+"F0.wireOp",EDGE,"E11.72.0"),sQuery(id+"F0.wireOp",EDGE,"E11.72.1"),sQuery(id+"F0.wireOp",EDGE,"E11.72.2"),sQuery(id+"F0.wireOp",EDGE,"E11.72.3"),sQuery(id+"F0.wireOp",EDGE,"E11.72.4"),sQuery(id+"F0.wireOp",EDGE,"E11.72.5"),sQuery(id+"F0.wireOp",EDGE,"E11.72.6"),sQuery(id+"F0.wireOp",EDGE,"E11.73.0"),sQuery(id+"F0.wireOp",EDGE,"E11.73.1"),sQuery(id+"F0.wireOp",EDGE,"E11.73.2"),sQuery(id+"F0.wireOp",EDGE,"E11.73.3"),sQuery(id+"F0.wireOp",EDGE,"E11.73.4"),sQuery(id+"F0.wireOp",EDGE,"E11.73.5"),sQuery(id+"F0.wireOp",EDGE,"E11.73.6"),sQuery(id+"F0.wireOp",EDGE,"E11.74.0"),sQuery(id+"F0.wireOp",EDGE,"E11.74.1"),sQuery(id+"F0.wireOp",EDGE,"E11.74.2"),sQuery(id+"F0.wireOp",EDGE,"E11.74.3"),sQuery(id+"F0.wireOp",EDGE,"E11.74.4"),sQuery(id+"F0.wireOp",EDGE,"E11.74.5"),sQuery(id+"F0.wireOp",EDGE,"E11.74.6"),sQuery(id+"F0.wireOp",EDGE,"E11.75.0"),sQuery(id+"F0.wireOp",EDGE,"E11.75.1"),sQuery(id+"F0.wireOp",EDGE,"E11.75.2"),sQuery(id+"F0.wireOp",EDGE,"E11.75.3"),sQuery(id+"F0.wireOp",EDGE,"E11.75.4"),sQuery(id+"F0.wireOp",EDGE,"E11.75.5"),sQuery(id+"F0.wireOp",EDGE,"E11.75.6"),sQuery(id+"F0.wireOp",EDGE,"E11.76.0"),sQuery(id+"F0.wireOp",EDGE,"E11.76.1"),sQuery(id+"F0.wireOp",EDGE,"E11.76.2"),sQuery(id+"F0.wireOp",EDGE,"E11.76.3"),sQuery(id+"F0.wireOp",EDGE,"E11.76.4"),sQuery(id+"F0.wireOp",EDGE,"E11.76.5"),sQuery(id+"F0.wireOp",EDGE,"E11.76.6"),sQuery(id+"F0.wireOp",EDGE,"E11.77.0"),sQuery(id+"F0.wireOp",EDGE,"E11.77.1"),sQuery(id+"F0.wireOp",EDGE,"E11.77.2"),sQuery(id+"F0.wireOp",EDGE,"E11.77.3"),sQuery(id+"F0.wireOp",EDGE,"E11.77.4"),sQuery(id+"F0.wireOp",EDGE,"E11.77.5"),sQuery(id+"F0.wireOp",EDGE,"E11.77.6"),sQuery(id+"F0.wireOp",EDGE,"E11.78.0"),sQuery(id+"F0.wireOp",EDGE,"E11.78.1"),sQuery(id+"F0.wireOp",EDGE,"E11.78.2"),sQuery(id+"F0.wireOp",EDGE,"E11.78.3"),sQuery(id+"F0.wireOp",EDGE,"E11.78.4"),sQuery(id+"F0.wireOp",EDGE,"E11.78.5"),sQuery(id+"F0.wireOp",EDGE,"E11.78.6"),sQuery(id+"F0.wireOp",EDGE,"E11.79.0"),sQuery(id+"F0.wireOp",EDGE,"E11.79.1"),sQuery(id+"F0.wireOp",EDGE,"E11.79.2"),sQuery(id+"F0.wireOp",EDGE,"E11.79.3"),sQuery(id+"F0.wireOp",EDGE,"E11.79.4"),sQuery(id+"F0.wireOp",EDGE,"E11.79.5"),sQuery(id+"F0.wireOp",EDGE,"E11.79.6"),sQuery(id+"F0.wireOp",EDGE,"E11.80.0"),sQuery(id+"F0.wireOp",EDGE,"E11.80.1"),sQuery(id+"F0.wireOp",EDGE,"E11.80.2"),sQuery(id+"F0.wireOp",EDGE,"E11.80.3"),sQuery(id+"F0.wireOp",EDGE,"E11.80.4"),sQuery(id+"F0.wireOp",EDGE,"E11.80.5"),sQuery(id+"F0.wireOp",EDGE,"E11.80.6"),sQuery(id+"F0.wireOp",EDGE,"E11.81.0"),sQuery(id+"F0.wireOp",EDGE,"E11.81.1"),sQuery(id+"F0.wireOp",EDGE,"E11.81.2"),sQuery(id+"F0.wireOp",EDGE,"E11.81.3"),sQuery(id+"F0.wireOp",EDGE,"E11.81.4"),sQuery(id+"F0.wireOp",EDGE,"E11.81.5"),sQuery(id+"F0.wireOp",EDGE,"E11.81.6"),sQuery(id+"F0.wireOp",EDGE,"E11.82.0"),sQuery(id+"F0.wireOp",EDGE,"E11.82.1"),sQuery(id+"F0.wireOp",EDGE,"E11.82.2"),sQuery(id+"F0.wireOp",EDGE,"E11.82.3"),sQuery(id+"F0.wireOp",EDGE,"E11.82.4"),sQuery(id+"F0.wireOp",EDGE,"E11.82.5"),sQuery(id+"F0.wireOp",EDGE,"E11.82.6"),sQuery(id+"F0.wireOp",EDGE,"E11.83.0"),sQuery(id+"F0.wireOp",EDGE,"E11.83.1"),sQuery(id+"F0.wireOp",EDGE,"E11.83.2"),sQuery(id+"F0.wireOp",EDGE,"E11.83.3"),sQuery(id+"F0.wireOp",EDGE,"E11.83.4"),sQuery(id+"F0.wireOp",EDGE,"E11.83.5"),sQuery(id+"F0.wireOp",EDGE,"E11.83.6"),sQuery(id+"F0.wireOp",EDGE,"E11.84.0"),sQuery(id+"F0.wireOp",EDGE,"E11.84.1"),sQuery(id+"F0.wireOp",EDGE,"E11.84.2"),sQuery(id+"F0.wireOp",EDGE,"E11.84.3"),sQuery(id+"F0.wireOp",EDGE,"E11.84.4"),sQuery(id+"F0.wireOp",EDGE,"E11.84.5"),sQuery(id+"F0.wireOp",EDGE,"E11.84.6"),sQuery(id+"F0.wireOp",EDGE,"E11.85.0"),sQuery(id+"F0.wireOp",EDGE,"E11.85.1"),sQuery(id+"F0.wireOp",EDGE,"E11.85.2"),sQuery(id+"F0.wireOp",EDGE,"E11.85.3"),sQuery(id+"F0.wireOp",EDGE,"E11.85.4"),sQuery(id+"F0.wireOp",EDGE,"E11.85.5"),sQuery(id+"F0.wireOp",EDGE,"E11.85.6"),sQuery(id+"F0.wireOp",EDGE,"E11.86.0"),sQuery(id+"F0.wireOp",EDGE,"E11.86.1"),sQuery(id+"F0.wireOp",EDGE,"E11.86.2"),sQuery(id+"F0.wireOp",EDGE,"E11.86.3"),sQuery(id+"F0.wireOp",EDGE,"E11.86.4"),sQuery(id+"F0.wireOp",EDGE,"E11.86.5"),sQuery(id+"F0.wireOp",EDGE,"E11.86.6"),sQuery(id+"F0.wireOp",EDGE,"E11.87.0"),sQuery(id+"F0.wireOp",EDGE,"E11.87.1"),sQuery(id+"F0.wireOp",EDGE,"E11.87.2"),sQuery(id+"F0.wireOp",EDGE,"E11.87.3"),sQuery(id+"F0.wireOp",EDGE,"E11.87.4"),sQuery(id+"F0.wireOp",EDGE,"E11.87.5"),sQuery(id+"F0.wireOp",EDGE,"E11.87.6"),sQuery(id+"F0.wireOp",EDGE,"E11.88.0"),sQuery(id+"F0.wireOp",EDGE,"E11.88.1"),sQuery(id+"F0.wireOp",EDGE,"E11.88.2"),sQuery(id+"F0.wireOp",EDGE,"E11.88.3"),sQuery(id+"F0.wireOp",EDGE,"E11.88.4"),sQuery(id+"F0.wireOp",EDGE,"E11.88.5"),sQuery(id+"F0.wireOp",EDGE,"E11.88.6"),sQuery(id+"F0.wireOp",EDGE,"E11.89.0"),sQuery(id+"F0.wireOp",EDGE,"E11.89.1"),sQuery(id+"F0.wireOp",EDGE,"E11.89.2"),sQuery(id+"F0.wireOp",EDGE,"E11.89.3"),sQuery(id+"F0.wireOp",EDGE,"E11.89.4"),sQuery(id+"F0.wireOp",EDGE,"E11.89.5"),sQuery(id+"F0.wireOp",EDGE,"E11.89.6"),sQuery(id+"F0.wireOp",EDGE,"E11.90.0"),sQuery(id+"F0.wireOp",EDGE,"E11.90.1"),sQuery(id+"F0.wireOp",EDGE,"E11.90.2"),sQuery(id+"F0.wireOp",EDGE,"E11.90.3"),sQuery(id+"F0.wireOp",EDGE,"E11.90.4"),sQuery(id+"F0.wireOp",EDGE,"E11.90.5"),sQuery(id+"F0.wireOp",EDGE,"E11.90.6"),sQuery(id+"F0.wireOp",EDGE,"E11.91.0"),sQuery(id+"F0.wireOp",EDGE,"E11.91.1"),sQuery(id+"F0.wireOp",EDGE,"E11.91.2"),sQuery(id+"F0.wireOp",EDGE,"E11.91.3"),sQuery(id+"F0.wireOp",EDGE,"E11.91.4"),sQuery(id+"F0.wireOp",EDGE,"E11.91.5"),sQuery(id+"F0.wireOp",EDGE,"E11.91.6"),sQuery(id+"F0.wireOp",EDGE,"E11.92.0"),sQuery(id+"F0.wireOp",EDGE,"E11.92.1"),sQuery(id+"F0.wireOp",EDGE,"E11.92.2"),sQuery(id+"F0.wireOp",EDGE,"E11.92.3"),sQuery(id+"F0.wireOp",EDGE,"E11.92.4"),sQuery(id+"F0.wireOp",EDGE,"E11.92.5"),sQuery(id+"F0.wireOp",EDGE,"E11.92.6"),sQuery(id+"F0.wireOp",EDGE,"E11.93.0"),sQuery(id+"F0.wireOp",EDGE,"E11.93.1"),sQuery(id+"F0.wireOp",EDGE,"E11.93.2"),sQuery(id+"F0.wireOp",EDGE,"E11.93.3"),sQuery(id+"F0.wireOp",EDGE,"E11.93.4"),sQuery(id+"F0.wireOp",EDGE,"E11.93.5"),sQuery(id+"F0.wireOp",EDGE,"E11.93.6"),sQuery(id+"F0.wireOp",EDGE,"E11.94.0"),sQuery(id+"F0.wireOp",EDGE,"E11.94.1"),sQuery(id+"F0.wireOp",EDGE,"E11.94.2"),sQuery(id+"F0.wireOp",EDGE,"E11.94.3"),sQuery(id+"F0.wireOp",EDGE,"E11.94.4"),sQuery(id+"F0.wireOp",EDGE,"E11.94.5"),sQuery(id+"F0.wireOp",EDGE,"E11.94.6"),sQuery(id+"F0.wireOp",EDGE,"E11.95.0"),sQuery(id+"F0.wireOp",EDGE,"E11.95.1"),sQuery(id+"F0.wireOp",EDGE,"E11.95.2"),sQuery(id+"F0.wireOp",EDGE,"E11.95.3"),sQuery(id+"F0.wireOp",EDGE,"E11.95.4"),sQuery(id+"F0.wireOp",EDGE,"E11.95.5"),sQuery(id+"F0.wireOp",EDGE,"E11.95.6"),sQuery(id+"F0.wireOp",EDGE,"E11.96.0"),sQuery(id+"F0.wireOp",EDGE,"E11.96.1"),sQuery(id+"F0.wireOp",EDGE,"E11.96.2"),sQuery(id+"F0.wireOp",EDGE,"E11.96.3"),sQuery(id+"F0.wireOp",EDGE,"E11.96.4"),sQuery(id+"F0.wireOp",EDGE,"E11.96.5"),sQuery(id+"F0.wireOp",EDGE,"E11.96.6"),sQuery(id+"F0.wireOp",EDGE,"E11.97.0"),sQuery(id+"F0.wireOp",EDGE,"E11.97.1"),sQuery(id+"F0.wireOp",EDGE,"E11.97.2"),sQuery(id+"F0.wireOp",EDGE,"E11.97.3"),sQuery(id+"F0.wireOp",EDGE,"E11.97.4"),sQuery(id+"F0.wireOp",EDGE,"E11.97.5"),sQuery(id+"F0.wireOp",EDGE,"E11.97.6"),sQuery(id+"F0.wireOp",EDGE,"E11.98.0"),sQuery(id+"F0.wireOp",EDGE,"E11.98.1"),sQuery(id+"F0.wireOp",EDGE,"E11.98.2"),sQuery(id+"F0.wireOp",EDGE,"E11.98.3"),sQuery(id+"F0.wireOp",EDGE,"E11.98.4"),sQuery(id+"F0.wireOp",EDGE,"E11.98.5"),sQuery(id+"F0.wireOp",EDGE,"E11.98.6"),sQuery(id+"F0.wireOp",EDGE,"E11.99.0"),sQuery(id+"F0.wireOp",EDGE,"E11.99.1"),sQuery(id+"F0.wireOp",EDGE,"E11.99.2"),sQuery(id+"F0.wireOp",EDGE,"E11.99.3"),sQuery(id+"F0.wireOp",EDGE,"E11.99.4"),sQuery(id+"F0.wireOp",EDGE,"E11.99.5"),sQuery(id+"F0.wireOp",EDGE,"E11.99.6"),sQuery(id+"F0.wireOp",EDGE,"E18"),sQuery(id+"F0.wireOp",EDGE,"E19.trimOffspring"),sQuery(id+"F0.wireOp",EDGE,"E20.trimOffspring"),sQuery(id+"F0.wireOp",EDGE,"E21.trimOffspring"),sQuery(id+"F0.wireOp",EDGE,"E22.trimOffspring"),sQuery(id+"F0.wireOp",EDGE,"E23.trimOffspring"),sQuery(id+"F0.wireOp",EDGE,"E24.trimOffspring"),sQuery(id+"F0.wireOp",EDGE,"E25.trimOffspring"),sQuery(id+"F0.wireOp",EDGE,"E26.trimOffspring"),sQuery(id+"F0.wireOp",EDGE,"E27.trimOffspring"),sQuery(id+"F0.wireOp",EDGE,"E28.trimOffspring"),sQuery(id+"F0.wireOp",EDGE,"E29.trimOffspring"),sQuery(id+"F0.wireOp",EDGE,"E30.trimOffspring"),sQuery(id+"F0.wireOp",EDGE,"E31.trimOffspring"),sQuery(id+"F0.wireOp",EDGE,"E32.trimOffspring"),sQuery(id+"F0.wireOp",EDGE,"E33.trimOffspring"),sQuery(id+"F0.wireOp",EDGE,"E34.trimOffspring"),sQuery(id+"F0.wireOp",EDGE,"E35.trimOffspring"),sQuery(id+"F0.wireOp",EDGE,"E36.trimOffspring"),sQuery(id+"F0.wireOp",EDGE,"E37.trimOffspring"),sQuery(id+"F0.wireOp",EDGE,"E38.trimOffspring"),sQuery(id+"F0.wireOp",EDGE,"E39.trimOffspring"),sQuery(id+"F0.wireOp",EDGE,"E40.trimOffspring"),sQuery(id+"F0.wireOp",EDGE,"E41.trimOffspring"),sQuery(id+"F0.wireOp",EDGE,"E42.trimOffspring"),sQuery(id+"F0.wireOp",EDGE,"E43.trimOffspring"),sQuery(id+"F0.wireOp",EDGE,"E44.trimOffspring"),sQuery(id+"F0.wireOp",EDGE,"E45.trimOffspring"),sQuery(id+"F0.wireOp",EDGE,"E46.trimOffspring"),sQuery(id+"F0.wireOp",EDGE,"E47.trimOffspring"),sQuery(id+"F0.wireOp",EDGE,"E48.trimOffspring"),sQuery(id+"F0.wireOp",EDGE,"E49.trimOffspring"),sQuery(id+"F0.wireOp",EDGE,"E50.trimOffspring"),sQuery(id+"F0.wireOp",EDGE,"E51.trimOffspring"),sQuery(id+"F0.wireOp",EDGE,"E52.trimOffspring"),sQuery(id+"F0.wireOp",EDGE,"E53.trimOffspring"),sQuery(id+"F0.wireOp",EDGE,"E54.trimOffspring"),sQuery(id+"F0.wireOp",EDGE,"E55.trimOffspring"),sQuery(id+"F0.wireOp",EDGE,"E56.trimOffspring"),sQuery(id+"F0.wireOp",EDGE,"E57.trimOffspring"),sQuery(id+"F0.wireOp",EDGE,"E58.trimOffspring"),sQuery(id+"F0.wireOp",EDGE,"E59.trimOffspring"),sQuery(id+"F0.wireOp",EDGE,"E60.trimOffspring"),sQuery(id+"F0.wireOp",EDGE,"E61.trimOffspring"),sQuery(id+"F0.wireOp",EDGE,"E62.trimOffspring"),sQuery(id+"F0.wireOp",EDGE,"E63.trimOffspring"),sQuery(id+"F0.wireOp",EDGE,"E64.trimOffspring"),sQuery(id+"F0.wireOp",EDGE,"E65.trimOffspring"),sQuery(id+"F0.wireOp",EDGE,"E66.trimOffspring"),sQuery(id+"F0.wireOp",EDGE,"E67.trimOffspring"),sQuery(id+"F0.wireOp",EDGE,"E68.trimOffspring"),sQuery(id+"F0.wireOp",EDGE,"E69.trimOffspring"),sQuery(id+"F0.wireOp",EDGE,"E70.trimOffspring"),sQuery(id+"F0.wireOp",EDGE,"E71.trimOffspring"),sQuery(id+"F0.wireOp",EDGE,"E72.trimOffspring"),sQuery(id+"F0.wireOp",EDGE,"E73.trimOffspring"),sQuery(id+"F0.wireOp",EDGE,"E74.trimOffspring"),sQuery(id+"F0.wireOp",EDGE,"E75.trimOffspring"),sQuery(id+"F0.wireOp",EDGE,"E76.trimOffspring"),sQuery(id+"F0.wireOp",EDGE,"E77.trimOffspring"),sQuery(id+"F0.wireOp",EDGE,"E78.trimOffspring"),sQuery(id+"F0.wireOp",EDGE,"E79.trimOffspring"),sQuery(id+"F0.wireOp",EDGE,"E80.trimOffspring"),sQuery(id+"F0.wireOp",EDGE,"E81.trimOffspring"),sQuery(id+"F0.wireOp",EDGE,"E82.trimOffspring"),sQuery(id+"F0.wireOp",EDGE,"E83.trimOffspring"),sQuery(id+"F0.wireOp",EDGE,"E84.trimOffspring"),sQuery(id+"F0.wireOp",EDGE,"E85.trimOffspring"),sQuery(id+"F0.wireOp",EDGE,"E86.trimOffspring"),sQuery(id+"F0.wireOp",EDGE,"E87.trimOffspring"),sQuery(id+"F0.wireOp",EDGE,"E88.trimOffspring"),sQuery(id+"F0.wireOp",EDGE,"E89.trimOffspring"),sQuery(id+"F0.wireOp",EDGE,"E90.trimOffspring"),sQuery(id+"F0.wireOp",EDGE,"E91.trimOffspring"),sQuery(id+"F0.wireOp",EDGE,"E92.trimOffspring"),sQuery(id+"F0.wireOp",EDGE,"E93.trimOffspring"),sQuery(id+"F0.wireOp",EDGE,"E94.trimOffspring"),sQuery(id+"F0.wireOp",EDGE,"E95.trimOffspring"),sQuery(id+"F0.wireOp",EDGE,"E96.trimOffspring"),sQuery(id+"F0.wireOp",EDGE,"E97.trimOffspring"),sQuery(id+"F0.wireOp",EDGE,"E98.trimOffspring"),sQuery(id+"F0.wireOp",EDGE,"E99.trimOffspring"),sQuery(id+"F0.wireOp",EDGE,"E100.trimOffspring"),sQuery(id+"F0.wireOp",EDGE,"E101.trimOffspring"),sQuery(id+"F0.wireOp",EDGE,"E102.trimOffspring"),sQuery(id+"F0.wireOp",EDGE,"E103.trimOffspring"),sQuery(id+"F0.wireOp",EDGE,"E104.trimOffspring"),sQuery(id+"F0.wireOp",EDGE,"E105.trimOffspring"),sQuery(id+"F0.wireOp",EDGE,"E106.trimOffspring"),sQuery(id+"F0.wireOp",EDGE,"E107.trimOffspring"),sQuery(id+"F0.wireOp",EDGE,"E108.trimOffspring"),sQuery(id+"F0.wireOp",EDGE,"E109.trimOffspring"),sQuery(id+"F0.wireOp",EDGE,"E110.trimOffspring"),sQuery(id+"F0.wireOp",EDGE,"E111.trimOffspring"),sQuery(id+"F0.wireOp",EDGE,"E112.trimOffspring"),sQuery(id+"F0.wireOp",EDGE,"E113.trimOffspring"),sQuery(id+"F0.wireOp",EDGE,"E114.trimOffspring"),sQuery(id+"F0.wireOp",EDGE,"E115.trimOffspring"),sQuery(id+"F0.wireOp",EDGE,"E116.trimOffspring"),sQuery(id+"F0.wireOp",EDGE,"E117.trimOffspring")])],"isStart":true}),makeQuery(id+"F4.opExtrude","SWEPT_FACE",FACE,{"disambiguationData":[OSD([sQuery(id+"F3.wireOp",EDGE,"E118")])]})]});
            circularPattern(context, id + "F10", {"operationType" : NewBodyOperationType.ADD, "entities" : qUnion([Q0]), "axis" : qUnion([Q1]), "angle" : 360 * degree, "instanceCount" : 8, "equalSpace" : true, "computeTransformsWithoutBuiltin" : true});
        }
        {
            var Q0;
            Q0=makeQuery(id+"F6.boolean.opBoolean","INTERSECT",EDGE,{"derivedFrom":[makeQuery(id+"F1.opExtrude","SWEPT_FACE",FACE,{"disambiguationData":[OSD([sQuery(id+"F0.wireOp",EDGE,"E11.85.1")])]}),makeQuery(id+"F6.opExtrude","CAP_FACE",FACE,{"disambiguationData":[OSD([sQuery(id+"F5.wireOp",EDGE,"E119"),sQuery(id+"F5.wireOp",EDGE,"E120")])],"isStart":false})]});
            var Q1;
            Q1=makeQuery(id+"F6.boolean.opBoolean","INTERSECT",EDGE,{"derivedFrom":[makeQuery(id+"F1.opExtrude","SWEPT_FACE",FACE,{"disambiguationData":[OSD([sQuery(id+"F0.wireOp",EDGE,"E11.84.0")])]}),makeQuery(id+"F6.opExtrude","CAP_FACE",FACE,{"disambiguationData":[OSD([sQuery(id+"F5.wireOp",EDGE,"E119"),sQuery(id+"F5.wireOp",EDGE,"E120")])],"isStart":false})]});
            var Q2;
            Q2=makeQuery(id+"F6.boolean.opBoolean","INTERSECT",EDGE,{"derivedFrom":[makeQuery(id+"F1.opExtrude","SWEPT_FACE",FACE,{"disambiguationData":[OSD([sQuery(id+"F0.wireOp",EDGE,"E11.83.0")])]}),makeQuery(id+"F6.opExtrude","CAP_FACE",FACE,{"disambiguationData":[OSD([sQuery(id+"F5.wireOp",EDGE,"E119"),sQuery(id+"F5.wireOp",EDGE,"E120")])],"isStart":false})]});
            var Q3;
            Q3=makeQuery(id+"F6.boolean.opBoolean","INTERSECT",EDGE,{"derivedFrom":[makeQuery(id+"F1.opExtrude","SWEPT_FACE",FACE,{"disambiguationData":[OSD([sQuery(id+"F0.wireOp",EDGE,"E11.82.0")])]}),makeQuery(id+"F6.opExtrude","CAP_FACE",FACE,{"disambiguationData":[OSD([sQuery(id+"F5.wireOp",EDGE,"E119"),sQuery(id+"F5.wireOp",EDGE,"E120")])],"isStart":false})]});
            var Q4;
            Q4=makeQuery(id+"F6.boolean.opBoolean","INTERSECT",EDGE,{"derivedFrom":[makeQuery(id+"F1.opExtrude","SWEPT_FACE",FACE,{"disambiguationData":[OSD([sQuery(id+"F0.wireOp",EDGE,"E11.86.0")])]}),makeQuery(id+"F6.opExtrude","CAP_FACE",FACE,{"disambiguationData":[OSD([sQuery(id+"F5.wireOp",EDGE,"E119"),sQuery(id+"F5.wireOp",EDGE,"E120")])],"isStart":false})]});
            var Q5;
            Q5=makeQuery(id+"F6.boolean.opBoolean","INTERSECT",EDGE,{"derivedFrom":[makeQuery(id+"F1.opExtrude","SWEPT_FACE",FACE,{"disambiguationData":[OSD([sQuery(id+"F0.wireOp",EDGE,"E11.87.0")])]}),makeQuery(id+"F6.opExtrude","CAP_FACE",FACE,{"disambiguationData":[OSD([sQuery(id+"F5.wireOp",EDGE,"E119"),sQuery(id+"F5.wireOp",EDGE,"E120")])],"isStart":false})]});
            var Q6;
            Q6=makeQuery(id+"F6.boolean.opBoolean","INTERSECT",EDGE,{"derivedFrom":[makeQuery(id+"F1.opExtrude","SWEPT_FACE",FACE,{"disambiguationData":[OSD([sQuery(id+"F0.wireOp",EDGE,"E11.88.0")])]}),makeQuery(id+"F6.opExtrude","CAP_FACE",FACE,{"disambiguationData":[OSD([sQuery(id+"F5.wireOp",EDGE,"E119"),sQuery(id+"F5.wireOp",EDGE,"E120")])],"isStart":false})]});
            var Q7;
            Q7=makeQuery(id+"F6.boolean.opBoolean","INTERSECT",EDGE,{"derivedFrom":[makeQuery(id+"F1.opExtrude","SWEPT_FACE",FACE,{"disambiguationData":[OSD([sQuery(id+"F0.wireOp",EDGE,"E11.89.0")])]}),makeQuery(id+"F6.opExtrude","CAP_FACE",FACE,{"disambiguationData":[OSD([sQuery(id+"F5.wireOp",EDGE,"E119"),sQuery(id+"F5.wireOp",EDGE,"E120")])],"isStart":false})]});
            var Q8;
            Q8=makeQuery(id+"F6.boolean.opBoolean","INTERSECT",EDGE,{"derivedFrom":[makeQuery(id+"F1.opExtrude","SWEPT_FACE",FACE,{"disambiguationData":[OSD([sQuery(id+"F0.wireOp",EDGE,"E11.90.0")])]}),makeQuery(id+"F6.opExtrude","CAP_FACE",FACE,{"disambiguationData":[OSD([sQuery(id+"F5.wireOp",EDGE,"E119"),sQuery(id+"F5.wireOp",EDGE,"E120")])],"isStart":false})]});
            var Q9;
            Q9=makeQuery(id+"F6.boolean.opBoolean","INTERSECT",EDGE,{"derivedFrom":[makeQuery(id+"F1.opExtrude","SWEPT_FACE",FACE,{"disambiguationData":[OSD([sQuery(id+"F0.wireOp",EDGE,"E11.91.0")])]}),makeQuery(id+"F6.opExtrude","CAP_FACE",FACE,{"disambiguationData":[OSD([sQuery(id+"F5.wireOp",EDGE,"E119"),sQuery(id+"F5.wireOp",EDGE,"E120")])],"isStart":false})]});
            var Q10;
            Q10=makeQuery(id+"F6.boolean.opBoolean","INTERSECT",EDGE,{"derivedFrom":[makeQuery(id+"F1.opExtrude","SWEPT_FACE",FACE,{"disambiguationData":[OSD([sQuery(id+"F0.wireOp",EDGE,"E11.92.0")])]}),makeQuery(id+"F6.opExtrude","CAP_FACE",FACE,{"disambiguationData":[OSD([sQuery(id+"F5.wireOp",EDGE,"E119"),sQuery(id+"F5.wireOp",EDGE,"E120")])],"isStart":false})]});
            var Q11;
            Q11=makeQuery(id+"F6.boolean.opBoolean","INTERSECT",EDGE,{"derivedFrom":[makeQuery(id+"F1.opExtrude","SWEPT_FACE",FACE,{"disambiguationData":[OSD([sQuery(id+"F0.wireOp",EDGE,"E11.93.0")])]}),makeQuery(id+"F6.opExtrude","CAP_FACE",FACE,{"disambiguationData":[OSD([sQuery(id+"F5.wireOp",EDGE,"E119"),sQuery(id+"F5.wireOp",EDGE,"E120")])],"isStart":false})]});
            var Q12;
            Q12=makeQuery(id+"F6.boolean.opBoolean","INTERSECT",EDGE,{"derivedFrom":[makeQuery(id+"F1.opExtrude","SWEPT_FACE",FACE,{"disambiguationData":[OSD([sQuery(id+"F0.wireOp",EDGE,"E11.94.0")])]}),makeQuery(id+"F6.opExtrude","CAP_FACE",FACE,{"disambiguationData":[OSD([sQuery(id+"F5.wireOp",EDGE,"E119"),sQuery(id+"F5.wireOp",EDGE,"E120")])],"isStart":false})]});
            var Q13;
            Q13=makeQuery(id+"F6.boolean.opBoolean","INTERSECT",EDGE,{"derivedFrom":[makeQuery(id+"F1.opExtrude","SWEPT_FACE",FACE,{"disambiguationData":[OSD([sQuery(id+"F0.wireOp",EDGE,"E11.95.0")])]}),makeQuery(id+"F6.opExtrude","CAP_FACE",FACE,{"disambiguationData":[OSD([sQuery(id+"F5.wireOp",EDGE,"E119"),sQuery(id+"F5.wireOp",EDGE,"E120")])],"isStart":false})]});
            var Q14;
            Q14=makeQuery(id+"F6.boolean.opBoolean","INTERSECT",EDGE,{"derivedFrom":[makeQuery(id+"F1.opExtrude","SWEPT_FACE",FACE,{"disambiguationData":[OSD([sQuery(id+"F0.wireOp",EDGE,"E11.96.0")])]}),makeQuery(id+"F6.opExtrude","CAP_FACE",FACE,{"disambiguationData":[OSD([sQuery(id+"F5.wireOp",EDGE,"E119"),sQuery(id+"F5.wireOp",EDGE,"E120")])],"isStart":false})]});
            var Q15;
            Q15=makeQuery(id+"F6.boolean.opBoolean","INTERSECT",EDGE,{"derivedFrom":[makeQuery(id+"F1.opExtrude","SWEPT_FACE",FACE,{"disambiguationData":[OSD([sQuery(id+"F0.wireOp",EDGE,"E11.97.0")])]}),makeQuery(id+"F6.opExtrude","CAP_FACE",FACE,{"disambiguationData":[OSD([sQuery(id+"F5.wireOp",EDGE,"E119"),sQuery(id+"F5.wireOp",EDGE,"E120")])],"isStart":false})]});
            var Q16;
            Q16=makeQuery(id+"F6.boolean.opBoolean","INTERSECT",EDGE,{"derivedFrom":[makeQuery(id+"F1.opExtrude","SWEPT_FACE",FACE,{"disambiguationData":[OSD([sQuery(id+"F0.wireOp",EDGE,"E11.98.0")])]}),makeQuery(id+"F6.opExtrude","CAP_FACE",FACE,{"disambiguationData":[OSD([sQuery(id+"F5.wireOp",EDGE,"E119"),sQuery(id+"F5.wireOp",EDGE,"E120")])],"isStart":false})]});
            var Q17;
            Q17=makeQuery(id+"F6.boolean.opBoolean","INTERSECT",EDGE,{"derivedFrom":[makeQuery(id+"F1.opExtrude","SWEPT_FACE",FACE,{"disambiguationData":[OSD([sQuery(id+"F0.wireOp",EDGE,"E11.99.0")])]}),makeQuery(id+"F6.opExtrude","CAP_FACE",FACE,{"disambiguationData":[OSD([sQuery(id+"F5.wireOp",EDGE,"E119"),sQuery(id+"F5.wireOp",EDGE,"E120")])],"isStart":false})]});
            var Q18;
            {var subQ0=sQuery(id+"F5.wireOp",EDGE,"E119");Q18=makeQuery(id+"FZDd3dyAwVUtAiM_1.opFillet","BLEND_EDGE",EDGE,{"blendedFrom":[makeQuery(id+"F9.opExtrude","CAP_EDGE",EDGE,{"disambiguationData":[OSD([sQuery(id+"F8.wireOp",EDGE,"E121.0.1")])],"isStart":true}),makeQuery(id+"F6.boolean.opBoolean","COPY",FACE,{"disambiguationData":[TD([makeQuery(id+"F1.opExtrude","SWEPT_FACE",FACE,{"disambiguationData":[OSD([sQuery(id+"F0.wireOp",EDGE,"E4")])]})])],"derivedFrom":makeQuery(id+"F6.opExtrude","CAP_FACE",FACE,{"disambiguationData":[OSD([subQ0,sQuery(id+"F5.wireOp",EDGE,"E120")])],"isStart":false})})],"blendedInto":[makeQuery(id+"F6.boolean.opBoolean","COPY",FACE,{"disambiguationData":[TD([makeQuery(id+"F1.opExtrude","SWEPT_FACE",FACE,{"disambiguationData":[OSD([sQuery(id+"F0.wireOp",EDGE,"E4")])]})])],"derivedFrom":makeQuery(id+"F6.opExtrude","CAP_FACE",FACE,{"disambiguationData":[OSD([subQ0,sQuery(id+"F5.wireOp",EDGE,"E120")])],"isStart":false})})]});}
            var Q19;
            Q19=makeQuery(id+"F6.boolean.opBoolean","INTERSECT",EDGE,{"derivedFrom":[makeQuery(id+"F1.opExtrude","SWEPT_FACE",FACE,{"disambiguationData":[OSD([sQuery(id+"F0.wireOp",EDGE,"E11.1.0")])]}),makeQuery(id+"F6.opExtrude","CAP_FACE",FACE,{"disambiguationData":[OSD([sQuery(id+"F5.wireOp",EDGE,"E119"),sQuery(id+"F5.wireOp",EDGE,"E120")])],"isStart":false})]});
            var Q20;
            Q20=makeQuery(id+"F6.boolean.opBoolean","INTERSECT",EDGE,{"derivedFrom":[makeQuery(id+"F1.opExtrude","SWEPT_FACE",FACE,{"disambiguationData":[OSD([sQuery(id+"F0.wireOp",EDGE,"E11.2.0")])]}),makeQuery(id+"F6.opExtrude","CAP_FACE",FACE,{"disambiguationData":[OSD([sQuery(id+"F5.wireOp",EDGE,"E119"),sQuery(id+"F5.wireOp",EDGE,"E120")])],"isStart":false})]});
            var Q21;
            Q21=makeQuery(id+"F6.boolean.opBoolean","INTERSECT",EDGE,{"derivedFrom":[makeQuery(id+"F1.opExtrude","SWEPT_FACE",FACE,{"disambiguationData":[OSD([sQuery(id+"F0.wireOp",EDGE,"E11.3.0")])]}),makeQuery(id+"F6.opExtrude","CAP_FACE",FACE,{"disambiguationData":[OSD([sQuery(id+"F5.wireOp",EDGE,"E119"),sQuery(id+"F5.wireOp",EDGE,"E120")])],"isStart":false})]});
            var Q22;
            Q22=makeQuery(id+"F6.boolean.opBoolean","INTERSECT",EDGE,{"derivedFrom":[makeQuery(id+"F1.opExtrude","SWEPT_FACE",FACE,{"disambiguationData":[OSD([sQuery(id+"F0.wireOp",EDGE,"E11.4.0")])]}),makeQuery(id+"F6.opExtrude","CAP_FACE",FACE,{"disambiguationData":[OSD([sQuery(id+"F5.wireOp",EDGE,"E119"),sQuery(id+"F5.wireOp",EDGE,"E120")])],"isStart":false})]});
            var Q23;
            Q23=makeQuery(id+"F6.boolean.opBoolean","INTERSECT",EDGE,{"derivedFrom":[makeQuery(id+"F1.opExtrude","SWEPT_FACE",FACE,{"disambiguationData":[OSD([sQuery(id+"F0.wireOp",EDGE,"E11.5.0")])]}),makeQuery(id+"F6.opExtrude","CAP_FACE",FACE,{"disambiguationData":[OSD([sQuery(id+"F5.wireOp",EDGE,"E119"),sQuery(id+"F5.wireOp",EDGE,"E120")])],"isStart":false})]});
            var Q24;
            Q24=makeQuery(id+"F6.boolean.opBoolean","INTERSECT",EDGE,{"derivedFrom":[makeQuery(id+"F1.opExtrude","SWEPT_FACE",FACE,{"disambiguationData":[OSD([sQuery(id+"F0.wireOp",EDGE,"E11.6.0")])]}),makeQuery(id+"F6.opExtrude","CAP_FACE",FACE,{"disambiguationData":[OSD([sQuery(id+"F5.wireOp",EDGE,"E119"),sQuery(id+"F5.wireOp",EDGE,"E120")])],"isStart":false})]});
            var Q25;
            Q25=makeQuery(id+"F6.boolean.opBoolean","INTERSECT",EDGE,{"derivedFrom":[makeQuery(id+"F1.opExtrude","SWEPT_FACE",FACE,{"disambiguationData":[OSD([sQuery(id+"F0.wireOp",EDGE,"E11.7.0")])]}),makeQuery(id+"F6.opExtrude","CAP_FACE",FACE,{"disambiguationData":[OSD([sQuery(id+"F5.wireOp",EDGE,"E119"),sQuery(id+"F5.wireOp",EDGE,"E120")])],"isStart":false})]});
            var Q26;
            Q26=makeQuery(id+"F6.boolean.opBoolean","INTERSECT",EDGE,{"derivedFrom":[makeQuery(id+"F1.opExtrude","SWEPT_FACE",FACE,{"disambiguationData":[OSD([sQuery(id+"F0.wireOp",EDGE,"E11.8.0")])]}),makeQuery(id+"F6.opExtrude","CAP_FACE",FACE,{"disambiguationData":[OSD([sQuery(id+"F5.wireOp",EDGE,"E119"),sQuery(id+"F5.wireOp",EDGE,"E120")])],"isStart":false})]});
            var Q27;
            Q27=makeQuery(id+"F6.boolean.opBoolean","INTERSECT",EDGE,{"derivedFrom":[makeQuery(id+"F1.opExtrude","SWEPT_FACE",FACE,{"disambiguationData":[OSD([sQuery(id+"F0.wireOp",EDGE,"E11.9.0")])]}),makeQuery(id+"F6.opExtrude","CAP_FACE",FACE,{"disambiguationData":[OSD([sQuery(id+"F5.wireOp",EDGE,"E119"),sQuery(id+"F5.wireOp",EDGE,"E120")])],"isStart":false})]});
            var Q28;
            Q28=makeQuery(id+"F6.boolean.opBoolean","INTERSECT",EDGE,{"derivedFrom":[makeQuery(id+"F1.opExtrude","SWEPT_FACE",FACE,{"disambiguationData":[OSD([sQuery(id+"F0.wireOp",EDGE,"E11.10.0")])]}),makeQuery(id+"F6.opExtrude","CAP_FACE",FACE,{"disambiguationData":[OSD([sQuery(id+"F5.wireOp",EDGE,"E119"),sQuery(id+"F5.wireOp",EDGE,"E120")])],"isStart":false})]});
            var Q29;
            Q29=makeQuery(id+"F6.boolean.opBoolean","INTERSECT",EDGE,{"derivedFrom":[makeQuery(id+"F1.opExtrude","SWEPT_FACE",FACE,{"disambiguationData":[OSD([sQuery(id+"F0.wireOp",EDGE,"E11.11.0")])]}),makeQuery(id+"F6.opExtrude","CAP_FACE",FACE,{"disambiguationData":[OSD([sQuery(id+"F5.wireOp",EDGE,"E119"),sQuery(id+"F5.wireOp",EDGE,"E120")])],"isStart":false})]});
            var Q30;
            Q30=makeQuery(id+"F6.boolean.opBoolean","INTERSECT",EDGE,{"derivedFrom":[makeQuery(id+"F1.opExtrude","SWEPT_FACE",FACE,{"disambiguationData":[OSD([sQuery(id+"F0.wireOp",EDGE,"E11.12.0")])]}),makeQuery(id+"F6.opExtrude","CAP_FACE",FACE,{"disambiguationData":[OSD([sQuery(id+"F5.wireOp",EDGE,"E119"),sQuery(id+"F5.wireOp",EDGE,"E120")])],"isStart":false})]});
            var Q31;
            Q31=makeQuery(id+"F6.boolean.opBoolean","INTERSECT",EDGE,{"derivedFrom":[makeQuery(id+"F1.opExtrude","SWEPT_FACE",FACE,{"disambiguationData":[OSD([sQuery(id+"F0.wireOp",EDGE,"E11.13.0")])]}),makeQuery(id+"F6.opExtrude","CAP_FACE",FACE,{"disambiguationData":[OSD([sQuery(id+"F5.wireOp",EDGE,"E119"),sQuery(id+"F5.wireOp",EDGE,"E120")])],"isStart":false})]});
            var Q32;
            Q32=makeQuery(id+"F6.boolean.opBoolean","INTERSECT",EDGE,{"derivedFrom":[makeQuery(id+"F1.opExtrude","SWEPT_FACE",FACE,{"disambiguationData":[OSD([sQuery(id+"F0.wireOp",EDGE,"E11.14.0")])]}),makeQuery(id+"F6.opExtrude","CAP_FACE",FACE,{"disambiguationData":[OSD([sQuery(id+"F5.wireOp",EDGE,"E119"),sQuery(id+"F5.wireOp",EDGE,"E120")])],"isStart":false})]});
            var Q33;
            Q33=makeQuery(id+"F6.boolean.opBoolean","INTERSECT",EDGE,{"derivedFrom":[makeQuery(id+"F1.opExtrude","SWEPT_FACE",FACE,{"disambiguationData":[OSD([sQuery(id+"F0.wireOp",EDGE,"E11.15.0")])]}),makeQuery(id+"F6.opExtrude","CAP_FACE",FACE,{"disambiguationData":[OSD([sQuery(id+"F5.wireOp",EDGE,"E119"),sQuery(id+"F5.wireOp",EDGE,"E120")])],"isStart":false})]});
            var Q34;
            Q34=makeQuery(id+"F6.boolean.opBoolean","INTERSECT",EDGE,{"derivedFrom":[makeQuery(id+"F1.opExtrude","SWEPT_FACE",FACE,{"disambiguationData":[OSD([sQuery(id+"F0.wireOp",EDGE,"E11.16.0")])]}),makeQuery(id+"F6.opExtrude","CAP_FACE",FACE,{"disambiguationData":[OSD([sQuery(id+"F5.wireOp",EDGE,"E119"),sQuery(id+"F5.wireOp",EDGE,"E120")])],"isStart":false})]});
            var Q35;
            Q35=makeQuery(id+"F6.boolean.opBoolean","INTERSECT",EDGE,{"derivedFrom":[makeQuery(id+"F1.opExtrude","SWEPT_FACE",FACE,{"disambiguationData":[OSD([sQuery(id+"F0.wireOp",EDGE,"E11.17.0")])]}),makeQuery(id+"F6.opExtrude","CAP_FACE",FACE,{"disambiguationData":[OSD([sQuery(id+"F5.wireOp",EDGE,"E119"),sQuery(id+"F5.wireOp",EDGE,"E120")])],"isStart":false})]});
            var Q36;
            Q36=makeQuery(id+"F6.boolean.opBoolean","INTERSECT",EDGE,{"derivedFrom":[makeQuery(id+"F1.opExtrude","SWEPT_FACE",FACE,{"disambiguationData":[OSD([sQuery(id+"F0.wireOp",EDGE,"E11.18.0")])]}),makeQuery(id+"F6.opExtrude","CAP_FACE",FACE,{"disambiguationData":[OSD([sQuery(id+"F5.wireOp",EDGE,"E119"),sQuery(id+"F5.wireOp",EDGE,"E120")])],"isStart":false})]});
            var Q37;
            Q37=makeQuery(id+"F6.boolean.opBoolean","INTERSECT",EDGE,{"derivedFrom":[makeQuery(id+"F1.opExtrude","SWEPT_FACE",FACE,{"disambiguationData":[OSD([sQuery(id+"F0.wireOp",EDGE,"E11.19.0")])]}),makeQuery(id+"F6.opExtrude","CAP_FACE",FACE,{"disambiguationData":[OSD([sQuery(id+"F5.wireOp",EDGE,"E119"),sQuery(id+"F5.wireOp",EDGE,"E120")])],"isStart":false})]});
            var Q38;
            Q38=makeQuery(id+"F6.boolean.opBoolean","INTERSECT",EDGE,{"derivedFrom":[makeQuery(id+"F1.opExtrude","SWEPT_FACE",FACE,{"disambiguationData":[OSD([sQuery(id+"F0.wireOp",EDGE,"E11.20.0")])]}),makeQuery(id+"F6.opExtrude","CAP_FACE",FACE,{"disambiguationData":[OSD([sQuery(id+"F5.wireOp",EDGE,"E119"),sQuery(id+"F5.wireOp",EDGE,"E120")])],"isStart":false})]});
            var Q39;
            Q39=makeQuery(id+"F6.boolean.opBoolean","INTERSECT",EDGE,{"derivedFrom":[makeQuery(id+"F1.opExtrude","SWEPT_FACE",FACE,{"disambiguationData":[OSD([sQuery(id+"F0.wireOp",EDGE,"E11.21.0")])]}),makeQuery(id+"F6.opExtrude","CAP_FACE",FACE,{"disambiguationData":[OSD([sQuery(id+"F5.wireOp",EDGE,"E119"),sQuery(id+"F5.wireOp",EDGE,"E120")])],"isStart":false})]});
            var Q40;
            Q40=makeQuery(id+"F6.boolean.opBoolean","INTERSECT",EDGE,{"derivedFrom":[makeQuery(id+"F1.opExtrude","SWEPT_FACE",FACE,{"disambiguationData":[OSD([sQuery(id+"F0.wireOp",EDGE,"E11.22.0")])]}),makeQuery(id+"F6.opExtrude","CAP_FACE",FACE,{"disambiguationData":[OSD([sQuery(id+"F5.wireOp",EDGE,"E119"),sQuery(id+"F5.wireOp",EDGE,"E120")])],"isStart":false})]});
            var Q41;
            Q41=makeQuery(id+"F6.boolean.opBoolean","INTERSECT",EDGE,{"derivedFrom":[makeQuery(id+"F1.opExtrude","SWEPT_FACE",FACE,{"disambiguationData":[OSD([sQuery(id+"F0.wireOp",EDGE,"E11.23.0")])]}),makeQuery(id+"F6.opExtrude","CAP_FACE",FACE,{"disambiguationData":[OSD([sQuery(id+"F5.wireOp",EDGE,"E119"),sQuery(id+"F5.wireOp",EDGE,"E120")])],"isStart":false})]});
            var Q42;
            Q42=makeQuery(id+"F6.boolean.opBoolean","INTERSECT",EDGE,{"derivedFrom":[makeQuery(id+"F1.opExtrude","SWEPT_FACE",FACE,{"disambiguationData":[OSD([sQuery(id+"F0.wireOp",EDGE,"E11.24.0")])]}),makeQuery(id+"F6.opExtrude","CAP_FACE",FACE,{"disambiguationData":[OSD([sQuery(id+"F5.wireOp",EDGE,"E119"),sQuery(id+"F5.wireOp",EDGE,"E120")])],"isStart":false})]});
            var Q43;
            Q43=makeQuery(id+"F6.boolean.opBoolean","INTERSECT",EDGE,{"derivedFrom":[makeQuery(id+"F1.opExtrude","SWEPT_FACE",FACE,{"disambiguationData":[OSD([sQuery(id+"F0.wireOp",EDGE,"E11.26.0")])]}),makeQuery(id+"F6.opExtrude","CAP_FACE",FACE,{"disambiguationData":[OSD([sQuery(id+"F5.wireOp",EDGE,"E119"),sQuery(id+"F5.wireOp",EDGE,"E120")])],"isStart":false})]});
            var Q44;
            Q44=makeQuery(id+"F6.boolean.opBoolean","INTERSECT",EDGE,{"derivedFrom":[makeQuery(id+"F1.opExtrude","SWEPT_FACE",FACE,{"disambiguationData":[OSD([sQuery(id+"F0.wireOp",EDGE,"E11.27.0")])]}),makeQuery(id+"F6.opExtrude","CAP_FACE",FACE,{"disambiguationData":[OSD([sQuery(id+"F5.wireOp",EDGE,"E119"),sQuery(id+"F5.wireOp",EDGE,"E120")])],"isStart":false})]});
            var Q45;
            {var subQ0=sQuery(id+"F5.wireOp",EDGE,"E119");Q45=makeQuery(id+"FZDd3dyAwVUtAiM_1.opFillet","BLEND_EDGE",EDGE,{"blendedFrom":[makeQuery(id+"F10.opPattern","COPY",EDGE,{"derivedFrom":makeQuery(id+"F9.opExtrude","CAP_EDGE",EDGE,{"disambiguationData":[OSD([sQuery(id+"F8.wireOp",EDGE,"E121.0.1")])],"isStart":true}),"instanceName":"1"}),makeQuery(id+"F6.boolean.opBoolean","COPY",FACE,{"disambiguationData":[TD([makeQuery(id+"F1.opExtrude","SWEPT_FACE",FACE,{"disambiguationData":[OSD([sQuery(id+"F0.wireOp",EDGE,"E11.25.0")])]})])],"derivedFrom":makeQuery(id+"F6.opExtrude","CAP_FACE",FACE,{"disambiguationData":[OSD([subQ0,sQuery(id+"F5.wireOp",EDGE,"E120")])],"isStart":false})})],"blendedInto":[makeQuery(id+"F6.boolean.opBoolean","COPY",FACE,{"disambiguationData":[TD([makeQuery(id+"F1.opExtrude","SWEPT_FACE",FACE,{"disambiguationData":[OSD([sQuery(id+"F0.wireOp",EDGE,"E11.25.0")])]})])],"derivedFrom":makeQuery(id+"F6.opExtrude","CAP_FACE",FACE,{"disambiguationData":[OSD([subQ0,sQuery(id+"F5.wireOp",EDGE,"E120")])],"isStart":false})})]});}
            var Q46;
            Q46=makeQuery(id+"F6.boolean.opBoolean","INTERSECT",EDGE,{"derivedFrom":[makeQuery(id+"F1.opExtrude","SWEPT_FACE",FACE,{"disambiguationData":[OSD([sQuery(id+"F0.wireOp",EDGE,"E11.28.0")])]}),makeQuery(id+"F6.opExtrude","CAP_FACE",FACE,{"disambiguationData":[OSD([sQuery(id+"F5.wireOp",EDGE,"E119"),sQuery(id+"F5.wireOp",EDGE,"E120")])],"isStart":false})]});
            var Q47;
            Q47=makeQuery(id+"F6.boolean.opBoolean","INTERSECT",EDGE,{"derivedFrom":[makeQuery(id+"F1.opExtrude","SWEPT_FACE",FACE,{"disambiguationData":[OSD([sQuery(id+"F0.wireOp",EDGE,"E11.29.0")])]}),makeQuery(id+"F6.opExtrude","CAP_FACE",FACE,{"disambiguationData":[OSD([sQuery(id+"F5.wireOp",EDGE,"E119"),sQuery(id+"F5.wireOp",EDGE,"E120")])],"isStart":false})]});
            var Q48;
            Q48=makeQuery(id+"F6.boolean.opBoolean","INTERSECT",EDGE,{"derivedFrom":[makeQuery(id+"F1.opExtrude","SWEPT_FACE",FACE,{"disambiguationData":[OSD([sQuery(id+"F0.wireOp",EDGE,"E11.30.0")])]}),makeQuery(id+"F6.opExtrude","CAP_FACE",FACE,{"disambiguationData":[OSD([sQuery(id+"F5.wireOp",EDGE,"E119"),sQuery(id+"F5.wireOp",EDGE,"E120")])],"isStart":false})]});
            var Q49;
            Q49=makeQuery(id+"F6.boolean.opBoolean","INTERSECT",EDGE,{"derivedFrom":[makeQuery(id+"F1.opExtrude","SWEPT_FACE",FACE,{"disambiguationData":[OSD([sQuery(id+"F0.wireOp",EDGE,"E11.31.0")])]}),makeQuery(id+"F6.opExtrude","CAP_FACE",FACE,{"disambiguationData":[OSD([sQuery(id+"F5.wireOp",EDGE,"E119"),sQuery(id+"F5.wireOp",EDGE,"E120")])],"isStart":false})]});
            var Q50;
            Q50=makeQuery(id+"F6.boolean.opBoolean","INTERSECT",EDGE,{"derivedFrom":[makeQuery(id+"F1.opExtrude","SWEPT_FACE",FACE,{"disambiguationData":[OSD([sQuery(id+"F0.wireOp",EDGE,"E11.32.0")])]}),makeQuery(id+"F6.opExtrude","CAP_FACE",FACE,{"disambiguationData":[OSD([sQuery(id+"F5.wireOp",EDGE,"E119"),sQuery(id+"F5.wireOp",EDGE,"E120")])],"isStart":false})]});
            var Q51;
            Q51=makeQuery(id+"F6.boolean.opBoolean","INTERSECT",EDGE,{"derivedFrom":[makeQuery(id+"F1.opExtrude","SWEPT_FACE",FACE,{"disambiguationData":[OSD([sQuery(id+"F0.wireOp",EDGE,"E11.33.0")])]}),makeQuery(id+"F6.opExtrude","CAP_FACE",FACE,{"disambiguationData":[OSD([sQuery(id+"F5.wireOp",EDGE,"E119"),sQuery(id+"F5.wireOp",EDGE,"E120")])],"isStart":false})]});
            var Q52;
            Q52=makeQuery(id+"F6.boolean.opBoolean","INTERSECT",EDGE,{"derivedFrom":[makeQuery(id+"F1.opExtrude","SWEPT_FACE",FACE,{"disambiguationData":[OSD([sQuery(id+"F0.wireOp",EDGE,"E11.34.0")])]}),makeQuery(id+"F6.opExtrude","CAP_FACE",FACE,{"disambiguationData":[OSD([sQuery(id+"F5.wireOp",EDGE,"E119"),sQuery(id+"F5.wireOp",EDGE,"E120")])],"isStart":false})]});
            var Q53;
            Q53=makeQuery(id+"F6.boolean.opBoolean","INTERSECT",EDGE,{"derivedFrom":[makeQuery(id+"F1.opExtrude","SWEPT_FACE",FACE,{"disambiguationData":[OSD([sQuery(id+"F0.wireOp",EDGE,"E11.35.0")])]}),makeQuery(id+"F6.opExtrude","CAP_FACE",FACE,{"disambiguationData":[OSD([sQuery(id+"F5.wireOp",EDGE,"E119"),sQuery(id+"F5.wireOp",EDGE,"E120")])],"isStart":false})]});
            var Q54;
            Q54=makeQuery(id+"F6.boolean.opBoolean","INTERSECT",EDGE,{"derivedFrom":[makeQuery(id+"F1.opExtrude","SWEPT_FACE",FACE,{"disambiguationData":[OSD([sQuery(id+"F0.wireOp",EDGE,"E11.36.0")])]}),makeQuery(id+"F6.opExtrude","CAP_FACE",FACE,{"disambiguationData":[OSD([sQuery(id+"F5.wireOp",EDGE,"E119"),sQuery(id+"F5.wireOp",EDGE,"E120")])],"isStart":false})]});
            var Q55;
            Q55=makeQuery(id+"F6.boolean.opBoolean","INTERSECT",EDGE,{"derivedFrom":[makeQuery(id+"F1.opExtrude","SWEPT_FACE",FACE,{"disambiguationData":[OSD([sQuery(id+"F0.wireOp",EDGE,"E11.37.0")])]}),makeQuery(id+"F6.opExtrude","CAP_FACE",FACE,{"disambiguationData":[OSD([sQuery(id+"F5.wireOp",EDGE,"E119"),sQuery(id+"F5.wireOp",EDGE,"E120")])],"isStart":false})]});
            var Q56;
            Q56=makeQuery(id+"F6.boolean.opBoolean","INTERSECT",EDGE,{"derivedFrom":[makeQuery(id+"F1.opExtrude","SWEPT_FACE",FACE,{"disambiguationData":[OSD([sQuery(id+"F0.wireOp",EDGE,"E11.38.0")])]}),makeQuery(id+"F6.opExtrude","CAP_FACE",FACE,{"disambiguationData":[OSD([sQuery(id+"F5.wireOp",EDGE,"E119"),sQuery(id+"F5.wireOp",EDGE,"E120")])],"isStart":false})]});
            var Q57;
            Q57=makeQuery(id+"F6.boolean.opBoolean","INTERSECT",EDGE,{"derivedFrom":[makeQuery(id+"F1.opExtrude","SWEPT_FACE",FACE,{"disambiguationData":[OSD([sQuery(id+"F0.wireOp",EDGE,"E11.39.0")])]}),makeQuery(id+"F6.opExtrude","CAP_FACE",FACE,{"disambiguationData":[OSD([sQuery(id+"F5.wireOp",EDGE,"E119"),sQuery(id+"F5.wireOp",EDGE,"E120")])],"isStart":false})]});
            var Q58;
            Q58=makeQuery(id+"F6.boolean.opBoolean","INTERSECT",EDGE,{"derivedFrom":[makeQuery(id+"F1.opExtrude","SWEPT_FACE",FACE,{"disambiguationData":[OSD([sQuery(id+"F0.wireOp",EDGE,"E11.40.0")])]}),makeQuery(id+"F6.opExtrude","CAP_FACE",FACE,{"disambiguationData":[OSD([sQuery(id+"F5.wireOp",EDGE,"E119"),sQuery(id+"F5.wireOp",EDGE,"E120")])],"isStart":false})]});
            var Q59;
            Q59=makeQuery(id+"F6.boolean.opBoolean","INTERSECT",EDGE,{"derivedFrom":[makeQuery(id+"F1.opExtrude","SWEPT_FACE",FACE,{"disambiguationData":[OSD([sQuery(id+"F0.wireOp",EDGE,"E11.41.0")])]}),makeQuery(id+"F6.opExtrude","CAP_FACE",FACE,{"disambiguationData":[OSD([sQuery(id+"F5.wireOp",EDGE,"E119"),sQuery(id+"F5.wireOp",EDGE,"E120")])],"isStart":false})]});
            var Q60;
            Q60=makeQuery(id+"F6.boolean.opBoolean","INTERSECT",EDGE,{"derivedFrom":[makeQuery(id+"F1.opExtrude","SWEPT_FACE",FACE,{"disambiguationData":[OSD([sQuery(id+"F0.wireOp",EDGE,"E11.42.0")])]}),makeQuery(id+"F6.opExtrude","CAP_FACE",FACE,{"disambiguationData":[OSD([sQuery(id+"F5.wireOp",EDGE,"E119"),sQuery(id+"F5.wireOp",EDGE,"E120")])],"isStart":false})]});
            var Q61;
            Q61=makeQuery(id+"F6.boolean.opBoolean","INTERSECT",EDGE,{"derivedFrom":[makeQuery(id+"F1.opExtrude","SWEPT_FACE",FACE,{"disambiguationData":[OSD([sQuery(id+"F0.wireOp",EDGE,"E11.43.0")])]}),makeQuery(id+"F6.opExtrude","CAP_FACE",FACE,{"disambiguationData":[OSD([sQuery(id+"F5.wireOp",EDGE,"E119"),sQuery(id+"F5.wireOp",EDGE,"E120")])],"isStart":false})]});
            var Q62;
            Q62=makeQuery(id+"F6.boolean.opBoolean","INTERSECT",EDGE,{"derivedFrom":[makeQuery(id+"F1.opExtrude","SWEPT_FACE",FACE,{"disambiguationData":[OSD([sQuery(id+"F0.wireOp",EDGE,"E11.44.0")])]}),makeQuery(id+"F6.opExtrude","CAP_FACE",FACE,{"disambiguationData":[OSD([sQuery(id+"F5.wireOp",EDGE,"E119"),sQuery(id+"F5.wireOp",EDGE,"E120")])],"isStart":false})]});
            var Q63;
            Q63=makeQuery(id+"F6.boolean.opBoolean","INTERSECT",EDGE,{"derivedFrom":[makeQuery(id+"F1.opExtrude","SWEPT_FACE",FACE,{"disambiguationData":[OSD([sQuery(id+"F0.wireOp",EDGE,"E11.45.0")])]}),makeQuery(id+"F6.opExtrude","CAP_FACE",FACE,{"disambiguationData":[OSD([sQuery(id+"F5.wireOp",EDGE,"E119"),sQuery(id+"F5.wireOp",EDGE,"E120")])],"isStart":false})]});
            var Q64;
            Q64=makeQuery(id+"F6.boolean.opBoolean","INTERSECT",EDGE,{"derivedFrom":[makeQuery(id+"F1.opExtrude","SWEPT_FACE",FACE,{"disambiguationData":[OSD([sQuery(id+"F0.wireOp",EDGE,"E11.46.0")])]}),makeQuery(id+"F6.opExtrude","CAP_FACE",FACE,{"disambiguationData":[OSD([sQuery(id+"F5.wireOp",EDGE,"E119"),sQuery(id+"F5.wireOp",EDGE,"E120")])],"isStart":false})]});
            var Q65;
            Q65=makeQuery(id+"F6.boolean.opBoolean","INTERSECT",EDGE,{"derivedFrom":[makeQuery(id+"F1.opExtrude","SWEPT_FACE",FACE,{"disambiguationData":[OSD([sQuery(id+"F0.wireOp",EDGE,"E11.47.0")])]}),makeQuery(id+"F6.opExtrude","CAP_FACE",FACE,{"disambiguationData":[OSD([sQuery(id+"F5.wireOp",EDGE,"E119"),sQuery(id+"F5.wireOp",EDGE,"E120")])],"isStart":false})]});
            var Q66;
            Q66=makeQuery(id+"F6.boolean.opBoolean","INTERSECT",EDGE,{"derivedFrom":[makeQuery(id+"F1.opExtrude","SWEPT_FACE",FACE,{"disambiguationData":[OSD([sQuery(id+"F0.wireOp",EDGE,"E11.48.0")])]}),makeQuery(id+"F6.opExtrude","CAP_FACE",FACE,{"disambiguationData":[OSD([sQuery(id+"F5.wireOp",EDGE,"E119"),sQuery(id+"F5.wireOp",EDGE,"E120")])],"isStart":false})]});
            var Q67;
            Q67=makeQuery(id+"F6.boolean.opBoolean","INTERSECT",EDGE,{"derivedFrom":[makeQuery(id+"F1.opExtrude","SWEPT_FACE",FACE,{"disambiguationData":[OSD([sQuery(id+"F0.wireOp",EDGE,"E11.49.0")])]}),makeQuery(id+"F6.opExtrude","CAP_FACE",FACE,{"disambiguationData":[OSD([sQuery(id+"F5.wireOp",EDGE,"E119"),sQuery(id+"F5.wireOp",EDGE,"E120")])],"isStart":false})]});
            var Q68;
            Q68=makeQuery(id+"F6.boolean.opBoolean","INTERSECT",EDGE,{"derivedFrom":[makeQuery(id+"F1.opExtrude","SWEPT_FACE",FACE,{"disambiguationData":[OSD([sQuery(id+"F0.wireOp",EDGE,"E11.50.0")])]}),makeQuery(id+"F6.opExtrude","CAP_FACE",FACE,{"disambiguationData":[OSD([sQuery(id+"F5.wireOp",EDGE,"E119"),sQuery(id+"F5.wireOp",EDGE,"E120")])],"isStart":false})]});
            var Q69;
            Q69=makeQuery(id+"F6.boolean.opBoolean","INTERSECT",EDGE,{"derivedFrom":[makeQuery(id+"F1.opExtrude","SWEPT_FACE",FACE,{"disambiguationData":[OSD([sQuery(id+"F0.wireOp",EDGE,"E11.51.0")])]}),makeQuery(id+"F6.opExtrude","CAP_FACE",FACE,{"disambiguationData":[OSD([sQuery(id+"F5.wireOp",EDGE,"E119"),sQuery(id+"F5.wireOp",EDGE,"E120")])],"isStart":false})]});
            var Q70;
            Q70=makeQuery(id+"F6.boolean.opBoolean","INTERSECT",EDGE,{"derivedFrom":[makeQuery(id+"F1.opExtrude","SWEPT_FACE",FACE,{"disambiguationData":[OSD([sQuery(id+"F0.wireOp",EDGE,"E11.52.0")])]}),makeQuery(id+"F6.opExtrude","CAP_FACE",FACE,{"disambiguationData":[OSD([sQuery(id+"F5.wireOp",EDGE,"E119"),sQuery(id+"F5.wireOp",EDGE,"E120")])],"isStart":false})]});
            var Q71;
            Q71=makeQuery(id+"F6.boolean.opBoolean","INTERSECT",EDGE,{"derivedFrom":[makeQuery(id+"F1.opExtrude","SWEPT_FACE",FACE,{"disambiguationData":[OSD([sQuery(id+"F0.wireOp",EDGE,"E11.53.0")])]}),makeQuery(id+"F6.opExtrude","CAP_FACE",FACE,{"disambiguationData":[OSD([sQuery(id+"F5.wireOp",EDGE,"E119"),sQuery(id+"F5.wireOp",EDGE,"E120")])],"isStart":false})]});
            var Q72;
            Q72=makeQuery(id+"F6.boolean.opBoolean","INTERSECT",EDGE,{"derivedFrom":[makeQuery(id+"F1.opExtrude","SWEPT_FACE",FACE,{"disambiguationData":[OSD([sQuery(id+"F0.wireOp",EDGE,"E11.54.0")])]}),makeQuery(id+"F6.opExtrude","CAP_FACE",FACE,{"disambiguationData":[OSD([sQuery(id+"F5.wireOp",EDGE,"E119"),sQuery(id+"F5.wireOp",EDGE,"E120")])],"isStart":false})]});
            var Q73;
            Q73=makeQuery(id+"F6.boolean.opBoolean","INTERSECT",EDGE,{"derivedFrom":[makeQuery(id+"F1.opExtrude","SWEPT_FACE",FACE,{"disambiguationData":[OSD([sQuery(id+"F0.wireOp",EDGE,"E11.55.0")])]}),makeQuery(id+"F6.opExtrude","CAP_FACE",FACE,{"disambiguationData":[OSD([sQuery(id+"F5.wireOp",EDGE,"E119"),sQuery(id+"F5.wireOp",EDGE,"E120")])],"isStart":false})]});
            var Q74;
            Q74=makeQuery(id+"F6.boolean.opBoolean","INTERSECT",EDGE,{"derivedFrom":[makeQuery(id+"F1.opExtrude","SWEPT_FACE",FACE,{"disambiguationData":[OSD([sQuery(id+"F0.wireOp",EDGE,"E11.56.0")])]}),makeQuery(id+"F6.opExtrude","CAP_FACE",FACE,{"disambiguationData":[OSD([sQuery(id+"F5.wireOp",EDGE,"E119"),sQuery(id+"F5.wireOp",EDGE,"E120")])],"isStart":false})]});
            var Q75;
            Q75=makeQuery(id+"F6.boolean.opBoolean","INTERSECT",EDGE,{"derivedFrom":[makeQuery(id+"F1.opExtrude","SWEPT_FACE",FACE,{"disambiguationData":[OSD([sQuery(id+"F0.wireOp",EDGE,"E11.57.0")])]}),makeQuery(id+"F6.opExtrude","CAP_FACE",FACE,{"disambiguationData":[OSD([sQuery(id+"F5.wireOp",EDGE,"E119"),sQuery(id+"F5.wireOp",EDGE,"E120")])],"isStart":false})]});
            var Q76;
            Q76=makeQuery(id+"F6.boolean.opBoolean","INTERSECT",EDGE,{"derivedFrom":[makeQuery(id+"F1.opExtrude","SWEPT_FACE",FACE,{"disambiguationData":[OSD([sQuery(id+"F0.wireOp",EDGE,"E11.58.0")])]}),makeQuery(id+"F6.opExtrude","CAP_FACE",FACE,{"disambiguationData":[OSD([sQuery(id+"F5.wireOp",EDGE,"E119"),sQuery(id+"F5.wireOp",EDGE,"E120")])],"isStart":false})]});
            var Q77;
            Q77=makeQuery(id+"F6.boolean.opBoolean","INTERSECT",EDGE,{"derivedFrom":[makeQuery(id+"F1.opExtrude","SWEPT_FACE",FACE,{"disambiguationData":[OSD([sQuery(id+"F0.wireOp",EDGE,"E11.60.0")])]}),makeQuery(id+"F6.opExtrude","CAP_FACE",FACE,{"disambiguationData":[OSD([sQuery(id+"F5.wireOp",EDGE,"E119"),sQuery(id+"F5.wireOp",EDGE,"E120")])],"isStart":false})]});
            var Q78;
            Q78=makeQuery(id+"F6.boolean.opBoolean","INTERSECT",EDGE,{"derivedFrom":[makeQuery(id+"F1.opExtrude","SWEPT_FACE",FACE,{"disambiguationData":[OSD([sQuery(id+"F0.wireOp",EDGE,"E11.59.0")])]}),makeQuery(id+"F6.opExtrude","CAP_FACE",FACE,{"disambiguationData":[OSD([sQuery(id+"F5.wireOp",EDGE,"E119"),sQuery(id+"F5.wireOp",EDGE,"E120")])],"isStart":false})]});
            var Q79;
            Q79=makeQuery(id+"F6.boolean.opBoolean","INTERSECT",EDGE,{"derivedFrom":[makeQuery(id+"F1.opExtrude","SWEPT_FACE",FACE,{"disambiguationData":[OSD([sQuery(id+"F0.wireOp",EDGE,"E11.61.0")])]}),makeQuery(id+"F6.opExtrude","CAP_FACE",FACE,{"disambiguationData":[OSD([sQuery(id+"F5.wireOp",EDGE,"E119"),sQuery(id+"F5.wireOp",EDGE,"E120")])],"isStart":false})]});
            var Q80;
            Q80=makeQuery(id+"F6.boolean.opBoolean","INTERSECT",EDGE,{"derivedFrom":[makeQuery(id+"F1.opExtrude","SWEPT_FACE",FACE,{"disambiguationData":[OSD([sQuery(id+"F0.wireOp",EDGE,"E11.62.0")])]}),makeQuery(id+"F6.opExtrude","CAP_FACE",FACE,{"disambiguationData":[OSD([sQuery(id+"F5.wireOp",EDGE,"E119"),sQuery(id+"F5.wireOp",EDGE,"E120")])],"isStart":false})]});
            var Q81;
            Q81=makeQuery(id+"F6.boolean.opBoolean","INTERSECT",EDGE,{"derivedFrom":[makeQuery(id+"F1.opExtrude","SWEPT_FACE",FACE,{"disambiguationData":[OSD([sQuery(id+"F0.wireOp",EDGE,"E11.63.0")])]}),makeQuery(id+"F6.opExtrude","CAP_FACE",FACE,{"disambiguationData":[OSD([sQuery(id+"F5.wireOp",EDGE,"E119"),sQuery(id+"F5.wireOp",EDGE,"E120")])],"isStart":false})]});
            var Q82;
            Q82=makeQuery(id+"F6.boolean.opBoolean","INTERSECT",EDGE,{"derivedFrom":[makeQuery(id+"F1.opExtrude","SWEPT_FACE",FACE,{"disambiguationData":[OSD([sQuery(id+"F0.wireOp",EDGE,"E11.64.0")])]}),makeQuery(id+"F6.opExtrude","CAP_FACE",FACE,{"disambiguationData":[OSD([sQuery(id+"F5.wireOp",EDGE,"E119"),sQuery(id+"F5.wireOp",EDGE,"E120")])],"isStart":false})]});
            var Q83;
            Q83=makeQuery(id+"F6.boolean.opBoolean","INTERSECT",EDGE,{"derivedFrom":[makeQuery(id+"F1.opExtrude","SWEPT_FACE",FACE,{"disambiguationData":[OSD([sQuery(id+"F0.wireOp",EDGE,"E11.65.0")])]}),makeQuery(id+"F6.opExtrude","CAP_FACE",FACE,{"disambiguationData":[OSD([sQuery(id+"F5.wireOp",EDGE,"E119"),sQuery(id+"F5.wireOp",EDGE,"E120")])],"isStart":false})]});
            var Q84;
            Q84=makeQuery(id+"F6.boolean.opBoolean","INTERSECT",EDGE,{"derivedFrom":[makeQuery(id+"F1.opExtrude","SWEPT_FACE",FACE,{"disambiguationData":[OSD([sQuery(id+"F0.wireOp",EDGE,"E11.66.0")])]}),makeQuery(id+"F6.opExtrude","CAP_FACE",FACE,{"disambiguationData":[OSD([sQuery(id+"F5.wireOp",EDGE,"E119"),sQuery(id+"F5.wireOp",EDGE,"E120")])],"isStart":false})]});
            var Q85;
            Q85=makeQuery(id+"F6.boolean.opBoolean","INTERSECT",EDGE,{"derivedFrom":[makeQuery(id+"F1.opExtrude","SWEPT_FACE",FACE,{"disambiguationData":[OSD([sQuery(id+"F0.wireOp",EDGE,"E11.67.0")])]}),makeQuery(id+"F6.opExtrude","CAP_FACE",FACE,{"disambiguationData":[OSD([sQuery(id+"F5.wireOp",EDGE,"E119"),sQuery(id+"F5.wireOp",EDGE,"E120")])],"isStart":false})]});
            var Q86;
            Q86=makeQuery(id+"F6.boolean.opBoolean","INTERSECT",EDGE,{"derivedFrom":[makeQuery(id+"F1.opExtrude","SWEPT_FACE",FACE,{"disambiguationData":[OSD([sQuery(id+"F0.wireOp",EDGE,"E11.68.0")])]}),makeQuery(id+"F6.opExtrude","CAP_FACE",FACE,{"disambiguationData":[OSD([sQuery(id+"F5.wireOp",EDGE,"E119"),sQuery(id+"F5.wireOp",EDGE,"E120")])],"isStart":false})]});
            var Q87;
            Q87=makeQuery(id+"F6.boolean.opBoolean","INTERSECT",EDGE,{"derivedFrom":[makeQuery(id+"F1.opExtrude","SWEPT_FACE",FACE,{"disambiguationData":[OSD([sQuery(id+"F0.wireOp",EDGE,"E11.69.0")])]}),makeQuery(id+"F6.opExtrude","CAP_FACE",FACE,{"disambiguationData":[OSD([sQuery(id+"F5.wireOp",EDGE,"E119"),sQuery(id+"F5.wireOp",EDGE,"E120")])],"isStart":false})]});
            var Q88;
            Q88=makeQuery(id+"F6.boolean.opBoolean","INTERSECT",EDGE,{"derivedFrom":[makeQuery(id+"F1.opExtrude","SWEPT_FACE",FACE,{"disambiguationData":[OSD([sQuery(id+"F0.wireOp",EDGE,"E11.70.0")])]}),makeQuery(id+"F6.opExtrude","CAP_FACE",FACE,{"disambiguationData":[OSD([sQuery(id+"F5.wireOp",EDGE,"E119"),sQuery(id+"F5.wireOp",EDGE,"E120")])],"isStart":false})]});
            var Q89;
            Q89=makeQuery(id+"F6.boolean.opBoolean","INTERSECT",EDGE,{"derivedFrom":[makeQuery(id+"F1.opExtrude","SWEPT_FACE",FACE,{"disambiguationData":[OSD([sQuery(id+"F0.wireOp",EDGE,"E11.71.0")])]}),makeQuery(id+"F6.opExtrude","CAP_FACE",FACE,{"disambiguationData":[OSD([sQuery(id+"F5.wireOp",EDGE,"E119"),sQuery(id+"F5.wireOp",EDGE,"E120")])],"isStart":false})]});
            var Q90;
            Q90=makeQuery(id+"F6.boolean.opBoolean","INTERSECT",EDGE,{"derivedFrom":[makeQuery(id+"F1.opExtrude","SWEPT_FACE",FACE,{"disambiguationData":[OSD([sQuery(id+"F0.wireOp",EDGE,"E11.72.0")])]}),makeQuery(id+"F6.opExtrude","CAP_FACE",FACE,{"disambiguationData":[OSD([sQuery(id+"F5.wireOp",EDGE,"E119"),sQuery(id+"F5.wireOp",EDGE,"E120")])],"isStart":false})]});
            var Q91;
            Q91=makeQuery(id+"F6.boolean.opBoolean","INTERSECT",EDGE,{"derivedFrom":[makeQuery(id+"F1.opExtrude","SWEPT_FACE",FACE,{"disambiguationData":[OSD([sQuery(id+"F0.wireOp",EDGE,"E11.73.0")])]}),makeQuery(id+"F6.opExtrude","CAP_FACE",FACE,{"disambiguationData":[OSD([sQuery(id+"F5.wireOp",EDGE,"E119"),sQuery(id+"F5.wireOp",EDGE,"E120")])],"isStart":false})]});
            var Q92;
            Q92=makeQuery(id+"F6.boolean.opBoolean","INTERSECT",EDGE,{"derivedFrom":[makeQuery(id+"F1.opExtrude","SWEPT_FACE",FACE,{"disambiguationData":[OSD([sQuery(id+"F0.wireOp",EDGE,"E11.74.0")])]}),makeQuery(id+"F6.opExtrude","CAP_FACE",FACE,{"disambiguationData":[OSD([sQuery(id+"F5.wireOp",EDGE,"E119"),sQuery(id+"F5.wireOp",EDGE,"E120")])],"isStart":false})]});
            var Q93;
            Q93=makeQuery(id+"F6.boolean.opBoolean","INTERSECT",EDGE,{"derivedFrom":[makeQuery(id+"F1.opExtrude","SWEPT_FACE",FACE,{"disambiguationData":[OSD([sQuery(id+"F0.wireOp",EDGE,"E11.76.0")])]}),makeQuery(id+"F6.opExtrude","CAP_FACE",FACE,{"disambiguationData":[OSD([sQuery(id+"F5.wireOp",EDGE,"E119"),sQuery(id+"F5.wireOp",EDGE,"E120")])],"isStart":false})]});
            var Q94;
            Q94=makeQuery(id+"F6.boolean.opBoolean","INTERSECT",EDGE,{"derivedFrom":[makeQuery(id+"F1.opExtrude","SWEPT_FACE",FACE,{"disambiguationData":[OSD([sQuery(id+"F0.wireOp",EDGE,"E11.77.0")])]}),makeQuery(id+"F6.opExtrude","CAP_FACE",FACE,{"disambiguationData":[OSD([sQuery(id+"F5.wireOp",EDGE,"E119"),sQuery(id+"F5.wireOp",EDGE,"E120")])],"isStart":false})]});
            var Q95;
            Q95=makeQuery(id+"F6.boolean.opBoolean","INTERSECT",EDGE,{"derivedFrom":[makeQuery(id+"F1.opExtrude","SWEPT_FACE",FACE,{"disambiguationData":[OSD([sQuery(id+"F0.wireOp",EDGE,"E11.78.0")])]}),makeQuery(id+"F6.opExtrude","CAP_FACE",FACE,{"disambiguationData":[OSD([sQuery(id+"F5.wireOp",EDGE,"E119"),sQuery(id+"F5.wireOp",EDGE,"E120")])],"isStart":false})]});
            var Q96;
            Q96=makeQuery(id+"F6.boolean.opBoolean","INTERSECT",EDGE,{"derivedFrom":[makeQuery(id+"F1.opExtrude","SWEPT_FACE",FACE,{"disambiguationData":[OSD([sQuery(id+"F0.wireOp",EDGE,"E11.79.0")])]}),makeQuery(id+"F6.opExtrude","CAP_FACE",FACE,{"disambiguationData":[OSD([sQuery(id+"F5.wireOp",EDGE,"E119"),sQuery(id+"F5.wireOp",EDGE,"E120")])],"isStart":false})]});
            var Q97;
            Q97=makeQuery(id+"F6.boolean.opBoolean","INTERSECT",EDGE,{"derivedFrom":[makeQuery(id+"F1.opExtrude","SWEPT_FACE",FACE,{"disambiguationData":[OSD([sQuery(id+"F0.wireOp",EDGE,"E11.80.0")])]}),makeQuery(id+"F6.opExtrude","CAP_FACE",FACE,{"disambiguationData":[OSD([sQuery(id+"F5.wireOp",EDGE,"E119"),sQuery(id+"F5.wireOp",EDGE,"E120")])],"isStart":false})]});
            var Q98;
            Q98=makeQuery(id+"F6.boolean.opBoolean","INTERSECT",EDGE,{"derivedFrom":[makeQuery(id+"F1.opExtrude","SWEPT_FACE",FACE,{"disambiguationData":[OSD([sQuery(id+"F0.wireOp",EDGE,"E11.81.0")])]}),makeQuery(id+"F6.opExtrude","CAP_FACE",FACE,{"disambiguationData":[OSD([sQuery(id+"F5.wireOp",EDGE,"E119"),sQuery(id+"F5.wireOp",EDGE,"E120")])],"isStart":false})]});
            var Q99;
            {var subQ0=sQuery(id+"F5.wireOp",EDGE,"E119");Q99=makeQuery(id+"FZDd3dyAwVUtAiM_1.opFillet","BLEND_EDGE",EDGE,{"blendedFrom":[makeQuery(id+"F10.opPattern","COPY",EDGE,{"derivedFrom":makeQuery(id+"F9.opExtrude","CAP_EDGE",EDGE,{"disambiguationData":[OSD([sQuery(id+"F8.wireOp",EDGE,"E121.0.1")])],"isStart":true}),"instanceName":"3"}),makeQuery(id+"F6.boolean.opBoolean","COPY",FACE,{"disambiguationData":[TD([makeQuery(id+"F1.opExtrude","SWEPT_FACE",FACE,{"disambiguationData":[OSD([sQuery(id+"F0.wireOp",EDGE,"E11.75.0")])]})])],"derivedFrom":makeQuery(id+"F6.opExtrude","CAP_FACE",FACE,{"disambiguationData":[OSD([subQ0,sQuery(id+"F5.wireOp",EDGE,"E120")])],"isStart":false})})],"blendedInto":[makeQuery(id+"F6.boolean.opBoolean","COPY",FACE,{"disambiguationData":[TD([makeQuery(id+"F1.opExtrude","SWEPT_FACE",FACE,{"disambiguationData":[OSD([sQuery(id+"F0.wireOp",EDGE,"E11.75.0")])]})])],"derivedFrom":makeQuery(id+"F6.opExtrude","CAP_FACE",FACE,{"disambiguationData":[OSD([subQ0,sQuery(id+"F5.wireOp",EDGE,"E120")])],"isStart":false})})]});}
            chamfer(context, id + "F11", {"entities" : qUnion([Q0, Q1, Q2, Q3, Q4, Q5, Q6, Q7, Q8, Q9, Q10, Q11, Q12, Q13, Q14, Q15, Q16, Q17, Q18, Q19, Q20, Q21, Q22, Q23, Q24, Q25, Q26, Q27, Q28, Q29, Q30, Q31, Q32, Q33, Q34, Q35, Q36, Q37, Q38, Q39, Q40, Q41, Q42, Q43, Q44, Q45, Q46, Q47, Q48, Q49, Q50, Q51, Q52, Q53, Q54, Q55, Q56, Q57, Q58, Q59, Q60, Q61, Q62, Q63, Q64, Q65, Q66, Q67, Q68, Q69, Q70, Q71, Q72, Q73, Q74, Q75, Q76, Q77, Q78, Q79, Q80, Q81, Q82, Q83, Q84, Q85, Q86, Q87, Q88, Q89, Q90, Q91, Q92, Q93, Q94, Q95, Q96, Q97, Q98, Q99]), "width" : 0.5 * mm, "tangentPropagation" : true});
        }
        {
            var Q0;
            Q0=makeQuery(id+"F10.opPattern","COPY",FACE,{"derivedFrom":makeQuery(id+"F9.opExtrude","CAP_FACE",FACE,{"disambiguationData":[OSD([sQuery(id+"F8.wireOp",EDGE,"E121.0.0"),sQuery(id+"F8.wireOp",EDGE,"E121.0.1"),sQuery(id+"F8.wireOp",EDGE,"E121.0.2"),sQuery(id+"F8.wireOp",EDGE,"E121.0.3")])],"isStart":true}),"instanceName":"2"});
            var sketch = newSketch(context, id + "F12", { "sketchPlane" : qUnion([Q0])});
            skLineSegment(sketch, "E122", {"start": v(10, 2) * mm, "end": v(10, -2) * mm});
            skLineSegment(sketch, "E123", {"start": v(10, -2) * mm, "end": v(0, -2) * mm});
            skLineSegment(sketch, "E124", {"start": v(0, -2) * mm, "end": v(0, 2) * mm});
            skLineSegment(sketch, "E125", {"start": v(0, 2) * mm, "end": v(10, 2) * mm});
            skSolve(sketch);
        }
        {
            var Q0;
            Q0 = qSketchRegion(id + "F12", true);
            extrude(context, id + "F13", {"entities" : qUnion([Q0]), "operationType" : NewBodyOperationType.REMOVE, "oppositeDirection" : true, "depth" : 2 * mm, "offsetDistance" : 25 * mm});
        }
        {
            var Q0;
            Q0=makeQuery(id+"F10.opPattern","COPY",FACE,{"derivedFrom":makeQuery(id+"F9.opExtrude","CAP_FACE",FACE,{"disambiguationData":[OSD([sQuery(id+"F8.wireOp",EDGE,"E121.0.0"),sQuery(id+"F8.wireOp",EDGE,"E121.0.1"),sQuery(id+"F8.wireOp",EDGE,"E121.0.2"),sQuery(id+"F8.wireOp",EDGE,"E121.0.3")])],"isStart":true}),"instanceName":"4"});
            var sketch = newSketch(context, id + "F14", { "sketchPlane" : qUnion([Q0])});
            skLineSegment(sketch, "E126", {"start": v(-2, 0) * mm, "end": v(-2, 10.25) * mm});
            skLineSegment(sketch, "E127", {"start": v(-2, 10.25) * mm, "end": v(2, 10.25) * mm});
            skLineSegment(sketch, "E128", {"start": v(2, 10.25) * mm, "end": v(2, 0) * mm});
            skLineSegment(sketch, "E129", {"start": v(2, 0) * mm, "end": v(-2, 0) * mm});
            skSolve(sketch);
        }
        {
            var Q0;
            Q0 = qSketchRegion(id + "F14", true);
            extrude(context, id + "F15", {"entities" : qUnion([Q0]), "operationType" : NewBodyOperationType.REMOVE, "oppositeDirection" : true, "depth" : 2 * mm, "offsetDistance" : 25 * mm});
        }
        {
            var Q0;
            Q0=makeQuery(id+"F10.opPattern","COPY",FACE,{"derivedFrom":makeQuery(id+"F9.opExtrude","CAP_FACE",FACE,{"disambiguationData":[OSD([sQuery(id+"F8.wireOp",EDGE,"E121.0.0"),sQuery(id+"F8.wireOp",EDGE,"E121.0.1"),sQuery(id+"F8.wireOp",EDGE,"E121.0.2"),sQuery(id+"F8.wireOp",EDGE,"E121.0.3")])],"isStart":true}),"instanceName":"6"});
            var sketch = newSketch(context, id + "F16", { "sketchPlane" : qUnion([Q0])});
            skLineSegment(sketch, "E130", {"start": v(0, 2) * mm, "end": v(-10, 2) * mm});
            skLineSegment(sketch, "E131", {"start": v(-10, 2) * mm, "end": v(-10, -2) * mm});
            skLineSegment(sketch, "E132", {"start": v(-10, -2) * mm, "end": v(0, -2) * mm});
            skLineSegment(sketch, "E133", {"start": v(0, -2) * mm, "end": v(0, 2) * mm});
            skSolve(sketch);
        }
        {
            var Q0;
            Q0 = qSketchRegion(id + "F16", true);
            extrude(context, id + "F17", {"entities" : qUnion([Q0]), "operationType" : NewBodyOperationType.REMOVE, "oppositeDirection" : true, "depth" : 2 * mm, "offsetDistance" : 25 * mm});
        }
        {
            var Q0;
            Q0=makeQuery(id+"F9.opExtrude","CAP_FACE",FACE,{"disambiguationData":[OSD([sQuery(id+"F8.wireOp",EDGE,"E121.0.0"),sQuery(id+"F8.wireOp",EDGE,"E121.0.1"),sQuery(id+"F8.wireOp",EDGE,"E121.0.2"),sQuery(id+"F8.wireOp",EDGE,"E121.0.3")])],"isStart":true});
            var sketch = newSketch(context, id + "F18", { "sketchPlane" : qUnion([Q0])});
            skLineSegment(sketch, "E134", {"start": v(2, 0) * mm, "end": v(2, -10) * mm});
            skLineSegment(sketch, "E135", {"start": v(2, -10) * mm, "end": v(-2, -10) * mm});
            skLineSegment(sketch, "E136", {"start": v(-2, -10) * mm, "end": v(-2, 0) * mm});
            skLineSegment(sketch, "E137", {"start": v(-2, 0) * mm, "end": v(2, 0) * mm});
            skSolve(sketch);
        }
        {
            var Q0;
            Q0 = qSketchRegion(id + "F18", true);
            extrude(context, id + "F19", {"entities" : qUnion([Q0]), "operationType" : NewBodyOperationType.REMOVE, "oppositeDirection" : true, "depth" : 2 * mm, "offsetDistance" : 25 * mm});
        }
        {
            var Q0;
            Q0=makeQuery(id+"F10.opPattern","COPY",EDGE,{"derivedFrom":makeQuery(id+"F9.opExtrude","CAP_EDGE",EDGE,{"disambiguationData":[OSD([sQuery(id+"F8.wireOp",EDGE,"E121.0.3")])],"isStart":true}),"instanceName":"4"});
            var Q1;
            Q1=makeQuery(id+"F10.opPattern","COPY",EDGE,{"derivedFrom":makeQuery(id+"F9.opExtrude","CAP_EDGE",EDGE,{"disambiguationData":[OSD([sQuery(id+"F8.wireOp",EDGE,"E121.0.1")])],"isStart":true}),"instanceName":"4"});
            var Q2;
            Q2=makeQuery(id+"F10.opPattern","COPY",EDGE,{"derivedFrom":makeQuery(id+"F9.opExtrude","CAP_EDGE",EDGE,{"disambiguationData":[OSD([sQuery(id+"F8.wireOp",EDGE,"E121.0.0")])],"isStart":true}),"instanceName":"3"});
            var Q3;
            Q3=makeQuery(id+"F10.opPattern","COPY",EDGE,{"derivedFrom":makeQuery(id+"F9.opExtrude","CAP_EDGE",EDGE,{"disambiguationData":[OSD([sQuery(id+"F8.wireOp",EDGE,"E121.0.3")])],"isStart":true}),"instanceName":"3"});
            var Q4;
            Q4=makeQuery(id+"F10.opPattern","COPY",EDGE,{"derivedFrom":makeQuery(id+"F9.opExtrude","CAP_EDGE",EDGE,{"disambiguationData":[OSD([sQuery(id+"F8.wireOp",EDGE,"E121.0.1")])],"isStart":true}),"instanceName":"3"});
            var Q5;
            Q5=makeQuery(id+"F10.opPattern","COPY",EDGE,{"derivedFrom":makeQuery(id+"F9.opExtrude","CAP_EDGE",EDGE,{"disambiguationData":[OSD([sQuery(id+"F8.wireOp",EDGE,"E121.0.3")])],"isStart":true}),"instanceName":"2"});
            var Q6;
            Q6=makeQuery(id+"F10.opPattern","COPY",EDGE,{"derivedFrom":makeQuery(id+"F9.opExtrude","CAP_EDGE",EDGE,{"disambiguationData":[OSD([sQuery(id+"F8.wireOp",EDGE,"E121.0.1")])],"isStart":true}),"instanceName":"2"});
            var Q7;
            Q7=makeQuery(id+"F10.opPattern","COPY",EDGE,{"derivedFrom":makeQuery(id+"F9.opExtrude","CAP_EDGE",EDGE,{"disambiguationData":[OSD([sQuery(id+"F8.wireOp",EDGE,"E121.0.3")])],"isStart":true}),"instanceName":"1"});
            var Q8;
            Q8=makeQuery(id+"F10.opPattern","COPY",EDGE,{"derivedFrom":makeQuery(id+"F9.opExtrude","CAP_EDGE",EDGE,{"disambiguationData":[OSD([sQuery(id+"F8.wireOp",EDGE,"E121.0.1")])],"isStart":true}),"instanceName":"1"});
            var Q9;
            Q9=makeQuery(id+"F10.opPattern","COPY",EDGE,{"derivedFrom":makeQuery(id+"F9.opExtrude","CAP_EDGE",EDGE,{"disambiguationData":[OSD([sQuery(id+"F8.wireOp",EDGE,"E121.0.0")])],"isStart":true}),"instanceName":"1"});
            var Q10;
            Q10=makeQuery(id+"F9.opExtrude","CAP_EDGE",EDGE,{"disambiguationData":[OSD([sQuery(id+"F8.wireOp",EDGE,"E121.0.3")])],"isStart":true});
            var Q11;
            Q11=makeQuery(id+"F9.opExtrude","CAP_EDGE",EDGE,{"disambiguationData":[OSD([sQuery(id+"F8.wireOp",EDGE,"E121.0.1")])],"isStart":true});
            var Q12;
            Q12=makeQuery(id+"F10.opPattern","COPY",EDGE,{"derivedFrom":makeQuery(id+"F9.opExtrude","CAP_EDGE",EDGE,{"disambiguationData":[OSD([sQuery(id+"F8.wireOp",EDGE,"E121.0.3")])],"isStart":true}),"instanceName":"7"});
            var Q13;
            Q13=makeQuery(id+"F10.opPattern","COPY",EDGE,{"derivedFrom":makeQuery(id+"F9.opExtrude","CAP_EDGE",EDGE,{"disambiguationData":[OSD([sQuery(id+"F8.wireOp",EDGE,"E121.0.1")])],"isStart":true}),"instanceName":"7"});
            var Q14;
            Q14=makeQuery(id+"F10.opPattern","COPY",EDGE,{"derivedFrom":makeQuery(id+"F9.opExtrude","CAP_EDGE",EDGE,{"disambiguationData":[OSD([sQuery(id+"F8.wireOp",EDGE,"E121.0.0")])],"isStart":true}),"instanceName":"7"});
            var Q15;
            Q15=makeQuery(id+"F10.opPattern","COPY",EDGE,{"derivedFrom":makeQuery(id+"F9.opExtrude","CAP_EDGE",EDGE,{"disambiguationData":[OSD([sQuery(id+"F8.wireOp",EDGE,"E121.0.3")])],"isStart":true}),"instanceName":"6"});
            var Q16;
            Q16=makeQuery(id+"F10.opPattern","COPY",EDGE,{"derivedFrom":makeQuery(id+"F9.opExtrude","CAP_EDGE",EDGE,{"disambiguationData":[OSD([sQuery(id+"F8.wireOp",EDGE,"E121.0.1")])],"isStart":true}),"instanceName":"6"});
            var Q17;
            Q17=makeQuery(id+"F10.opPattern","COPY",EDGE,{"derivedFrom":makeQuery(id+"F9.opExtrude","CAP_EDGE",EDGE,{"disambiguationData":[OSD([sQuery(id+"F8.wireOp",EDGE,"E121.0.3")])],"isStart":true}),"instanceName":"5"});
            var Q18;
            Q18=makeQuery(id+"F10.opPattern","COPY",EDGE,{"derivedFrom":makeQuery(id+"F9.opExtrude","CAP_EDGE",EDGE,{"disambiguationData":[OSD([sQuery(id+"F8.wireOp",EDGE,"E121.0.1")])],"isStart":true}),"instanceName":"5"});
            var Q19;
            Q19=makeQuery(id+"F10.opPattern","COPY",EDGE,{"derivedFrom":makeQuery(id+"F9.opExtrude","CAP_EDGE",EDGE,{"disambiguationData":[OSD([sQuery(id+"F8.wireOp",EDGE,"E121.0.0")])],"isStart":true}),"instanceName":"5"});
            fillet(context, id + "F20", {"entities" : qUnion([Q0, Q1, Q2, Q3, Q4, Q5, Q6, Q7, Q8, Q9, Q10, Q11, Q12, Q13, Q14, Q15, Q16, Q17, Q18, Q19]), "radius" : 2 * mm, "tangentPropagation" : true, "allowEdgeOverflow" : false});
        }
        {
            var Q0;
            Q0=makeQuery(id+"F20.opFillet","BLEND_EDGE",EDGE,{"blendedFrom":[makeQuery(id+"F10.opPattern","COPY",EDGE,{"derivedFrom":makeQuery(id+"F9.opExtrude","CAP_EDGE",EDGE,{"disambiguationData":[OSD([sQuery(id+"F8.wireOp",EDGE,"E121.0.1")])],"isStart":true}),"instanceName":"4"}),makeQuery(id+"F15.boolean.opBoolean","COPY",FACE,{"derivedFrom":makeQuery(id+"F15.opExtrude","SWEPT_FACE",FACE,{"disambiguationData":[OSD([sQuery(id+"F14.wireOp",EDGE,"E127")])]})})],"blendedInto":[makeQuery(id+"F15.boolean.opBoolean","COPY",FACE,{"derivedFrom":makeQuery(id+"F15.opExtrude","SWEPT_FACE",FACE,{"disambiguationData":[OSD([sQuery(id+"F14.wireOp",EDGE,"E127")])]})})]});
            var Q1;
            Q1=makeQuery(id+"F20.opFillet","BLEND_EDGE",EDGE,{"blendedFrom":[makeQuery(id+"F10.opPattern","COPY",EDGE,{"derivedFrom":makeQuery(id+"F9.opExtrude","CAP_EDGE",EDGE,{"disambiguationData":[OSD([sQuery(id+"F8.wireOp",EDGE,"E121.0.3")])],"isStart":true}),"instanceName":"2"}),makeQuery(id+"F13.boolean.opBoolean","COPY",FACE,{"derivedFrom":makeQuery(id+"F13.opExtrude","SWEPT_FACE",FACE,{"disambiguationData":[OSD([sQuery(id+"F12.wireOp",EDGE,"E122")])]})})],"blendedInto":[makeQuery(id+"F13.boolean.opBoolean","COPY",FACE,{"derivedFrom":makeQuery(id+"F13.opExtrude","SWEPT_FACE",FACE,{"disambiguationData":[OSD([sQuery(id+"F12.wireOp",EDGE,"E122")])]})})]});
            var Q2;
            Q2=makeQuery(id+"F20.opFillet","BLEND_EDGE",EDGE,{"blendedFrom":[makeQuery(id+"F9.opExtrude","CAP_EDGE",EDGE,{"disambiguationData":[OSD([sQuery(id+"F8.wireOp",EDGE,"E121.0.3")])],"isStart":true}),makeQuery(id+"F19.boolean.opBoolean","COPY",FACE,{"derivedFrom":makeQuery(id+"F19.opExtrude","SWEPT_FACE",FACE,{"disambiguationData":[OSD([sQuery(id+"F18.wireOp",EDGE,"E135")])]})})],"blendedInto":[makeQuery(id+"F19.boolean.opBoolean","COPY",FACE,{"derivedFrom":makeQuery(id+"F19.opExtrude","SWEPT_FACE",FACE,{"disambiguationData":[OSD([sQuery(id+"F18.wireOp",EDGE,"E135")])]})})]});
            var Q3;
            Q3=makeQuery(id+"F20.opFillet","BLEND_EDGE",EDGE,{"blendedFrom":[makeQuery(id+"F10.opPattern","COPY",EDGE,{"derivedFrom":makeQuery(id+"F9.opExtrude","CAP_EDGE",EDGE,{"disambiguationData":[OSD([sQuery(id+"F8.wireOp",EDGE,"E121.0.3")])],"isStart":true}),"instanceName":"6"}),makeQuery(id+"F17.boolean.opBoolean","COPY",FACE,{"derivedFrom":makeQuery(id+"F17.opExtrude","SWEPT_FACE",FACE,{"disambiguationData":[OSD([sQuery(id+"F16.wireOp",EDGE,"E131")])]})})],"blendedInto":[makeQuery(id+"F17.boolean.opBoolean","COPY",FACE,{"derivedFrom":makeQuery(id+"F17.opExtrude","SWEPT_FACE",FACE,{"disambiguationData":[OSD([sQuery(id+"F16.wireOp",EDGE,"E131")])]})})]});
            fillet(context, id + "F21", {"entities" : qUnion([Q0, Q1, Q2, Q3]), "radius" : 2 * mm, "tangentPropagation" : true, "allowEdgeOverflow" : false});
        }
        {
            var Q0;
            {var subQ0=sQuery(id+"F14.wireOp",EDGE,"E127");Q0=makeQuery(id+"F21.opFillet","BLEND_EDGE",EDGE,{"blendedFrom":[makeQuery(id+"F20.opFillet","BLEND_EDGE",EDGE,{"blendedFrom":[makeQuery(id+"F10.opPattern","COPY",EDGE,{"derivedFrom":makeQuery(id+"F9.opExtrude","CAP_EDGE",EDGE,{"disambiguationData":[OSD([sQuery(id+"F8.wireOp",EDGE,"E121.0.1")])],"isStart":true}),"instanceName":"4"}),makeQuery(id+"F15.boolean.opBoolean","COPY",FACE,{"derivedFrom":makeQuery(id+"F15.opExtrude","SWEPT_FACE",FACE,{"disambiguationData":[OSD([subQ0])]})})],"blendedInto":[makeQuery(id+"F15.boolean.opBoolean","COPY",FACE,{"derivedFrom":makeQuery(id+"F15.opExtrude","SWEPT_FACE",FACE,{"disambiguationData":[OSD([subQ0])]})})]}),makeQuery(id+"F15.boolean.opBoolean","COPY",FACE,{"derivedFrom":makeQuery(id+"F15.opExtrude","CAP_FACE",FACE,{"disambiguationData":[OSD([sQuery(id+"F14.wireOp",EDGE,"E126"),subQ0,sQuery(id+"F14.wireOp",EDGE,"E128"),sQuery(id+"F14.wireOp",EDGE,"E129")])],"isStart":false})})],"blendedInto":[makeQuery(id+"F15.boolean.opBoolean","COPY",FACE,{"derivedFrom":makeQuery(id+"F15.opExtrude","CAP_FACE",FACE,{"disambiguationData":[OSD([sQuery(id+"F14.wireOp",EDGE,"E126"),subQ0,sQuery(id+"F14.wireOp",EDGE,"E128"),sQuery(id+"F14.wireOp",EDGE,"E129")])],"isStart":false})})]});}
            var Q1;
            {var subQ0=sQuery(id+"F12.wireOp",EDGE,"E122");Q1=makeQuery(id+"F21.opFillet","BLEND_EDGE",EDGE,{"blendedFrom":[makeQuery(id+"F20.opFillet","BLEND_EDGE",EDGE,{"blendedFrom":[makeQuery(id+"F10.opPattern","COPY",EDGE,{"derivedFrom":makeQuery(id+"F9.opExtrude","CAP_EDGE",EDGE,{"disambiguationData":[OSD([sQuery(id+"F8.wireOp",EDGE,"E121.0.3")])],"isStart":true}),"instanceName":"2"}),makeQuery(id+"F13.boolean.opBoolean","COPY",FACE,{"derivedFrom":makeQuery(id+"F13.opExtrude","SWEPT_FACE",FACE,{"disambiguationData":[OSD([subQ0])]})})],"blendedInto":[makeQuery(id+"F13.boolean.opBoolean","COPY",FACE,{"derivedFrom":makeQuery(id+"F13.opExtrude","SWEPT_FACE",FACE,{"disambiguationData":[OSD([subQ0])]})})]}),makeQuery(id+"F13.boolean.opBoolean","COPY",FACE,{"derivedFrom":makeQuery(id+"F13.opExtrude","CAP_FACE",FACE,{"disambiguationData":[OSD([subQ0,sQuery(id+"F12.wireOp",EDGE,"E123"),sQuery(id+"F12.wireOp",EDGE,"E124"),sQuery(id+"F12.wireOp",EDGE,"E125")])],"isStart":false})})],"blendedInto":[makeQuery(id+"F13.boolean.opBoolean","COPY",FACE,{"derivedFrom":makeQuery(id+"F13.opExtrude","CAP_FACE",FACE,{"disambiguationData":[OSD([subQ0,sQuery(id+"F12.wireOp",EDGE,"E123"),sQuery(id+"F12.wireOp",EDGE,"E124"),sQuery(id+"F12.wireOp",EDGE,"E125")])],"isStart":false})})]});}
            var Q2;
            {var subQ0=sQuery(id+"F18.wireOp",EDGE,"E135");Q2=makeQuery(id+"F21.opFillet","BLEND_EDGE",EDGE,{"blendedFrom":[makeQuery(id+"F20.opFillet","BLEND_EDGE",EDGE,{"blendedFrom":[makeQuery(id+"F9.opExtrude","CAP_EDGE",EDGE,{"disambiguationData":[OSD([sQuery(id+"F8.wireOp",EDGE,"E121.0.3")])],"isStart":true}),makeQuery(id+"F19.boolean.opBoolean","COPY",FACE,{"derivedFrom":makeQuery(id+"F19.opExtrude","SWEPT_FACE",FACE,{"disambiguationData":[OSD([subQ0])]})})],"blendedInto":[makeQuery(id+"F19.boolean.opBoolean","COPY",FACE,{"derivedFrom":makeQuery(id+"F19.opExtrude","SWEPT_FACE",FACE,{"disambiguationData":[OSD([subQ0])]})})]}),makeQuery(id+"F19.boolean.opBoolean","COPY",FACE,{"derivedFrom":makeQuery(id+"F19.opExtrude","CAP_FACE",FACE,{"disambiguationData":[OSD([sQuery(id+"F18.wireOp",EDGE,"E134"),subQ0,sQuery(id+"F18.wireOp",EDGE,"E136"),sQuery(id+"F18.wireOp",EDGE,"E137")])],"isStart":false})})],"blendedInto":[makeQuery(id+"F19.boolean.opBoolean","COPY",FACE,{"derivedFrom":makeQuery(id+"F19.opExtrude","CAP_FACE",FACE,{"disambiguationData":[OSD([sQuery(id+"F18.wireOp",EDGE,"E134"),subQ0,sQuery(id+"F18.wireOp",EDGE,"E136"),sQuery(id+"F18.wireOp",EDGE,"E137")])],"isStart":false})})]});}
            var Q3;
            {var subQ0=sQuery(id+"F16.wireOp",EDGE,"E131");Q3=makeQuery(id+"F21.opFillet","BLEND_EDGE",EDGE,{"blendedFrom":[makeQuery(id+"F20.opFillet","BLEND_EDGE",EDGE,{"blendedFrom":[makeQuery(id+"F10.opPattern","COPY",EDGE,{"derivedFrom":makeQuery(id+"F9.opExtrude","CAP_EDGE",EDGE,{"disambiguationData":[OSD([sQuery(id+"F8.wireOp",EDGE,"E121.0.3")])],"isStart":true}),"instanceName":"6"}),makeQuery(id+"F17.boolean.opBoolean","COPY",FACE,{"derivedFrom":makeQuery(id+"F17.opExtrude","SWEPT_FACE",FACE,{"disambiguationData":[OSD([subQ0])]})})],"blendedInto":[makeQuery(id+"F17.boolean.opBoolean","COPY",FACE,{"derivedFrom":makeQuery(id+"F17.opExtrude","SWEPT_FACE",FACE,{"disambiguationData":[OSD([subQ0])]})})]}),makeQuery(id+"F17.boolean.opBoolean","COPY",FACE,{"derivedFrom":makeQuery(id+"F17.opExtrude","CAP_FACE",FACE,{"disambiguationData":[OSD([sQuery(id+"F16.wireOp",EDGE,"E130"),subQ0,sQuery(id+"F16.wireOp",EDGE,"E132"),sQuery(id+"F16.wireOp",EDGE,"E133")])],"isStart":false})})],"blendedInto":[makeQuery(id+"F17.boolean.opBoolean","COPY",FACE,{"derivedFrom":makeQuery(id+"F17.opExtrude","CAP_FACE",FACE,{"disambiguationData":[OSD([sQuery(id+"F16.wireOp",EDGE,"E130"),subQ0,sQuery(id+"F16.wireOp",EDGE,"E132"),sQuery(id+"F16.wireOp",EDGE,"E133")])],"isStart":false})})]});}
            fillet(context, id + "F22", {"entities" : qUnion([Q0, Q1, Q2, Q3]), "radius" : 0.5 * mm, "tangentPropagation" : true, "allowEdgeOverflow" : false});
        }
    });
